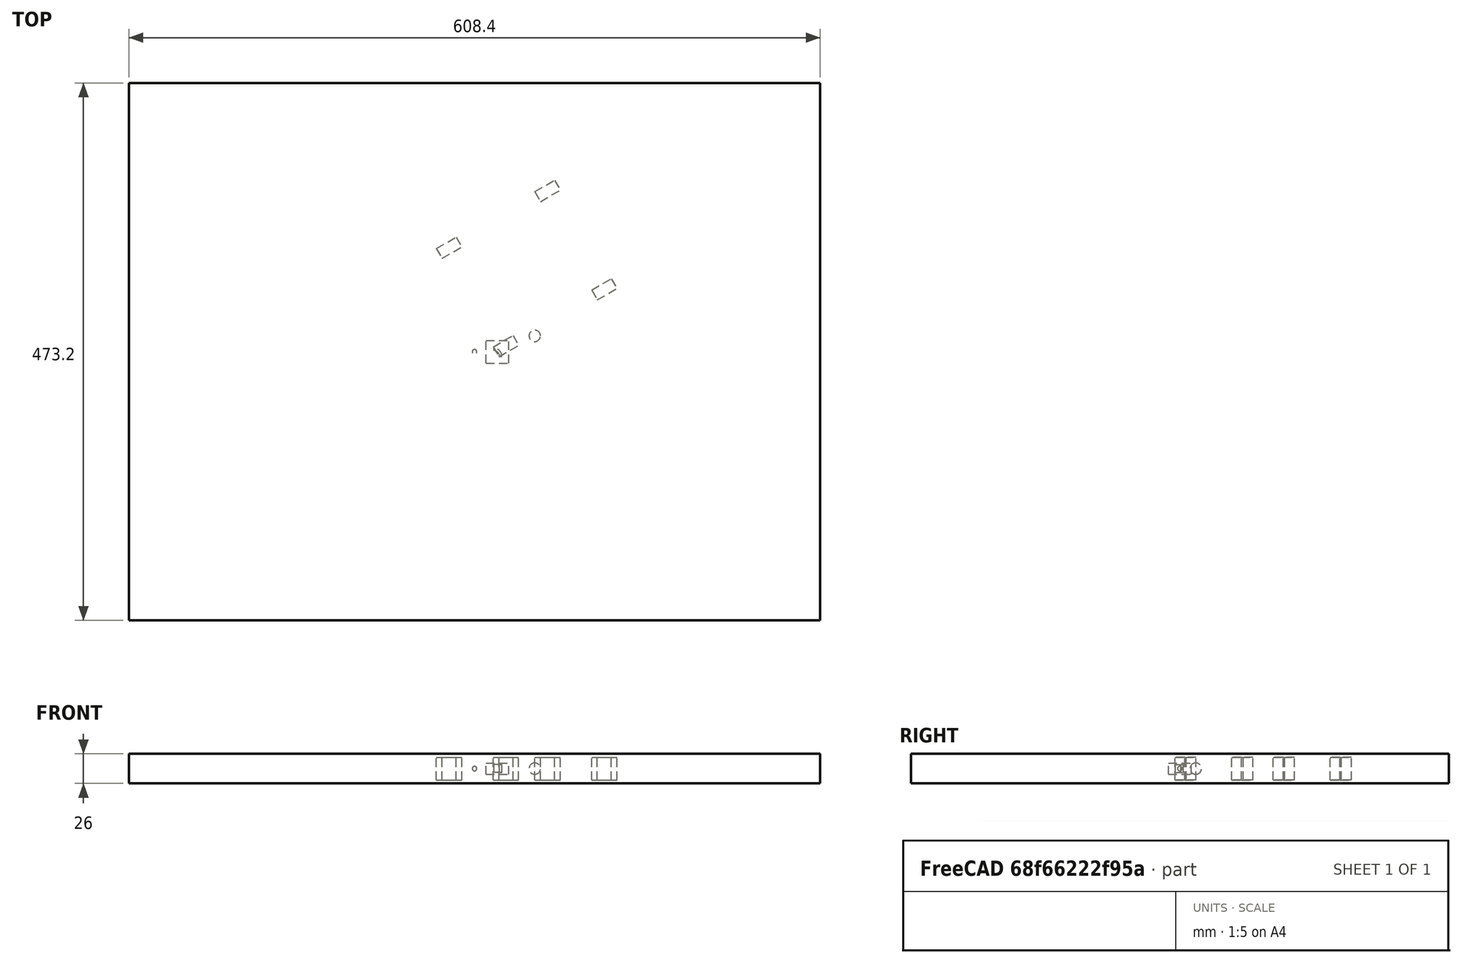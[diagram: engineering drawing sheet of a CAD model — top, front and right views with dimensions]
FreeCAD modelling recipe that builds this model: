
FCSTD DOCUMENT  (FreeCAD 1.0R39109 (Git))
Label: orthoArray-of-Container
License: All rights reserved
LicenseURL: http://en.wikipedia.org/wiki/All_rights_reserved
objects: App::DocumentObjectGroupPython×1251, App::Part×6, Part::FeaturePython×5, Part::Sphere×1
note: 6 computed .brp shape members not serialized (recipe doc carries the construction recipe); baked Part::Feature solids carry a one-line shape summary decoded from their .brp

FEATURE [App::DocumentObjectGroupPython] HALFPI  # scripted group (container) (typed FeaturePython)
  name = HALFPI
  value = pi/2.
FEATURE [App::DocumentObjectGroupPython] PI  # scripted group (container) (typed FeaturePython)
  name = PI
  value = 1.*pi
FEATURE [App::DocumentObjectGroupPython] TWOPI  # scripted group (container) (typed FeaturePython)
  name = TWOPI
  value = 2.*pi
FEATURE [App::DocumentObjectGroupPython] Constants  # scripted group (container) (typed FeaturePython)
  Group = -> [HALFPI,PI,TWOPI]
FEATURE [App::DocumentObjectGroupPython] Variables  # scripted group (container) (typed FeaturePython)
FEATURE [App::DocumentObjectGroupPython] Quantities  # scripted group (container) (typed FeaturePython)
FEATURE [App::DocumentObjectGroupPython] Isotopes  # scripted group (container) (typed FeaturePython)
FEATURE [App::DocumentObjectGroupPython] Elements  # scripted group (container) (typed FeaturePython)
FEATURE [App::DocumentObjectGroupPython] Matrix  # scripted group (container) (typed FeaturePython)
FEATURE [App::DocumentObjectGroupPython] Surfaces  # scripted group (container) (typed FeaturePython)
FEATURE [App::DocumentObjectGroupPython] Opticals  # scripted group (container) (typed FeaturePython)
  Group = -> [Matrix,Surfaces]
FEATURE [App::DocumentObjectGroupPython] G4Isotopes  # scripted group (container) (typed FeaturePython)
FEATURE [App::DocumentObjectGroupPython] H_element  # scripted group (container) (typed FeaturePython)
  Z = 1
  atom_value = 1.008
  formula = H
  name = H_element
FEATURE [App::DocumentObjectGroupPython] He_element  # scripted group (container) (typed FeaturePython)
  Z = 2
  atom_value = 4.0026
  formula = He
  name = He_element
FEATURE [App::DocumentObjectGroupPython] Li_element  # scripted group (container) (typed FeaturePython)
  Z = 3
  atom_value = 6.94
  formula = Li
  name = Li_element
FEATURE [App::DocumentObjectGroupPython] Be_element  # scripted group (container) (typed FeaturePython)
  Z = 4
  atom_value = 9.01218
  formula = Be
  name = Be_element
FEATURE [App::DocumentObjectGroupPython] B_element  # scripted group (container) (typed FeaturePython)
  Z = 5
  atom_value = 10.81
  formula = B
  name = B_element
FEATURE [App::DocumentObjectGroupPython] C_element  # scripted group (container) (typed FeaturePython)
  Z = 6
  atom_value = 12.011
  formula = C
  name = C_element
FEATURE [App::DocumentObjectGroupPython] N_element  # scripted group (container) (typed FeaturePython)
  Z = 7
  atom_value = 14.007
  formula = N
  name = N_element
FEATURE [App::DocumentObjectGroupPython] O_element  # scripted group (container) (typed FeaturePython)
  Z = 8
  atom_value = 15.999
  formula = O
  name = O_element
FEATURE [App::DocumentObjectGroupPython] F_element  # scripted group (container) (typed FeaturePython)
  Z = 9
  atom_value = 18.9984
  formula = F
  name = F_element
FEATURE [App::DocumentObjectGroupPython] Ne_element  # scripted group (container) (typed FeaturePython)
  Z = 10
  atom_value = 20.1797
  formula = Ne
  name = Ne_element
FEATURE [App::DocumentObjectGroupPython] Na_element  # scripted group (container) (typed FeaturePython)
  Z = 11
  atom_value = 22.9898
  formula = Na
  name = Na_element
FEATURE [App::DocumentObjectGroupPython] Mg_element  # scripted group (container) (typed FeaturePython)
  Z = 12
  atom_value = 24.305
  formula = Mg
  name = Mg_element
FEATURE [App::DocumentObjectGroupPython] Al_element  # scripted group (container) (typed FeaturePython)
  Z = 13
  atom_value = 26.9815
  formula = Al
  name = Al_element
FEATURE [App::DocumentObjectGroupPython] Si_element  # scripted group (container) (typed FeaturePython)
  Z = 14
  atom_value = 28.085
  formula = Si
  name = Si_element
FEATURE [App::DocumentObjectGroupPython] P_element  # scripted group (container) (typed FeaturePython)
  Z = 15
  atom_value = 30.9738
  formula = P
  name = P_element
FEATURE [App::DocumentObjectGroupPython] S_element  # scripted group (container) (typed FeaturePython)
  Z = 16
  atom_value = 32.06
  formula = S
  name = S_element
FEATURE [App::DocumentObjectGroupPython] Cl_element  # scripted group (container) (typed FeaturePython)
  Z = 17
  atom_value = 35.45
  formula = Cl
  name = Cl_element
FEATURE [App::DocumentObjectGroupPython] Ar_element  # scripted group (container) (typed FeaturePython)
  Z = 18
  atom_value = 39.95
  formula = Ar
  name = Ar_element
FEATURE [App::DocumentObjectGroupPython] K_element  # scripted group (container) (typed FeaturePython)
  Z = 19
  atom_value = 39.0983
  formula = K
  name = K_element
FEATURE [App::DocumentObjectGroupPython] Ca_element  # scripted group (container) (typed FeaturePython)
  Z = 20
  atom_value = 40.078
  formula = Ca
  name = Ca_element
FEATURE [App::DocumentObjectGroupPython] Sc_element  # scripted group (container) (typed FeaturePython)
  Z = 21
  atom_value = 44.9559
  formula = Sc
  name = Sc_element
FEATURE [App::DocumentObjectGroupPython] Ti_element  # scripted group (container) (typed FeaturePython)
  Z = 22
  atom_value = 47.867
  formula = Ti
  name = Ti_element
FEATURE [App::DocumentObjectGroupPython] V_element  # scripted group (container) (typed FeaturePython)
  Z = 23
  atom_value = 50.9415
  formula = V
  name = V_element
FEATURE [App::DocumentObjectGroupPython] Cr_element  # scripted group (container) (typed FeaturePython)
  Z = 24
  atom_value = 51.9961
  formula = Cr
  name = Cr_element
FEATURE [App::DocumentObjectGroupPython] Mn_element  # scripted group (container) (typed FeaturePython)
  Z = 25
  atom_value = 54.938
  formula = Mn
  name = Mn_element
FEATURE [App::DocumentObjectGroupPython] Fe_element  # scripted group (container) (typed FeaturePython)
  Z = 26
  atom_value = 55.845
  formula = Fe
  name = Fe_element
FEATURE [App::DocumentObjectGroupPython] Co_element  # scripted group (container) (typed FeaturePython)
  Z = 27
  atom_value = 58.9332
  formula = Co
  name = Co_element
FEATURE [App::DocumentObjectGroupPython] Ni_element  # scripted group (container) (typed FeaturePython)
  Z = 28
  atom_value = 58.6934
  formula = Ni
  name = Ni_element
FEATURE [App::DocumentObjectGroupPython] Cu_element  # scripted group (container) (typed FeaturePython)
  Z = 29
  atom_value = 63.546
  formula = Cu
  name = Cu_element
FEATURE [App::DocumentObjectGroupPython] Zn_element  # scripted group (container) (typed FeaturePython)
  Z = 30
  atom_value = 65.38
  formula = Zn
  name = Zn_element
FEATURE [App::DocumentObjectGroupPython] Ga_element  # scripted group (container) (typed FeaturePython)
  Z = 31
  atom_value = 69.723
  formula = Ga
  name = Ga_element
FEATURE [App::DocumentObjectGroupPython] Ge_element  # scripted group (container) (typed FeaturePython)
  Z = 32
  atom_value = 72.63
  formula = Ge
  name = Ge_element
FEATURE [App::DocumentObjectGroupPython] As_element  # scripted group (container) (typed FeaturePython)
  Z = 33
  atom_value = 74.9216
  formula = As
  name = As_element
FEATURE [App::DocumentObjectGroupPython] Se_element  # scripted group (container) (typed FeaturePython)
  Z = 34
  atom_value = 78.971
  formula = Se
  name = Se_element
FEATURE [App::DocumentObjectGroupPython] Br_element  # scripted group (container) (typed FeaturePython)
  Z = 35
  atom_value = 79.904
  formula = Br
  name = Br_element
FEATURE [App::DocumentObjectGroupPython] Kr_element  # scripted group (container) (typed FeaturePython)
  Z = 36
  atom_value = 83.798
  formula = Kr
  name = Kr_element
FEATURE [App::DocumentObjectGroupPython] Rb_element  # scripted group (container) (typed FeaturePython)
  Z = 37
  atom_value = 85.4678
  formula = Rb
  name = Rb_element
FEATURE [App::DocumentObjectGroupPython] Sr_element  # scripted group (container) (typed FeaturePython)
  Z = 38
  atom_value = 87.62
  formula = Sr
  name = Sr_element
FEATURE [App::DocumentObjectGroupPython] Y_element  # scripted group (container) (typed FeaturePython)
  Z = 39
  atom_value = 88.9058
  formula = Y
  name = Y_element
FEATURE [App::DocumentObjectGroupPython] Zr_element  # scripted group (container) (typed FeaturePython)
  Z = 40
  atom_value = 91.224
  formula = Zr
  name = Zr_element
FEATURE [App::DocumentObjectGroupPython] Nb_element  # scripted group (container) (typed FeaturePython)
  Z = 41
  atom_value = 92.9064
  formula = Nb
  name = Nb_element
FEATURE [App::DocumentObjectGroupPython] Mo_element  # scripted group (container) (typed FeaturePython)
  Z = 42
  atom_value = 95.95
  formula = Mo
  name = Mo_element
FEATURE [App::DocumentObjectGroupPython] Tc_element  # scripted group (container) (typed FeaturePython)
  Z = 43
  atom_value = 97
  formula = Tc
  name = Tc_element
FEATURE [App::DocumentObjectGroupPython] Ru_element  # scripted group (container) (typed FeaturePython)
  Z = 44
  atom_value = 101.07
  formula = Ru
  name = Ru_element
FEATURE [App::DocumentObjectGroupPython] Rh_element  # scripted group (container) (typed FeaturePython)
  Z = 45
  atom_value = 102.905
  formula = Rh
  name = Rh_element
FEATURE [App::DocumentObjectGroupPython] Pd_element  # scripted group (container) (typed FeaturePython)
  Z = 46
  atom_value = 106.42
  formula = Pd
  name = Pd_element
FEATURE [App::DocumentObjectGroupPython] Ag_element  # scripted group (container) (typed FeaturePython)
  Z = 47
  atom_value = 107.868
  formula = Ag
  name = Ag_element
FEATURE [App::DocumentObjectGroupPython] Cd_element  # scripted group (container) (typed FeaturePython)
  Z = 48
  atom_value = 112.414
  formula = Cd
  name = Cd_element
FEATURE [App::DocumentObjectGroupPython] In_element  # scripted group (container) (typed FeaturePython)
  Z = 49
  atom_value = 114.818
  formula = In
  name = In_element
FEATURE [App::DocumentObjectGroupPython] Sn_element  # scripted group (container) (typed FeaturePython)
  Z = 50
  atom_value = 118.71
  formula = Sn
  name = Sn_element
FEATURE [App::DocumentObjectGroupPython] Sb_element  # scripted group (container) (typed FeaturePython)
  Z = 51
  atom_value = 121.76
  formula = Sb
  name = Sb_element
FEATURE [App::DocumentObjectGroupPython] Te_element  # scripted group (container) (typed FeaturePython)
  Z = 52
  atom_value = 127.6
  formula = Te
  name = Te_element
FEATURE [App::DocumentObjectGroupPython] I_element  # scripted group (container) (typed FeaturePython)
  Z = 53
  atom_value = 126.904
  formula = I
  name = I_element
FEATURE [App::DocumentObjectGroupPython] Xe_element  # scripted group (container) (typed FeaturePython)
  Z = 54
  atom_value = 131.293
  formula = Xe
  name = Xe_element
FEATURE [App::DocumentObjectGroupPython] Cs_element  # scripted group (container) (typed FeaturePython)
  Z = 55
  atom_value = 132.905
  formula = Cs
  name = Cs_element
FEATURE [App::DocumentObjectGroupPython] Ba_element  # scripted group (container) (typed FeaturePython)
  Z = 56
  atom_value = 137.327
  formula = Ba
  name = Ba_element
FEATURE [App::DocumentObjectGroupPython] La_element  # scripted group (container) (typed FeaturePython)
  Z = 57
  atom_value = 138.905
  formula = La
  name = La_element
FEATURE [App::DocumentObjectGroupPython] Ce_element  # scripted group (container) (typed FeaturePython)
  Z = 58
  atom_value = 140.116
  formula = Ce
  name = Ce_element
FEATURE [App::DocumentObjectGroupPython] Pr_element  # scripted group (container) (typed FeaturePython)
  Z = 59
  atom_value = 140.908
  formula = Pr
  name = Pr_element
FEATURE [App::DocumentObjectGroupPython] Nd_element  # scripted group (container) (typed FeaturePython)
  Z = 60
  atom_value = 144.242
  formula = Nd
  name = Nd_element
FEATURE [App::DocumentObjectGroupPython] Pm_element  # scripted group (container) (typed FeaturePython)
  Z = 61
  atom_value = 145
  formula = Pm
  name = Pm_element
FEATURE [App::DocumentObjectGroupPython] Sm_element  # scripted group (container) (typed FeaturePython)
  Z = 62
  atom_value = 150.36
  formula = Sm
  name = Sm_element
FEATURE [App::DocumentObjectGroupPython] Eu_element  # scripted group (container) (typed FeaturePython)
  Z = 63
  atom_value = 151.964
  formula = Eu
  name = Eu_element
FEATURE [App::DocumentObjectGroupPython] Gd_element  # scripted group (container) (typed FeaturePython)
  Z = 64
  atom_value = 157.25
  formula = Gd
  name = Gd_element
FEATURE [App::DocumentObjectGroupPython] Tb_element  # scripted group (container) (typed FeaturePython)
  Z = 65
  atom_value = 158.925
  formula = Tb
  name = Tb_element
FEATURE [App::DocumentObjectGroupPython] Dy_element  # scripted group (container) (typed FeaturePython)
  Z = 66
  atom_value = 162.5
  formula = Dy
  name = Dy_element
FEATURE [App::DocumentObjectGroupPython] Ho_element  # scripted group (container) (typed FeaturePython)
  Z = 67
  atom_value = 164.93
  formula = Ho
  name = Ho_element
FEATURE [App::DocumentObjectGroupPython] Er_element  # scripted group (container) (typed FeaturePython)
  Z = 68
  atom_value = 167.259
  formula = Er
  name = Er_element
FEATURE [App::DocumentObjectGroupPython] Tm_element  # scripted group (container) (typed FeaturePython)
  Z = 69
  atom_value = 168.934
  formula = Tm
  name = Tm_element
FEATURE [App::DocumentObjectGroupPython] Yb_element  # scripted group (container) (typed FeaturePython)
  Z = 70
  atom_value = 173.045
  formula = Yb
  name = Yb_element
FEATURE [App::DocumentObjectGroupPython] Lu_element  # scripted group (container) (typed FeaturePython)
  Z = 71
  atom_value = 174.967
  formula = Lu
  name = Lu_element
FEATURE [App::DocumentObjectGroupPython] Hf_element  # scripted group (container) (typed FeaturePython)
  Z = 72
  atom_value = 178.49
  formula = Hf
  name = Hf_element
FEATURE [App::DocumentObjectGroupPython] Ta_element  # scripted group (container) (typed FeaturePython)
  Z = 73
  atom_value = 180.948
  formula = Ta
  name = Ta_element
FEATURE [App::DocumentObjectGroupPython] W_element  # scripted group (container) (typed FeaturePython)
  Z = 74
  atom_value = 183.84
  formula = W
  name = W_element
FEATURE [App::DocumentObjectGroupPython] Re_element  # scripted group (container) (typed FeaturePython)
  Z = 75
  atom_value = 186.207
  formula = Re
  name = Re_element
FEATURE [App::DocumentObjectGroupPython] Os_element  # scripted group (container) (typed FeaturePython)
  Z = 76
  atom_value = 190.23
  formula = Os
  name = Os_element
FEATURE [App::DocumentObjectGroupPython] Ir_element  # scripted group (container) (typed FeaturePython)
  Z = 77
  atom_value = 192.217
  formula = Ir
  name = Ir_element
FEATURE [App::DocumentObjectGroupPython] Pt_element  # scripted group (container) (typed FeaturePython)
  Z = 78
  atom_value = 195.084
  formula = Pt
  name = Pt_element
FEATURE [App::DocumentObjectGroupPython] Au_element  # scripted group (container) (typed FeaturePython)
  Z = 79
  atom_value = 196.967
  formula = Au
  name = Au_element
FEATURE [App::DocumentObjectGroupPython] Hg_element  # scripted group (container) (typed FeaturePython)
  Z = 80
  atom_value = 200.592
  formula = Hg
  name = Hg_element
FEATURE [App::DocumentObjectGroupPython] Tl_element  # scripted group (container) (typed FeaturePython)
  Z = 81
  atom_value = 204.38
  formula = Tl
  name = Tl_element
FEATURE [App::DocumentObjectGroupPython] Pb_element  # scripted group (container) (typed FeaturePython)
  Z = 82
  atom_value = 207.2
  formula = Pb
  name = Pb_element
FEATURE [App::DocumentObjectGroupPython] Bi_element  # scripted group (container) (typed FeaturePython)
  Z = 83
  atom_value = 208.98
  formula = Bi
  name = Bi_element
FEATURE [App::DocumentObjectGroupPython] Po_element  # scripted group (container) (typed FeaturePython)
  Z = 84
  atom_value = 209
  formula = Po
  name = Po_element
FEATURE [App::DocumentObjectGroupPython] At_element  # scripted group (container) (typed FeaturePython)
  Z = 85
  atom_value = 210
  formula = At
  name = At_element
FEATURE [App::DocumentObjectGroupPython] Rn_element  # scripted group (container) (typed FeaturePython)
  Z = 86
  atom_value = 222
  formula = Rn
  name = Rn_element
FEATURE [App::DocumentObjectGroupPython] Fr_element  # scripted group (container) (typed FeaturePython)
  Z = 87
  atom_value = 223
  formula = Fr
  name = Fr_element
FEATURE [App::DocumentObjectGroupPython] Ra_element  # scripted group (container) (typed FeaturePython)
  Z = 88
  atom_value = 226
  formula = Ra
  name = Ra_element
FEATURE [App::DocumentObjectGroupPython] Ac_element  # scripted group (container) (typed FeaturePython)
  Z = 89
  atom_value = 227
  formula = Ac
  name = Ac_element
FEATURE [App::DocumentObjectGroupPython] Th_element  # scripted group (container) (typed FeaturePython)
  Z = 90
  atom_value = 232.038
  formula = Th
  name = Th_element
FEATURE [App::DocumentObjectGroupPython] Pa_element  # scripted group (container) (typed FeaturePython)
  Z = 91
  atom_value = 231.036
  formula = Pa
  name = Pa_element
FEATURE [App::DocumentObjectGroupPython] U_element  # scripted group (container) (typed FeaturePython)
  Z = 92
  atom_value = 238.029
  formula = U
  name = U_element
FEATURE [App::DocumentObjectGroupPython] Np_element  # scripted group (container) (typed FeaturePython)
  Z = 93
  atom_value = 237
  formula = Np
  name = Np_element
FEATURE [App::DocumentObjectGroupPython] Pu_element  # scripted group (container) (typed FeaturePython)
  Z = 94
  atom_value = 244
  formula = Pu
  name = Pu_element
FEATURE [App::DocumentObjectGroupPython] Am_element  # scripted group (container) (typed FeaturePython)
  Z = 95
  atom_value = 243
  formula = Am
  name = Am_element
FEATURE [App::DocumentObjectGroupPython] Cm_element  # scripted group (container) (typed FeaturePython)
  Z = 96
  atom_value = 247
  formula = Cm
  name = Cm_element
FEATURE [App::DocumentObjectGroupPython] Bk_element  # scripted group (container) (typed FeaturePython)
  Z = 97
  atom_value = 247
  formula = Bk
  name = Bk_element
FEATURE [App::DocumentObjectGroupPython] Cf_element  # scripted group (container) (typed FeaturePython)
  Z = 98
  atom_value = 251
  formula = Cf
  name = Cf_element
FEATURE [App::DocumentObjectGroupPython] G4Elements  # scripted group (container) (typed FeaturePython)
  Group = -> [H_element,He_element,Li_element,Be_element,B_element,C_element,N_element,O_element,F_element,Ne_element,Na_element,Mg_element,Al_element,Si_element,P_element,S_element,Cl_element,Ar_element,K_element,Ca_element,Sc_element,Ti_element,V_element,Cr_element,Mn_element,Fe_element,Co_element,Ni_element,Cu_element,Zn_element,Ga_element,Ge_element,As_element,Se_element,Br_element,Kr_element,Rb_element,+61 more]
FEATURE [App::DocumentObjectGroupPython] H_element001  label="H_element : 0.101"  # scripted group (container) (typed FeaturePython)
  n = 0.101327
FEATURE [App::DocumentObjectGroupPython] C_element001  label="C_element : 0.775"  # scripted group (container) (typed FeaturePython)
  n = 0.7755
FEATURE [App::DocumentObjectGroupPython] N_element001  label="N_element : 0.035"  # scripted group (container) (typed FeaturePython)
  n = 0.035057
FEATURE [App::DocumentObjectGroupPython] O_element001  label="O_element : 0.052"  # scripted group (container) (typed FeaturePython)
  n = 0.0523159
FEATURE [App::DocumentObjectGroupPython] F_element001  label="F_element : 0.017"  # scripted group (container) (typed FeaturePython)
  n = 0.017422
FEATURE [App::DocumentObjectGroupPython] Ca_element001  label="Ca_element : 0.018"  # scripted group (container) (typed FeaturePython)
  n = 0.018378
FEATURE [App::DocumentObjectGroupPython] G4_A_150_TISSUE  label="G4_A-150_TISSUE"  # scripted group (container) (typed FeaturePython)
  Dunit = g/cm3
  Dvalue = 1.127
  Group = -> [H_element001,C_element001,N_element001,O_element001,F_element001,Ca_element001]
  conduct = 2
  density = 1
  expand = 3
  formula = G4_A-150_TISSUE
  name = G4_A-150_TISSUE
  specific = 4
FEATURE [App::DocumentObjectGroupPython] C_element002  label="C_element : 3"  # scripted group (container) (typed FeaturePython)
  n = 3
  ref = C_element
FEATURE [App::DocumentObjectGroupPython] H_element002  label="H_element : 6"  # scripted group (container) (typed FeaturePython)
  n = 6
  ref = H_element
FEATURE [App::DocumentObjectGroupPython] O_element002  label="O_element : 1"  # scripted group (container) (typed FeaturePython)
  n = 1
  ref = O_element
FEATURE [App::DocumentObjectGroupPython] G4_ACETONE  # scripted group (container) (typed FeaturePython)
  Dunit = g/cm3
  Dvalue = 0.7899
  Group = -> [C_element002,H_element002,O_element002]
  conduct = 2
  density = 1
  expand = 3
  formula = G4_ACETONE
  name = G4_ACETONE
  specific = 4
FEATURE [App::DocumentObjectGroupPython] C_element003  label="C_element : 2"  # scripted group (container) (typed FeaturePython)
  n = 2
  ref = C_element
FEATURE [App::DocumentObjectGroupPython] H_element003  label="H_element : 2"  # scripted group (container) (typed FeaturePython)
  n = 2
  ref = H_element
FEATURE [App::DocumentObjectGroupPython] G4_ACETYLENE  # scripted group (container) (typed FeaturePython)
  Dunit = g/cm3
  Dvalue = 0.0010967
  Group = -> [C_element003,H_element003]
  conduct = 2
  density = 1
  expand = 3
  formula = G4_ACETYLENE
  name = G4_ACETYLENE
  specific = 4
FEATURE [App::DocumentObjectGroupPython] C_element004  label="C_element : 5"  # scripted group (container) (typed FeaturePython)
  n = 5
  ref = C_element
FEATURE [App::DocumentObjectGroupPython] H_element004  label="H_element : 5"  # scripted group (container) (typed FeaturePython)
  n = 5
  ref = H_element
FEATURE [App::DocumentObjectGroupPython] N_element002  label="N_element : 5"  # scripted group (container) (typed FeaturePython)
  n = 5
  ref = N_element
FEATURE [App::DocumentObjectGroupPython] G4_ADENINE  # scripted group (container) (typed FeaturePython)
  Dunit = g/cm3
  Dvalue = 1.6
  Group = -> [C_element004,H_element004,N_element002]
  conduct = 2
  density = 1
  expand = 3
  formula = G4_ADENINE
  name = G4_ADENINE
  specific = 4
FEATURE [App::DocumentObjectGroupPython] H_element005  label="H_element : 0.114"  # scripted group (container) (typed FeaturePython)
  n = 0.114
FEATURE [App::DocumentObjectGroupPython] C_element005  label="C_element : 0.598"  # scripted group (container) (typed FeaturePython)
  n = 0.598
FEATURE [App::DocumentObjectGroupPython] N_element003  label="N_element : 0.007"  # scripted group (container) (typed FeaturePython)
  n = 0.007
FEATURE [App::DocumentObjectGroupPython] O_element003  label="O_element : 0.278"  # scripted group (container) (typed FeaturePython)
  n = 0.278
FEATURE [App::DocumentObjectGroupPython] Na_element001  label="Na_element : 0.001"  # scripted group (container) (typed FeaturePython)
  n = 0.001
FEATURE [App::DocumentObjectGroupPython] S_element001  label="S_element : 0.001"  # scripted group (container) (typed FeaturePython)
  n = 0.001
FEATURE [App::DocumentObjectGroupPython] Cl_element001  label="Cl_element : 0.001"  # scripted group (container) (typed FeaturePython)
  n = 0.001
FEATURE [App::DocumentObjectGroupPython] G4_ADIPOSE_TISSUE_ICRP  # scripted group (container) (typed FeaturePython)
  Dunit = g/cm3
  Dvalue = 0.95
  Group = -> [H_element005,C_element005,N_element003,O_element003,Na_element001,S_element001,Cl_element001]
  conduct = 2
  density = 1
  expand = 3
  formula = G4_ADIPOSE_TISSUE_ICRP
  name = G4_ADIPOSE_TISSUE_ICRP
  specific = 4
FEATURE [App::DocumentObjectGroupPython] C_element006  label="C_element : 0.000"  # scripted group (container) (typed FeaturePython)
  n = 0.000124
FEATURE [App::DocumentObjectGroupPython] N_element004  label="N_element : 0.755"  # scripted group (container) (typed FeaturePython)
  n = 0.755268
FEATURE [App::DocumentObjectGroupPython] O_element004  label="O_element : 0.232"  # scripted group (container) (typed FeaturePython)
  n = 0.231781
FEATURE [App::DocumentObjectGroupPython] Ar_element001  label="Ar_element : 0.013"  # scripted group (container) (typed FeaturePython)
  n = 0.012827
FEATURE [App::DocumentObjectGroupPython] G4_AIR  # scripted group (container) (typed FeaturePython)
  Dunit = g/cm3
  Dvalue = 0.00120479
  Group = -> [C_element006,N_element004,O_element004,Ar_element001]
  conduct = 2
  density = 1
  expand = 3
  formula = G4_AIR
  name = G4_AIR
  specific = 4
FEATURE [App::DocumentObjectGroupPython] C_element007  label="C_element : 006"  # scripted group (container) (typed FeaturePython)
  n = 3
  ref = C_element
FEATURE [App::DocumentObjectGroupPython] H_element006  label="H_element : 7"  # scripted group (container) (typed FeaturePython)
  n = 7
  ref = H_element
FEATURE [App::DocumentObjectGroupPython] N_element005  label="N_element : 1"  # scripted group (container) (typed FeaturePython)
  n = 1
  ref = N_element
FEATURE [App::DocumentObjectGroupPython] O_element005  label="O_element : 2"  # scripted group (container) (typed FeaturePython)
  n = 2
  ref = O_element
FEATURE [App::DocumentObjectGroupPython] G4_ALANINE  # scripted group (container) (typed FeaturePython)
  Dunit = g/cm3
  Dvalue = 1.42
  Group = -> [C_element007,H_element006,N_element005,O_element005]
  conduct = 2
  density = 1
  expand = 3
  formula = G4_ALANINE
  name = G4_ALANINE
  specific = 4
FEATURE [App::DocumentObjectGroupPython] Al_element001  label="Al_element : 2"  # scripted group (container) (typed FeaturePython)
  n = 2
  ref = Al_element
FEATURE [App::DocumentObjectGroupPython] O_element006  label="O_element : 3"  # scripted group (container) (typed FeaturePython)
  n = 3
  ref = O_element
FEATURE [App::DocumentObjectGroupPython] G4_ALUMINUM_OXIDE  # scripted group (container) (typed FeaturePython)
  Dunit = g/cm3
  Dvalue = 3.97
  Group = -> [Al_element001,O_element006]
  conduct = 2
  density = 1
  expand = 3
  formula = G4_ALUMINUM_OXIDE
  name = G4_ALUMINUM_OXIDE
  specific = 4
FEATURE [App::DocumentObjectGroupPython] H_element007  label="H_element : 0.106"  # scripted group (container) (typed FeaturePython)
  n = 0.10593
FEATURE [App::DocumentObjectGroupPython] C_element008  label="C_element : 0.789"  # scripted group (container) (typed FeaturePython)
  n = 0.788974
FEATURE [App::DocumentObjectGroupPython] O_element007  label="O_element : 0.105"  # scripted group (container) (typed FeaturePython)
  n = 0.105096
FEATURE [App::DocumentObjectGroupPython] G4_AMBER  # scripted group (container) (typed FeaturePython)
  Dunit = g/cm3
  Dvalue = 1.1
  Group = -> [H_element007,C_element008,O_element007]
  conduct = 2
  density = 1
  expand = 3
  formula = G4_AMBER
  name = G4_AMBER
  specific = 4
FEATURE [App::DocumentObjectGroupPython] N_element006  label="N_element : 006"  # scripted group (container) (typed FeaturePython)
  n = 1
  ref = N_element
FEATURE [App::DocumentObjectGroupPython] H_element008  label="H_element : 3"  # scripted group (container) (typed FeaturePython)
  n = 3
  ref = H_element
FEATURE [App::DocumentObjectGroupPython] G4_AMMONIA  # scripted group (container) (typed FeaturePython)
  Dunit = g/cm3
  Dvalue = 0.000826019
  Group = -> [N_element006,H_element008]
  conduct = 2
  density = 1
  expand = 3
  formula = G4_AMMONIA
  name = G4_AMMONIA
  specific = 4
FEATURE [App::DocumentObjectGroupPython] C_element009  label="C_element : 6"  # scripted group (container) (typed FeaturePython)
  n = 6
  ref = C_element
FEATURE [App::DocumentObjectGroupPython] H_element009  label="H_element : 008"  # scripted group (container) (typed FeaturePython)
  n = 7
  ref = H_element
FEATURE [App::DocumentObjectGroupPython] N_element007  label="N_element : 007"  # scripted group (container) (typed FeaturePython)
  n = 1
  ref = N_element
FEATURE [App::DocumentObjectGroupPython] G4_ANILINE  # scripted group (container) (typed FeaturePython)
  Dunit = g/cm3
  Dvalue = 1.0235
  Group = -> [C_element009,H_element009,N_element007]
  conduct = 2
  density = 1
  expand = 3
  formula = G4_ANILINE
  name = G4_ANILINE
  specific = 4
FEATURE [App::DocumentObjectGroupPython] C_element010  label="C_element : 14"  # scripted group (container) (typed FeaturePython)
  n = 14
  ref = C_element
FEATURE [App::DocumentObjectGroupPython] H_element010  label="H_element : 10"  # scripted group (container) (typed FeaturePython)
  n = 10
  ref = H_element
FEATURE [App::DocumentObjectGroupPython] G4_ANTHRACENE  # scripted group (container) (typed FeaturePython)
  Dunit = g/cm3
  Dvalue = 1.283
  Group = -> [C_element010,H_element010]
  conduct = 2
  density = 1
  expand = 3
  formula = G4_ANTHRACENE
  name = G4_ANTHRACENE
  specific = 4
FEATURE [App::DocumentObjectGroupPython] H_element011  label="H_element : 0.065"  # scripted group (container) (typed FeaturePython)
  n = 0.0654709
FEATURE [App::DocumentObjectGroupPython] C_element011  label="C_element : 0.537"  # scripted group (container) (typed FeaturePython)
  n = 0.536944
FEATURE [App::DocumentObjectGroupPython] N_element008  label="N_element : 0.021"  # scripted group (container) (typed FeaturePython)
  n = 0.0215
FEATURE [App::DocumentObjectGroupPython] O_element008  label="O_element : 0.032"  # scripted group (container) (typed FeaturePython)
  n = 0.032085
FEATURE [App::DocumentObjectGroupPython] F_element002  label="F_element : 0.167"  # scripted group (container) (typed FeaturePython)
  n = 0.167411
FEATURE [App::DocumentObjectGroupPython] Ca_element002  label="Ca_element : 0.177"  # scripted group (container) (typed FeaturePython)
  n = 0.176589
FEATURE [App::DocumentObjectGroupPython] G4_B_100_BONE  label="G4_B-100_BONE"  # scripted group (container) (typed FeaturePython)
  Dunit = g/cm3
  Dvalue = 1.45
  Group = -> [H_element011,C_element011,N_element008,O_element008,F_element002,Ca_element002]
  conduct = 2
  density = 1
  expand = 3
  formula = G4_B-100_BONE
  name = G4_B-100_BONE
  specific = 4
FEATURE [App::DocumentObjectGroupPython] H_element012  label="H_element : 0.057"  # scripted group (container) (typed FeaturePython)
  n = 0.057441
FEATURE [App::DocumentObjectGroupPython] C_element012  label="C_element : 0.790"  # scripted group (container) (typed FeaturePython)
  n = 0.774591
FEATURE [App::DocumentObjectGroupPython] O_element009  label="O_element : 0.168"  # scripted group (container) (typed FeaturePython)
  n = 0.167968
FEATURE [App::DocumentObjectGroupPython] G4_BAKELITE  # scripted group (container) (typed FeaturePython)
  Dunit = g/cm3
  Dvalue = 1.25
  Group = -> [H_element012,C_element012,O_element009]
  conduct = 2
  density = 1
  expand = 3
  formula = G4_BAKELITE
  name = G4_BAKELITE
  specific = 4
FEATURE [App::DocumentObjectGroupPython] Ba_element001  label="Ba_element : 1"  # scripted group (container) (typed FeaturePython)
  n = 1
  ref = Ba_element
FEATURE [App::DocumentObjectGroupPython] F_element003  label="F_element : 2"  # scripted group (container) (typed FeaturePython)
  n = 2
  ref = F_element
FEATURE [App::DocumentObjectGroupPython] G4_BARIUM_FLUORIDE  # scripted group (container) (typed FeaturePython)
  Dunit = g/cm3
  Dvalue = 4.89
  Group = -> [Ba_element001,F_element003]
  conduct = 2
  density = 1
  expand = 3
  formula = G4_BARIUM_FLUORIDE
  name = G4_BARIUM_FLUORIDE
  specific = 4
FEATURE [App::DocumentObjectGroupPython] Ba_element002  label="Ba_element : 002"  # scripted group (container) (typed FeaturePython)
  n = 1
  ref = Ba_element
FEATURE [App::DocumentObjectGroupPython] S_element002  label="S_element : 1"  # scripted group (container) (typed FeaturePython)
  n = 1
  ref = S_element
FEATURE [App::DocumentObjectGroupPython] O_element010  label="O_element : 4"  # scripted group (container) (typed FeaturePython)
  n = 4
  ref = O_element
FEATURE [App::DocumentObjectGroupPython] G4_BARIUM_SULFATE  # scripted group (container) (typed FeaturePython)
  Dunit = g/cm3
  Dvalue = 4.5
  Group = -> [Ba_element002,S_element002,O_element010]
  conduct = 2
  density = 1
  expand = 3
  formula = G4_BARIUM_SULFATE
  name = G4_BARIUM_SULFATE
  specific = 4
FEATURE [App::DocumentObjectGroupPython] C_element013  label="C_element : 007"  # scripted group (container) (typed FeaturePython)
  n = 6
  ref = C_element
FEATURE [App::DocumentObjectGroupPython] H_element013  label="H_element : 009"  # scripted group (container) (typed FeaturePython)
  n = 6
  ref = H_element
FEATURE [App::DocumentObjectGroupPython] G4_BENZENE  # scripted group (container) (typed FeaturePython)
  Dunit = g/cm3
  Dvalue = 0.87865
  Group = -> [C_element013,H_element013]
  conduct = 2
  density = 1
  expand = 3
  formula = G4_BENZENE
  name = G4_BENZENE
  specific = 4
FEATURE [App::DocumentObjectGroupPython] Be_element001  label="Be_element : 1"  # scripted group (container) (typed FeaturePython)
  n = 1
  ref = Be_element
FEATURE [App::DocumentObjectGroupPython] O_element011  label="O_element : 005"  # scripted group (container) (typed FeaturePython)
  n = 1
  ref = O_element
FEATURE [App::DocumentObjectGroupPython] G4_BERYLLIUM_OXIDE  # scripted group (container) (typed FeaturePython)
  Dunit = g/cm3
  Dvalue = 3.01
  Group = -> [Be_element001,O_element011]
  conduct = 2
  density = 1
  expand = 3
  formula = G4_BERYLLIUM_OXIDE
  name = G4_BERYLLIUM_OXIDE
  specific = 4
FEATURE [App::DocumentObjectGroupPython] Bi_element001  label="Bi_element : 4"  # scripted group (container) (typed FeaturePython)
  n = 4
  ref = Bi_element
FEATURE [App::DocumentObjectGroupPython] Ge_element001  label="Ge_element : 3"  # scripted group (container) (typed FeaturePython)
  n = 3
  ref = Ge_element
FEATURE [App::DocumentObjectGroupPython] O_element012  label="O_element : 12"  # scripted group (container) (typed FeaturePython)
  n = 12
  ref = O_element
FEATURE [App::DocumentObjectGroupPython] G4_BGO  # scripted group (container) (typed FeaturePython)
  Dunit = g/cm3
  Dvalue = 7.13
  Group = -> [Bi_element001,Ge_element001,O_element012]
  conduct = 2
  density = 1
  expand = 3
  formula = G4_BGO
  name = G4_BGO
  specific = 4
FEATURE [App::DocumentObjectGroupPython] H_element014  label="H_element : 0.102"  # scripted group (container) (typed FeaturePython)
  n = 0.102
FEATURE [App::DocumentObjectGroupPython] C_element014  label="C_element : 0.110"  # scripted group (container) (typed FeaturePython)
  n = 0.11
FEATURE [App::DocumentObjectGroupPython] N_element009  label="N_element : 0.033"  # scripted group (container) (typed FeaturePython)
  n = 0.033
FEATURE [App::DocumentObjectGroupPython] O_element013  label="O_element : 0.745"  # scripted group (container) (typed FeaturePython)
  n = 0.745
FEATURE [App::DocumentObjectGroupPython] Na_element002  label="Na_element : 0.002"  # scripted group (container) (typed FeaturePython)
  n = 0.001
FEATURE [App::DocumentObjectGroupPython] P_element001  label="P_element : 0.001"  # scripted group (container) (typed FeaturePython)
  n = 0.001
FEATURE [App::DocumentObjectGroupPython] S_element003  label="S_element : 0.002"  # scripted group (container) (typed FeaturePython)
  n = 0.002
FEATURE [App::DocumentObjectGroupPython] Cl_element002  label="Cl_element : 0.003"  # scripted group (container) (typed FeaturePython)
  n = 0.003
FEATURE [App::DocumentObjectGroupPython] K_element001  label="K_element : 0.002"  # scripted group (container) (typed FeaturePython)
  n = 0.002
FEATURE [App::DocumentObjectGroupPython] Fe_element001  label="Fe_element : 0.001"  # scripted group (container) (typed FeaturePython)
  n = 0.001
FEATURE [App::DocumentObjectGroupPython] G4_BLOOD_ICRP  # scripted group (container) (typed FeaturePython)
  Dunit = g/cm3
  Dvalue = 1.06
  Group = -> [H_element014,C_element014,N_element009,O_element013,Na_element002,P_element001,S_element003,Cl_element002,K_element001,Fe_element001]
  conduct = 2
  density = 1
  expand = 3
  formula = G4_BLOOD_ICRP
  name = G4_BLOOD_ICRP
  specific = 4
FEATURE [App::DocumentObjectGroupPython] H_element015  label="H_element : 0.064"  # scripted group (container) (typed FeaturePython)
  n = 0.064
FEATURE [App::DocumentObjectGroupPython] C_element015  label="C_element : 0.278"  # scripted group (container) (typed FeaturePython)
  n = 0.278
FEATURE [App::DocumentObjectGroupPython] N_element010  label="N_element : 0.027"  # scripted group (container) (typed FeaturePython)
  n = 0.027
FEATURE [App::DocumentObjectGroupPython] O_element014  label="O_element : 0.410"  # scripted group (container) (typed FeaturePython)
  n = 0.41
FEATURE [App::DocumentObjectGroupPython] Mg_element001  label="Mg_element : 0.002"  # scripted group (container) (typed FeaturePython)
  n = 0.002
FEATURE [App::DocumentObjectGroupPython] P_element002  label="P_element : 0.070"  # scripted group (container) (typed FeaturePython)
  n = 0.07
FEATURE [App::DocumentObjectGroupPython] S_element004  label="S_element : 0.003"  # scripted group (container) (typed FeaturePython)
  n = 0.002
FEATURE [App::DocumentObjectGroupPython] Ca_element003  label="Ca_element : 0.147"  # scripted group (container) (typed FeaturePython)
  n = 0.147
FEATURE [App::DocumentObjectGroupPython] G4_BONE_COMPACT_ICRU  # scripted group (container) (typed FeaturePython)
  Dunit = g/cm3
  Dvalue = 1.85
  Group = -> [H_element015,C_element015,N_element010,O_element014,Mg_element001,P_element002,S_element004,Ca_element003]
  conduct = 2
  density = 1
  expand = 3
  formula = G4_BONE_COMPACT_ICRU
  name = G4_BONE_COMPACT_ICRU
  specific = 4
FEATURE [App::DocumentObjectGroupPython] H_element016  label="H_element : 0.034"  # scripted group (container) (typed FeaturePython)
  n = 0.034
FEATURE [App::DocumentObjectGroupPython] C_element016  label="C_element : 0.155"  # scripted group (container) (typed FeaturePython)
  n = 0.155
FEATURE [App::DocumentObjectGroupPython] N_element011  label="N_element : 0.042"  # scripted group (container) (typed FeaturePython)
  n = 0.042
FEATURE [App::DocumentObjectGroupPython] O_element015  label="O_element : 0.435"  # scripted group (container) (typed FeaturePython)
  n = 0.435
FEATURE [App::DocumentObjectGroupPython] Na_element003  label="Na_element : 0.003"  # scripted group (container) (typed FeaturePython)
  n = 0.001
FEATURE [App::DocumentObjectGroupPython] Mg_element002  label="Mg_element : 0.003"  # scripted group (container) (typed FeaturePython)
  n = 0.002
FEATURE [App::DocumentObjectGroupPython] P_element003  label="P_element : 0.103"  # scripted group (container) (typed FeaturePython)
  n = 0.103
FEATURE [App::DocumentObjectGroupPython] S_element005  label="S_element : 0.004"  # scripted group (container) (typed FeaturePython)
  n = 0.003
FEATURE [App::DocumentObjectGroupPython] Ca_element004  label="Ca_element : 0.225"  # scripted group (container) (typed FeaturePython)
  n = 0.225
FEATURE [App::DocumentObjectGroupPython] G4_BONE_CORTICAL_ICRP  # scripted group (container) (typed FeaturePython)
  Dunit = g/cm3
  Dvalue = 1.92
  Group = -> [H_element016,C_element016,N_element011,O_element015,Na_element003,Mg_element002,P_element003,S_element005,Ca_element004]
  conduct = 2
  density = 1
  expand = 3
  formula = G4_BONE_CORTICAL_ICRP
  name = G4_BONE_CORTICAL_ICRP
  specific = 4
FEATURE [App::DocumentObjectGroupPython] B_element001  label="B_element : 4"  # scripted group (container) (typed FeaturePython)
  n = 4
  ref = B_element
FEATURE [App::DocumentObjectGroupPython] C_element017  label="C_element : 1"  # scripted group (container) (typed FeaturePython)
  n = 1
  ref = C_element
FEATURE [App::DocumentObjectGroupPython] G4_BORON_CARBIDE  # scripted group (container) (typed FeaturePython)
  Dunit = g/cm3
  Dvalue = 2.52
  Group = -> [B_element001,C_element017]
  conduct = 2
  density = 1
  expand = 3
  formula = G4_BORON_CARBIDE
  name = G4_BORON_CARBIDE
  specific = 4
FEATURE [App::DocumentObjectGroupPython] B_element002  label="B_element : 2"  # scripted group (container) (typed FeaturePython)
  n = 2
  ref = B_element
FEATURE [App::DocumentObjectGroupPython] O_element016  label="O_element : 006"  # scripted group (container) (typed FeaturePython)
  n = 3
  ref = O_element
FEATURE [App::DocumentObjectGroupPython] G4_BORON_OXIDE  # scripted group (container) (typed FeaturePython)
  Dunit = g/cm3
  Dvalue = 1.812
  Group = -> [B_element002,O_element016]
  conduct = 2
  density = 1
  expand = 3
  formula = G4_BORON_OXIDE
  name = G4_BORON_OXIDE
  specific = 4
FEATURE [App::DocumentObjectGroupPython] H_element017  label="H_element : 0.107"  # scripted group (container) (typed FeaturePython)
  n = 0.107
FEATURE [App::DocumentObjectGroupPython] C_element018  label="C_element : 0.145"  # scripted group (container) (typed FeaturePython)
  n = 0.145
FEATURE [App::DocumentObjectGroupPython] N_element012  label="N_element : 0.022"  # scripted group (container) (typed FeaturePython)
  n = 0.022
FEATURE [App::DocumentObjectGroupPython] O_element017  label="O_element : 0.712"  # scripted group (container) (typed FeaturePython)
  n = 0.712
FEATURE [App::DocumentObjectGroupPython] Na_element004  label="Na_element : 0.004"  # scripted group (container) (typed FeaturePython)
  n = 0.002
FEATURE [App::DocumentObjectGroupPython] P_element004  label="P_element : 0.004"  # scripted group (container) (typed FeaturePython)
  n = 0.004
FEATURE [App::DocumentObjectGroupPython] S_element006  label="S_element : 0.005"  # scripted group (container) (typed FeaturePython)
  n = 0.002
FEATURE [App::DocumentObjectGroupPython] Cl_element003  label="Cl_element : 0.004"  # scripted group (container) (typed FeaturePython)
  n = 0.003
FEATURE [App::DocumentObjectGroupPython] K_element002  label="K_element : 0.003"  # scripted group (container) (typed FeaturePython)
  n = 0.003
FEATURE [App::DocumentObjectGroupPython] G4_BRAIN_ICRP  # scripted group (container) (typed FeaturePython)
  Dunit = g/cm3
  Dvalue = 1.04
  Group = -> [H_element017,C_element018,N_element012,O_element017,Na_element004,P_element004,S_element006,Cl_element003,K_element002]
  conduct = 2
  density = 1
  expand = 3
  formula = G4_BRAIN_ICRP
  name = G4_BRAIN_ICRP
  specific = 4
FEATURE [App::DocumentObjectGroupPython] C_element019  label="C_element : 4"  # scripted group (container) (typed FeaturePython)
  n = 4
  ref = C_element
FEATURE [App::DocumentObjectGroupPython] H_element018  label="H_element : 010"  # scripted group (container) (typed FeaturePython)
  n = 10
  ref = H_element
FEATURE [App::DocumentObjectGroupPython] G4_BUTANE  # scripted group (container) (typed FeaturePython)
  Dunit = g/cm3
  Dvalue = 0.00249343
  Group = -> [C_element019,H_element018]
  conduct = 2
  density = 1
  expand = 3
  formula = G4_BUTANE
  name = G4_BUTANE
  specific = 4
FEATURE [App::DocumentObjectGroupPython] C_element020  label="C_element : 008"  # scripted group (container) (typed FeaturePython)
  n = 4
  ref = C_element
FEATURE [App::DocumentObjectGroupPython] H_element019  label="H_element : 011"  # scripted group (container) (typed FeaturePython)
  n = 10
  ref = H_element
FEATURE [App::DocumentObjectGroupPython] O_element018  label="O_element : 007"  # scripted group (container) (typed FeaturePython)
  n = 1
  ref = O_element
FEATURE [App::DocumentObjectGroupPython] G4_N_BUTYL_ALCOHOL  label="G4_N-BUTYL_ALCOHOL"  # scripted group (container) (typed FeaturePython)
  Dunit = g/cm3
  Dvalue = 0.8098
  Group = -> [C_element020,H_element019,O_element018]
  conduct = 2
  density = 1
  expand = 3
  formula = G4_N-BUTYL_ALCOHOL
  name = G4_N-BUTYL_ALCOHOL
  specific = 4
FEATURE [App::DocumentObjectGroupPython] H_element020  label="H_element : 0.025"  # scripted group (container) (typed FeaturePython)
  n = 0.02468
FEATURE [App::DocumentObjectGroupPython] C_element021  label="C_element : 0.502"  # scripted group (container) (typed FeaturePython)
  n = 0.501611
FEATURE [App::DocumentObjectGroupPython] O_element019  label="O_element : 0.005"  # scripted group (container) (typed FeaturePython)
  n = 0.004527
FEATURE [App::DocumentObjectGroupPython] F_element004  label="F_element : 0.465"  # scripted group (container) (typed FeaturePython)
  n = 0.465209
FEATURE [App::DocumentObjectGroupPython] Si_element001  label="Si_element : 0.004"  # scripted group (container) (typed FeaturePython)
  n = 0.003973
FEATURE [App::DocumentObjectGroupPython] G4_C_552  label="G4_C-552"  # scripted group (container) (typed FeaturePython)
  Dunit = g/cm3
  Dvalue = 1.76
  Group = -> [H_element020,C_element021,O_element019,F_element004,Si_element001]
  conduct = 2
  density = 1
  expand = 3
  formula = G4_C-552
  name = G4_C-552
  specific = 4
FEATURE [App::DocumentObjectGroupPython] Cd_element001  label="Cd_element : 1"  # scripted group (container) (typed FeaturePython)
  n = 1
  ref = Cd_element
FEATURE [App::DocumentObjectGroupPython] Te_element001  label="Te_element : 1"  # scripted group (container) (typed FeaturePython)
  n = 1
  ref = Te_element
FEATURE [App::DocumentObjectGroupPython] G4_CADMIUM_TELLURIDE  # scripted group (container) (typed FeaturePython)
  Dunit = g/cm3
  Dvalue = 6.2
  Group = -> [Cd_element001,Te_element001]
  conduct = 2
  density = 1
  expand = 3
  formula = G4_CADMIUM_TELLURIDE
  name = G4_CADMIUM_TELLURIDE
  specific = 4
FEATURE [App::DocumentObjectGroupPython] Cd_element002  label="Cd_element : 002"  # scripted group (container) (typed FeaturePython)
  n = 1
  ref = Cd_element
FEATURE [App::DocumentObjectGroupPython] W_element001  label="W_element : 1"  # scripted group (container) (typed FeaturePython)
  n = 1
  ref = W_element
FEATURE [App::DocumentObjectGroupPython] O_element020  label="O_element : 008"  # scripted group (container) (typed FeaturePython)
  n = 4
  ref = O_element
FEATURE [App::DocumentObjectGroupPython] G4_CADMIUM_TUNGSTATE  # scripted group (container) (typed FeaturePython)
  Dunit = g/cm3
  Dvalue = 7.9
  Group = -> [Cd_element002,W_element001,O_element020]
  conduct = 2
  density = 1
  expand = 3
  formula = G4_CADMIUM_TUNGSTATE
  name = G4_CADMIUM_TUNGSTATE
  specific = 4
FEATURE [App::DocumentObjectGroupPython] Ca_element005  label="Ca_element : 1"  # scripted group (container) (typed FeaturePython)
  n = 1
  ref = Ca_element
FEATURE [App::DocumentObjectGroupPython] C_element022  label="C_element : 009"  # scripted group (container) (typed FeaturePython)
  n = 1
  ref = C_element
FEATURE [App::DocumentObjectGroupPython] O_element021  label="O_element : 009"  # scripted group (container) (typed FeaturePython)
  n = 3
  ref = O_element
FEATURE [App::DocumentObjectGroupPython] G4_CALCIUM_CARBONATE  # scripted group (container) (typed FeaturePython)
  Dunit = g/cm3
  Dvalue = 2.8
  Group = -> [Ca_element005,C_element022,O_element021]
  conduct = 2
  density = 1
  expand = 3
  formula = G4_CALCIUM_CARBONATE
  name = G4_CALCIUM_CARBONATE
  specific = 4
FEATURE [App::DocumentObjectGroupPython] Ca_element006  label="Ca_element : 002"  # scripted group (container) (typed FeaturePython)
  n = 1
  ref = Ca_element
FEATURE [App::DocumentObjectGroupPython] F_element005  label="F_element : 003"  # scripted group (container) (typed FeaturePython)
  n = 2
  ref = F_element
FEATURE [App::DocumentObjectGroupPython] G4_CALCIUM_FLUORIDE  # scripted group (container) (typed FeaturePython)
  Dunit = g/cm3
  Dvalue = 3.18
  Group = -> [Ca_element006,F_element005]
  conduct = 2
  density = 1
  expand = 3
  formula = G4_CALCIUM_FLUORIDE
  name = G4_CALCIUM_FLUORIDE
  specific = 4
FEATURE [App::DocumentObjectGroupPython] Ca_element007  label="Ca_element : 003"  # scripted group (container) (typed FeaturePython)
  n = 1
  ref = Ca_element
FEATURE [App::DocumentObjectGroupPython] O_element022  label="O_element : 010"  # scripted group (container) (typed FeaturePython)
  n = 1
  ref = O_element
FEATURE [App::DocumentObjectGroupPython] G4_CALCIUM_OXIDE  # scripted group (container) (typed FeaturePython)
  Dunit = g/cm3
  Dvalue = 3.3
  Group = -> [Ca_element007,O_element022]
  conduct = 2
  density = 1
  expand = 3
  formula = G4_CALCIUM_OXIDE
  name = G4_CALCIUM_OXIDE
  specific = 4
FEATURE [App::DocumentObjectGroupPython] Ca_element008  label="Ca_element : 004"  # scripted group (container) (typed FeaturePython)
  n = 1
  ref = Ca_element
FEATURE [App::DocumentObjectGroupPython] S_element007  label="S_element : 002"  # scripted group (container) (typed FeaturePython)
  n = 1
  ref = S_element
FEATURE [App::DocumentObjectGroupPython] O_element023  label="O_element : 011"  # scripted group (container) (typed FeaturePython)
  n = 4
  ref = O_element
FEATURE [App::DocumentObjectGroupPython] G4_CALCIUM_SULFATE  # scripted group (container) (typed FeaturePython)
  Dunit = g/cm3
  Dvalue = 2.96
  Group = -> [Ca_element008,S_element007,O_element023]
  conduct = 2
  density = 1
  expand = 3
  formula = G4_CALCIUM_SULFATE
  name = G4_CALCIUM_SULFATE
  specific = 4
FEATURE [App::DocumentObjectGroupPython] Ca_element009  label="Ca_element : 005"  # scripted group (container) (typed FeaturePython)
  n = 1
  ref = Ca_element
FEATURE [App::DocumentObjectGroupPython] W_element002  label="W_element : 002"  # scripted group (container) (typed FeaturePython)
  n = 1
  ref = W_element
FEATURE [App::DocumentObjectGroupPython] O_element024  label="O_element : 012"  # scripted group (container) (typed FeaturePython)
  n = 4
  ref = O_element
FEATURE [App::DocumentObjectGroupPython] G4_CALCIUM_TUNGSTATE  # scripted group (container) (typed FeaturePython)
  Dunit = g/cm3
  Dvalue = 6.062
  Group = -> [Ca_element009,W_element002,O_element024]
  conduct = 2
  density = 1
  expand = 3
  formula = G4_CALCIUM_TUNGSTATE
  name = G4_CALCIUM_TUNGSTATE
  specific = 4
FEATURE [App::DocumentObjectGroupPython] C_element023  label="C_element : 010"  # scripted group (container) (typed FeaturePython)
  n = 1
  ref = C_element
FEATURE [App::DocumentObjectGroupPython] O_element025  label="O_element : 013"  # scripted group (container) (typed FeaturePython)
  n = 2
  ref = O_element
FEATURE [App::DocumentObjectGroupPython] G4_CARBON_DIOXIDE  # scripted group (container) (typed FeaturePython)
  Dunit = g/cm3
  Dvalue = 0.00184212
  Group = -> [C_element023,O_element025]
  conduct = 2
  density = 1
  expand = 3
  formula = G4_CARBON_DIOXIDE
  name = G4_CARBON_DIOXIDE
  specific = 4
FEATURE [App::DocumentObjectGroupPython] C_element024  label="C_element : 011"  # scripted group (container) (typed FeaturePython)
  n = 1
  ref = C_element
FEATURE [App::DocumentObjectGroupPython] Cl_element004  label="Cl_element : 4"  # scripted group (container) (typed FeaturePython)
  n = 4
  ref = Cl_element
FEATURE [App::DocumentObjectGroupPython] G4_CARBON_TETRACHLORIDE  # scripted group (container) (typed FeaturePython)
  Dunit = g/cm3
  Dvalue = 1.594
  Group = -> [C_element024,Cl_element004]
  conduct = 2
  density = 1
  expand = 3
  formula = G4_CARBON_TETRACHLORIDE
  name = G4_CARBON_TETRACHLORIDE
  specific = 4
FEATURE [App::DocumentObjectGroupPython] C_element025  label="C_element : 012"  # scripted group (container) (typed FeaturePython)
  n = 6
  ref = C_element
FEATURE [App::DocumentObjectGroupPython] H_element021  label="H_element : 012"  # scripted group (container) (typed FeaturePython)
  n = 10
  ref = H_element
FEATURE [App::DocumentObjectGroupPython] O_element026  label="O_element : 5"  # scripted group (container) (typed FeaturePython)
  n = 5
  ref = O_element
FEATURE [App::DocumentObjectGroupPython] G4_CELLULOSE_CELLOPHANE  # scripted group (container) (typed FeaturePython)
  Dunit = g/cm3
  Dvalue = 1.42
  Group = -> [C_element025,H_element021,O_element026]
  conduct = 2
  density = 1
  expand = 3
  formula = G4_CELLULOSE_CELLOPHANE
  name = G4_CELLULOSE_CELLOPHANE
  specific = 4
FEATURE [App::DocumentObjectGroupPython] H_element022  label="H_element : 0.067"  # scripted group (container) (typed FeaturePython)
  n = 0.067125
FEATURE [App::DocumentObjectGroupPython] C_element026  label="C_element : 0.545"  # scripted group (container) (typed FeaturePython)
  n = 0.545403
FEATURE [App::DocumentObjectGroupPython] O_element027  label="O_element : 0.387"  # scripted group (container) (typed FeaturePython)
  n = 0.387472
FEATURE [App::DocumentObjectGroupPython] G4_CELLULOSE_BUTYRATE  # scripted group (container) (typed FeaturePython)
  Dunit = g/cm3
  Dvalue = 1.2
  Group = -> [H_element022,C_element026,O_element027]
  conduct = 2
  density = 1
  expand = 3
  formula = G4_CELLULOSE_BUTYRATE
  name = G4_CELLULOSE_BUTYRATE
  specific = 4
FEATURE [App::DocumentObjectGroupPython] H_element023  label="H_element : 0.029"  # scripted group (container) (typed FeaturePython)
  n = 0.029216
FEATURE [App::DocumentObjectGroupPython] C_element027  label="C_element : 0.271"  # scripted group (container) (typed FeaturePython)
  n = 0.271296
FEATURE [App::DocumentObjectGroupPython] N_element013  label="N_element : 0.121"  # scripted group (container) (typed FeaturePython)
  n = 0.121276
FEATURE [App::DocumentObjectGroupPython] O_element028  label="O_element : 0.578"  # scripted group (container) (typed FeaturePython)
  n = 0.578212
FEATURE [App::DocumentObjectGroupPython] G4_CELLULOSE_NITRATE  # scripted group (container) (typed FeaturePython)
  Dunit = g/cm3
  Dvalue = 1.49
  Group = -> [H_element023,C_element027,N_element013,O_element028]
  conduct = 2
  density = 1
  expand = 3
  formula = G4_CELLULOSE_NITRATE
  name = G4_CELLULOSE_NITRATE
  specific = 4
FEATURE [App::DocumentObjectGroupPython] H_element024  label="H_element : 0.108"  # scripted group (container) (typed FeaturePython)
  n = 0.107596
FEATURE [App::DocumentObjectGroupPython] N_element014  label="N_element : 0.001"  # scripted group (container) (typed FeaturePython)
  n = 0.0008
FEATURE [App::DocumentObjectGroupPython] O_element029  label="O_element : 0.875"  # scripted group (container) (typed FeaturePython)
  n = 0.874976
FEATURE [App::DocumentObjectGroupPython] S_element008  label="S_element : 0.015"  # scripted group (container) (typed FeaturePython)
  n = 0.014627
FEATURE [App::DocumentObjectGroupPython] Ce_element001  label="Ce_element : 0.002"  # scripted group (container) (typed FeaturePython)
  n = 0.002001
FEATURE [App::DocumentObjectGroupPython] G4_CERIC_SULFATE  # scripted group (container) (typed FeaturePython)
  Dunit = g/cm3
  Dvalue = 1.03
  Group = -> [H_element024,N_element014,O_element029,S_element008,Ce_element001]
  conduct = 2
  density = 1
  expand = 3
  formula = G4_CERIC_SULFATE
  name = G4_CERIC_SULFATE
  specific = 4
FEATURE [App::DocumentObjectGroupPython] Cs_element001  label="Cs_element : 1"  # scripted group (container) (typed FeaturePython)
  n = 1
  ref = Cs_element
FEATURE [App::DocumentObjectGroupPython] F_element006  label="F_element : 1"  # scripted group (container) (typed FeaturePython)
  n = 1
  ref = F_element
FEATURE [App::DocumentObjectGroupPython] G4_CESIUM_FLUORIDE  # scripted group (container) (typed FeaturePython)
  Dunit = g/cm3
  Dvalue = 4.115
  Group = -> [Cs_element001,F_element006]
  conduct = 2
  density = 1
  expand = 3
  formula = G4_CESIUM_FLUORIDE
  name = G4_CESIUM_FLUORIDE
  specific = 4
FEATURE [App::DocumentObjectGroupPython] Cs_element002  label="Cs_element : 002"  # scripted group (container) (typed FeaturePython)
  n = 1
  ref = Cs_element
FEATURE [App::DocumentObjectGroupPython] I_element001  label="I_element : 1"  # scripted group (container) (typed FeaturePython)
  n = 1
  ref = I_element
FEATURE [App::DocumentObjectGroupPython] G4_CESIUM_IODIDE  # scripted group (container) (typed FeaturePython)
  Dunit = g/cm3
  Dvalue = 4.51
  Group = -> [Cs_element002,I_element001]
  conduct = 2
  density = 1
  expand = 3
  formula = G4_CESIUM_IODIDE
  name = G4_CESIUM_IODIDE
  specific = 4
FEATURE [App::DocumentObjectGroupPython] C_element028  label="C_element : 013"  # scripted group (container) (typed FeaturePython)
  n = 6
  ref = C_element
FEATURE [App::DocumentObjectGroupPython] H_element025  label="H_element : 013"  # scripted group (container) (typed FeaturePython)
  n = 5
  ref = H_element
FEATURE [App::DocumentObjectGroupPython] Cl_element005  label="Cl_element : 1"  # scripted group (container) (typed FeaturePython)
  n = 1
  ref = Cl_element
FEATURE [App::DocumentObjectGroupPython] G4_CHLOROBENZENE  # scripted group (container) (typed FeaturePython)
  Dunit = g/cm3
  Dvalue = 1.1058
  Group = -> [C_element028,H_element025,Cl_element005]
  conduct = 2
  density = 1
  expand = 3
  formula = G4_CHLOROBENZENE
  name = G4_CHLOROBENZENE
  specific = 4
FEATURE [App::DocumentObjectGroupPython] C_element029  label="C_element : 014"  # scripted group (container) (typed FeaturePython)
  n = 1
  ref = C_element
FEATURE [App::DocumentObjectGroupPython] H_element026  label="H_element : 1"  # scripted group (container) (typed FeaturePython)
  n = 1
  ref = H_element
FEATURE [App::DocumentObjectGroupPython] Cl_element006  label="Cl_element : 3"  # scripted group (container) (typed FeaturePython)
  n = 3
  ref = Cl_element
FEATURE [App::DocumentObjectGroupPython] G4_CHLOROFORM  # scripted group (container) (typed FeaturePython)
  Dunit = g/cm3
  Dvalue = 1.4832
  Group = -> [C_element029,H_element026,Cl_element006]
  conduct = 2
  density = 1
  expand = 3
  formula = G4_CHLOROFORM
  name = G4_CHLOROFORM
  specific = 4
FEATURE [App::DocumentObjectGroupPython] H_element027  label="H_element : 0.010"  # scripted group (container) (typed FeaturePython)
  n = 0.01
FEATURE [App::DocumentObjectGroupPython] C_element030  label="C_element : 0.001"  # scripted group (container) (typed FeaturePython)
  n = 0.001
FEATURE [App::DocumentObjectGroupPython] O_element030  label="O_element : 0.529"  # scripted group (container) (typed FeaturePython)
  n = 0.529107
FEATURE [App::DocumentObjectGroupPython] Na_element005  label="Na_element : 0.016"  # scripted group (container) (typed FeaturePython)
  n = 0.016
FEATURE [App::DocumentObjectGroupPython] Mg_element003  label="Mg_element : 0.004"  # scripted group (container) (typed FeaturePython)
  n = 0.002
FEATURE [App::DocumentObjectGroupPython] Al_element002  label="Al_element : 0.034"  # scripted group (container) (typed FeaturePython)
  n = 0.033872
FEATURE [App::DocumentObjectGroupPython] Si_element002  label="Si_element : 0.337"  # scripted group (container) (typed FeaturePython)
  n = 0.337021
FEATURE [App::DocumentObjectGroupPython] K_element003  label="K_element : 0.013"  # scripted group (container) (typed FeaturePython)
  n = 0.013
FEATURE [App::DocumentObjectGroupPython] Ca_element010  label="Ca_element : 0.044"  # scripted group (container) (typed FeaturePython)
  n = 0.044
FEATURE [App::DocumentObjectGroupPython] Fe_element002  label="Fe_element : 0.014"  # scripted group (container) (typed FeaturePython)
  n = 0.014
FEATURE [App::DocumentObjectGroupPython] G4_CONCRETE  # scripted group (container) (typed FeaturePython)
  Dunit = g/cm3
  Dvalue = 2.3
  Group = -> [H_element027,C_element030,O_element030,Na_element005,Mg_element003,Al_element002,Si_element002,K_element003,Ca_element010,Fe_element002]
  conduct = 2
  density = 1
  expand = 3
  formula = G4_CONCRETE
  name = G4_CONCRETE
  specific = 4
FEATURE [App::DocumentObjectGroupPython] C_element031  label="C_element : 015"  # scripted group (container) (typed FeaturePython)
  n = 6
  ref = C_element
FEATURE [App::DocumentObjectGroupPython] H_element028  label="H_element : 12"  # scripted group (container) (typed FeaturePython)
  n = 12
  ref = H_element
FEATURE [App::DocumentObjectGroupPython] G4_CYCLOHEXANE  # scripted group (container) (typed FeaturePython)
  Dunit = g/cm3
  Dvalue = 0.779
  Group = -> [C_element031,H_element028]
  conduct = 2
  density = 1
  expand = 3
  formula = G4_CYCLOHEXANE
  name = G4_CYCLOHEXANE
  specific = 4
FEATURE [App::DocumentObjectGroupPython] C_element032  label="C_element : 016"  # scripted group (container) (typed FeaturePython)
  n = 6
  ref = C_element
FEATURE [App::DocumentObjectGroupPython] H_element029  label="H_element : 4"  # scripted group (container) (typed FeaturePython)
  n = 4
  ref = H_element
FEATURE [App::DocumentObjectGroupPython] Cl_element007  label="Cl_element : 2"  # scripted group (container) (typed FeaturePython)
  n = 2
  ref = Cl_element
FEATURE [App::DocumentObjectGroupPython] G4_1_2_DICHLOROBENZENE  label="G4_1.2-DICHLOROBENZENE"  # scripted group (container) (typed FeaturePython)
  Dunit = g/cm3
  Dvalue = 1.3048
  Group = -> [C_element032,H_element029,Cl_element007]
  conduct = 2
  density = 1
  expand = 3
  formula = G4_1.2-DICHLOROBENZENE
  name = G4_1.2-DICHLOROBENZENE
  specific = 4
FEATURE [App::DocumentObjectGroupPython] C_element033  label="C_element : 017"  # scripted group (container) (typed FeaturePython)
  n = 4
  ref = C_element
FEATURE [App::DocumentObjectGroupPython] H_element030  label="H_element : 8"  # scripted group (container) (typed FeaturePython)
  n = 8
  ref = H_element
FEATURE [App::DocumentObjectGroupPython] O_element031  label="O_element : 014"  # scripted group (container) (typed FeaturePython)
  n = 1
  ref = O_element
FEATURE [App::DocumentObjectGroupPython] Cl_element008  label="Cl_element : 005"  # scripted group (container) (typed FeaturePython)
  n = 2
  ref = Cl_element
FEATURE [App::DocumentObjectGroupPython] G4_DICHLORODIETHYL_ETHER  # scripted group (container) (typed FeaturePython)
  Dunit = g/cm3
  Dvalue = 1.2199
  Group = -> [C_element033,H_element030,O_element031,Cl_element008]
  conduct = 2
  density = 1
  expand = 3
  formula = G4_DICHLORODIETHYL_ETHER
  name = G4_DICHLORODIETHYL_ETHER
  specific = 4
FEATURE [App::DocumentObjectGroupPython] C_element034  label="C_element : 018"  # scripted group (container) (typed FeaturePython)
  n = 2
  ref = C_element
FEATURE [App::DocumentObjectGroupPython] H_element031  label="H_element : 014"  # scripted group (container) (typed FeaturePython)
  n = 4
  ref = H_element
FEATURE [App::DocumentObjectGroupPython] Cl_element009  label="Cl_element : 006"  # scripted group (container) (typed FeaturePython)
  n = 2
  ref = Cl_element
FEATURE [App::DocumentObjectGroupPython] G4_1_2_DICHLOROETHANE  label="G4_1.2-DICHLOROETHANE"  # scripted group (container) (typed FeaturePython)
  Dunit = g/cm3
  Dvalue = 1.2351
  Group = -> [C_element034,H_element031,Cl_element009]
  conduct = 2
  density = 1
  expand = 3
  formula = G4_1.2-DICHLOROETHANE
  name = G4_1.2-DICHLOROETHANE
  specific = 4
FEATURE [App::DocumentObjectGroupPython] C_element035  label="C_element : 019"  # scripted group (container) (typed FeaturePython)
  n = 4
  ref = C_element
FEATURE [App::DocumentObjectGroupPython] H_element032  label="H_element : 015"  # scripted group (container) (typed FeaturePython)
  n = 10
  ref = H_element
FEATURE [App::DocumentObjectGroupPython] O_element032  label="O_element : 015"  # scripted group (container) (typed FeaturePython)
  n = 1
  ref = O_element
FEATURE [App::DocumentObjectGroupPython] G4_DIETHYL_ETHER  # scripted group (container) (typed FeaturePython)
  Dunit = g/cm3
  Dvalue = 0.71378
  Group = -> [C_element035,H_element032,O_element032]
  conduct = 2
  density = 1
  expand = 3
  formula = G4_DIETHYL_ETHER
  name = G4_DIETHYL_ETHER
  specific = 4
FEATURE [App::DocumentObjectGroupPython] C_element036  label="C_element : 020"  # scripted group (container) (typed FeaturePython)
  n = 3
  ref = C_element
FEATURE [App::DocumentObjectGroupPython] H_element033  label="H_element : 016"  # scripted group (container) (typed FeaturePython)
  n = 7
  ref = H_element
FEATURE [App::DocumentObjectGroupPython] N_element015  label="N_element : 008"  # scripted group (container) (typed FeaturePython)
  n = 1
  ref = N_element
FEATURE [App::DocumentObjectGroupPython] O_element033  label="O_element : 016"  # scripted group (container) (typed FeaturePython)
  n = 1
  ref = O_element
FEATURE [App::DocumentObjectGroupPython] G4_N_N_DIMETHYL_FORMAMIDE  label="G4_N.N-DIMETHYL_FORMAMIDE"  # scripted group (container) (typed FeaturePython)
  Dunit = g/cm3
  Dvalue = 0.9487
  Group = -> [C_element036,H_element033,N_element015,O_element033]
  conduct = 2
  density = 1
  expand = 3
  formula = G4_N.N-DIMETHYL_FORMAMIDE
  name = G4_N.N-DIMETHYL_FORMAMIDE
  specific = 4
FEATURE [App::DocumentObjectGroupPython] C_element037  label="C_element : 021"  # scripted group (container) (typed FeaturePython)
  n = 2
  ref = C_element
FEATURE [App::DocumentObjectGroupPython] H_element034  label="H_element : 017"  # scripted group (container) (typed FeaturePython)
  n = 6
  ref = H_element
FEATURE [App::DocumentObjectGroupPython] O_element034  label="O_element : 017"  # scripted group (container) (typed FeaturePython)
  n = 1
  ref = O_element
FEATURE [App::DocumentObjectGroupPython] S_element009  label="S_element : 003"  # scripted group (container) (typed FeaturePython)
  n = 1
  ref = S_element
FEATURE [App::DocumentObjectGroupPython] G4_DIMETHYL_SULFOXIDE  # scripted group (container) (typed FeaturePython)
  Dunit = g/cm3
  Dvalue = 1.1014
  Group = -> [C_element037,H_element034,O_element034,S_element009]
  conduct = 2
  density = 1
  expand = 3
  formula = G4_DIMETHYL_SULFOXIDE
  name = G4_DIMETHYL_SULFOXIDE
  specific = 4
FEATURE [App::DocumentObjectGroupPython] C_element038  label="C_element : 022"  # scripted group (container) (typed FeaturePython)
  n = 2
  ref = C_element
FEATURE [App::DocumentObjectGroupPython] H_element035  label="H_element : 018"  # scripted group (container) (typed FeaturePython)
  n = 6
  ref = H_element
FEATURE [App::DocumentObjectGroupPython] G4_ETHANE  # scripted group (container) (typed FeaturePython)
  Dunit = g/cm3
  Dvalue = 0.00125324
  Group = -> [C_element038,H_element035]
  conduct = 2
  density = 1
  expand = 3
  formula = G4_ETHANE
  name = G4_ETHANE
  specific = 4
FEATURE [App::DocumentObjectGroupPython] C_element039  label="C_element : 023"  # scripted group (container) (typed FeaturePython)
  n = 2
  ref = C_element
FEATURE [App::DocumentObjectGroupPython] H_element036  label="H_element : 019"  # scripted group (container) (typed FeaturePython)
  n = 6
  ref = H_element
FEATURE [App::DocumentObjectGroupPython] O_element035  label="O_element : 018"  # scripted group (container) (typed FeaturePython)
  n = 1
  ref = O_element
FEATURE [App::DocumentObjectGroupPython] G4_ETHYL_ALCOHOL  # scripted group (container) (typed FeaturePython)
  Dunit = g/cm3
  Dvalue = 0.7893
  Group = -> [C_element039,H_element036,O_element035]
  conduct = 2
  density = 1
  expand = 3
  formula = G4_ETHYL_ALCOHOL
  name = G4_ETHYL_ALCOHOL
  specific = 4
FEATURE [App::DocumentObjectGroupPython] H_element037  label="H_element : 0.090"  # scripted group (container) (typed FeaturePython)
  n = 0.090027
FEATURE [App::DocumentObjectGroupPython] C_element040  label="C_element : 0.585"  # scripted group (container) (typed FeaturePython)
  n = 0.585182
FEATURE [App::DocumentObjectGroupPython] O_element036  label="O_element : 0.325"  # scripted group (container) (typed FeaturePython)
  n = 0.324791
FEATURE [App::DocumentObjectGroupPython] G4_ETHYL_CELLULOSE  # scripted group (container) (typed FeaturePython)
  Dunit = g/cm3
  Dvalue = 1.13
  Group = -> [H_element037,C_element040,O_element036]
  conduct = 2
  density = 1
  expand = 3
  formula = G4_ETHYL_CELLULOSE
  name = G4_ETHYL_CELLULOSE
  specific = 4
FEATURE [App::DocumentObjectGroupPython] C_element041  label="C_element : 024"  # scripted group (container) (typed FeaturePython)
  n = 2
  ref = C_element
FEATURE [App::DocumentObjectGroupPython] H_element038  label="H_element : 020"  # scripted group (container) (typed FeaturePython)
  n = 4
  ref = H_element
FEATURE [App::DocumentObjectGroupPython] G4_ETHYLENE  # scripted group (container) (typed FeaturePython)
  Dunit = g/cm3
  Dvalue = 0.00117497
  Group = -> [C_element041,H_element038]
  conduct = 2
  density = 1
  expand = 3
  formula = G4_ETHYLENE
  name = G4_ETHYLENE
  specific = 4
FEATURE [App::DocumentObjectGroupPython] H_element039  label="H_element : 0.096"  # scripted group (container) (typed FeaturePython)
  n = 0.096
FEATURE [App::DocumentObjectGroupPython] C_element042  label="C_element : 0.195"  # scripted group (container) (typed FeaturePython)
  n = 0.195
FEATURE [App::DocumentObjectGroupPython] N_element016  label="N_element : 0.057"  # scripted group (container) (typed FeaturePython)
  n = 0.057
FEATURE [App::DocumentObjectGroupPython] O_element037  label="O_element : 0.646"  # scripted group (container) (typed FeaturePython)
  n = 0.646
FEATURE [App::DocumentObjectGroupPython] Na_element006  label="Na_element : 0.017"  # scripted group (container) (typed FeaturePython)
  n = 0.001
FEATURE [App::DocumentObjectGroupPython] P_element005  label="P_element : 0.104"  # scripted group (container) (typed FeaturePython)
  n = 0.001
FEATURE [App::DocumentObjectGroupPython] S_element010  label="S_element : 0.016"  # scripted group (container) (typed FeaturePython)
  n = 0.003
FEATURE [App::DocumentObjectGroupPython] Cl_element010  label="Cl_element : 0.005"  # scripted group (container) (typed FeaturePython)
  n = 0.001
FEATURE [App::DocumentObjectGroupPython] G4_EYE_LENS_ICRP  # scripted group (container) (typed FeaturePython)
  Dunit = g/cm3
  Dvalue = 1.07
  Group = -> [H_element039,C_element042,N_element016,O_element037,Na_element006,P_element005,S_element010,Cl_element010]
  conduct = 2
  density = 1
  expand = 3
  formula = G4_EYE_LENS_ICRP
  name = G4_EYE_LENS_ICRP
  specific = 4
FEATURE [App::DocumentObjectGroupPython] Fe_element003  label="Fe_element : 2"  # scripted group (container) (typed FeaturePython)
  n = 2
  ref = Fe_element
FEATURE [App::DocumentObjectGroupPython] O_element038  label="O_element : 019"  # scripted group (container) (typed FeaturePython)
  n = 3
  ref = O_element
FEATURE [App::DocumentObjectGroupPython] G4_FERRIC_OXIDE  # scripted group (container) (typed FeaturePython)
  Dunit = g/cm3
  Dvalue = 5.2
  Group = -> [Fe_element003,O_element038]
  conduct = 2
  density = 1
  expand = 3
  formula = G4_FERRIC_OXIDE
  name = G4_FERRIC_OXIDE
  specific = 4
FEATURE [App::DocumentObjectGroupPython] Fe_element004  label="Fe_element : 1"  # scripted group (container) (typed FeaturePython)
  n = 1
  ref = Fe_element
FEATURE [App::DocumentObjectGroupPython] B_element003  label="B_element : 1"  # scripted group (container) (typed FeaturePython)
  n = 1
  ref = B_element
FEATURE [App::DocumentObjectGroupPython] G4_FERROBORIDE  # scripted group (container) (typed FeaturePython)
  Dunit = g/cm3
  Dvalue = 7.15
  Group = -> [Fe_element004,B_element003]
  conduct = 2
  density = 1
  expand = 3
  formula = G4_FERROBORIDE
  name = G4_FERROBORIDE
  specific = 4
FEATURE [App::DocumentObjectGroupPython] Fe_element005  label="Fe_element : 003"  # scripted group (container) (typed FeaturePython)
  n = 1
  ref = Fe_element
FEATURE [App::DocumentObjectGroupPython] O_element039  label="O_element : 020"  # scripted group (container) (typed FeaturePython)
  n = 1
  ref = O_element
FEATURE [App::DocumentObjectGroupPython] G4_FERROUS_OXIDE  # scripted group (container) (typed FeaturePython)
  Dunit = g/cm3
  Dvalue = 5.7
  Group = -> [Fe_element005,O_element039]
  conduct = 2
  density = 1
  expand = 3
  formula = G4_FERROUS_OXIDE
  name = G4_FERROUS_OXIDE
  specific = 4
FEATURE [App::DocumentObjectGroupPython] H_element040  label="H_element : 0.115"  # scripted group (container) (typed FeaturePython)
  n = 0.108259
FEATURE [App::DocumentObjectGroupPython] N_element017  label="N_element : 0.000"  # scripted group (container) (typed FeaturePython)
  n = 2.7e-05
FEATURE [App::DocumentObjectGroupPython] O_element040  label="O_element : 0.879"  # scripted group (container) (typed FeaturePython)
  n = 0.878636
FEATURE [App::DocumentObjectGroupPython] Na_element007  label="Na_element : 0.000"  # scripted group (container) (typed FeaturePython)
  n = 2.2e-05
FEATURE [App::DocumentObjectGroupPython] S_element011  label="S_element : 0.013"  # scripted group (container) (typed FeaturePython)
  n = 0.012968
FEATURE [App::DocumentObjectGroupPython] Cl_element011  label="Cl_element : 0.000"  # scripted group (container) (typed FeaturePython)
  n = 3.4e-05
FEATURE [App::DocumentObjectGroupPython] Fe_element006  label="Fe_element : 0.000"  # scripted group (container) (typed FeaturePython)
  n = 5.4e-05
FEATURE [App::DocumentObjectGroupPython] G4_FERROUS_SULFATE  # scripted group (container) (typed FeaturePython)
  Dunit = g/cm3
  Dvalue = 1.024
  Group = -> [H_element040,N_element017,O_element040,Na_element007,S_element011,Cl_element011,Fe_element006]
  conduct = 2
  density = 1
  expand = 3
  formula = G4_FERROUS_SULFATE
  name = G4_FERROUS_SULFATE
  specific = 4
FEATURE [App::DocumentObjectGroupPython] C_element043  label="C_element : 0.099"  # scripted group (container) (typed FeaturePython)
  n = 0.099335
FEATURE [App::DocumentObjectGroupPython] F_element007  label="F_element : 0.314"  # scripted group (container) (typed FeaturePython)
  n = 0.314247
FEATURE [App::DocumentObjectGroupPython] Cl_element012  label="Cl_element : 0.586"  # scripted group (container) (typed FeaturePython)
  n = 0.586418
FEATURE [App::DocumentObjectGroupPython] G4_FREON_12  label="G4_FREON-12"  # scripted group (container) (typed FeaturePython)
  Dunit = g/cm3
  Dvalue = 1.12
  Group = -> [C_element043,F_element007,Cl_element012]
  conduct = 2
  density = 1
  expand = 3
  formula = G4_FREON-12
  name = G4_FREON-12
  specific = 4
FEATURE [App::DocumentObjectGroupPython] C_element044  label="C_element : 0.057"  # scripted group (container) (typed FeaturePython)
  n = 0.057245
FEATURE [App::DocumentObjectGroupPython] F_element008  label="F_element : 0.181"  # scripted group (container) (typed FeaturePython)
  n = 0.181096
FEATURE [App::DocumentObjectGroupPython] Br_element001  label="Br_element : 0.762"  # scripted group (container) (typed FeaturePython)
  n = 0.761659
FEATURE [App::DocumentObjectGroupPython] G4_FREON_12B2  label="G4_FREON-12B2"  # scripted group (container) (typed FeaturePython)
  Dunit = g/cm3
  Dvalue = 1.8
  Group = -> [C_element044,F_element008,Br_element001]
  conduct = 2
  density = 1
  expand = 3
  formula = G4_FREON-12B2
  name = G4_FREON-12B2
  specific = 4
FEATURE [App::DocumentObjectGroupPython] C_element045  label="C_element : 0.115"  # scripted group (container) (typed FeaturePython)
  n = 0.114983
FEATURE [App::DocumentObjectGroupPython] F_element009  label="F_element : 0.546"  # scripted group (container) (typed FeaturePython)
  n = 0.545621
FEATURE [App::DocumentObjectGroupPython] Cl_element013  label="Cl_element : 0.339"  # scripted group (container) (typed FeaturePython)
  n = 0.339396
FEATURE [App::DocumentObjectGroupPython] G4_FREON_13  label="G4_FREON-13"  # scripted group (container) (typed FeaturePython)
  Dunit = g/cm3
  Dvalue = 0.95
  Group = -> [C_element045,F_element009,Cl_element013]
  conduct = 2
  density = 1
  expand = 3
  formula = G4_FREON-13
  name = G4_FREON-13
  specific = 4
FEATURE [App::DocumentObjectGroupPython] C_element046  label="C_element : 025"  # scripted group (container) (typed FeaturePython)
  n = 1
  ref = C_element
FEATURE [App::DocumentObjectGroupPython] F_element010  label="F_element : 3"  # scripted group (container) (typed FeaturePython)
  n = 3
  ref = F_element
FEATURE [App::DocumentObjectGroupPython] Br_element002  label="Br_element : 1"  # scripted group (container) (typed FeaturePython)
  n = 1
  ref = Br_element
FEATURE [App::DocumentObjectGroupPython] G4_FREON_13B1  label="G4_FREON-13B1"  # scripted group (container) (typed FeaturePython)
  Dunit = g/cm3
  Dvalue = 1.5
  Group = -> [C_element046,F_element010,Br_element002]
  conduct = 2
  density = 1
  expand = 3
  formula = G4_FREON-13B1
  name = G4_FREON-13B1
  specific = 4
FEATURE [App::DocumentObjectGroupPython] C_element047  label="C_element : 0.061"  # scripted group (container) (typed FeaturePython)
  n = 0.061309
FEATURE [App::DocumentObjectGroupPython] F_element011  label="F_element : 0.291"  # scripted group (container) (typed FeaturePython)
  n = 0.290924
FEATURE [App::DocumentObjectGroupPython] I_element002  label="I_element : 0.648"  # scripted group (container) (typed FeaturePython)
  n = 0.647767
FEATURE [App::DocumentObjectGroupPython] G4_FREON_13I1  label="G4_FREON-13I1"  # scripted group (container) (typed FeaturePython)
  Dunit = g/cm3
  Dvalue = 1.8
  Group = -> [C_element047,F_element011,I_element002]
  conduct = 2
  density = 1
  expand = 3
  formula = G4_FREON-13I1
  name = G4_FREON-13I1
  specific = 4
FEATURE [App::DocumentObjectGroupPython] Gd_element001  label="Gd_element : 2"  # scripted group (container) (typed FeaturePython)
  n = 2
  ref = Gd_element
FEATURE [App::DocumentObjectGroupPython] O_element041  label="O_element : 021"  # scripted group (container) (typed FeaturePython)
  n = 2
  ref = O_element
FEATURE [App::DocumentObjectGroupPython] S_element012  label="S_element : 004"  # scripted group (container) (typed FeaturePython)
  n = 1
  ref = S_element
FEATURE [App::DocumentObjectGroupPython] G4_GADOLINIUM_OXYSULFIDE  # scripted group (container) (typed FeaturePython)
  Dunit = g/cm3
  Dvalue = 7.44
  Group = -> [Gd_element001,O_element041,S_element012]
  conduct = 2
  density = 1
  expand = 3
  formula = G4_GADOLINIUM_OXYSULFIDE
  name = G4_GADOLINIUM_OXYSULFIDE
  specific = 4
FEATURE [App::DocumentObjectGroupPython] Ga_element001  label="Ga_element : 1"  # scripted group (container) (typed FeaturePython)
  n = 1
  ref = Ga_element
FEATURE [App::DocumentObjectGroupPython] As_element001  label="As_element : 1"  # scripted group (container) (typed FeaturePython)
  n = 1
  ref = As_element
FEATURE [App::DocumentObjectGroupPython] G4_GALLIUM_ARSENIDE  # scripted group (container) (typed FeaturePython)
  Dunit = g/cm3
  Dvalue = 5.31
  Group = -> [Ga_element001,As_element001]
  conduct = 2
  density = 1
  expand = 3
  formula = G4_GALLIUM_ARSENIDE
  name = G4_GALLIUM_ARSENIDE
  specific = 4
FEATURE [App::DocumentObjectGroupPython] H_element041  label="H_element : 0.081"  # scripted group (container) (typed FeaturePython)
  n = 0.08118
FEATURE [App::DocumentObjectGroupPython] C_element048  label="C_element : 0.416"  # scripted group (container) (typed FeaturePython)
  n = 0.41606
FEATURE [App::DocumentObjectGroupPython] N_element018  label="N_element : 0.111"  # scripted group (container) (typed FeaturePython)
  n = 0.11124
FEATURE [App::DocumentObjectGroupPython] O_element042  label="O_element : 0.381"  # scripted group (container) (typed FeaturePython)
  n = 0.38064
FEATURE [App::DocumentObjectGroupPython] S_element013  label="S_element : 0.011"  # scripted group (container) (typed FeaturePython)
  n = 0.01088
FEATURE [App::DocumentObjectGroupPython] G4_GEL_PHOTO_EMULSION  # scripted group (container) (typed FeaturePython)
  Dunit = g/cm3
  Dvalue = 1.2914
  Group = -> [H_element041,C_element048,N_element018,O_element042,S_element013]
  conduct = 2
  density = 1
  expand = 3
  formula = G4_GEL_PHOTO_EMULSION
  name = G4_GEL_PHOTO_EMULSION
  specific = 4
FEATURE [App::DocumentObjectGroupPython] B_element004  label="B_element : 0.040"  # scripted group (container) (typed FeaturePython)
  n = 0.0400639
FEATURE [App::DocumentObjectGroupPython] O_element043  label="O_element : 0.540"  # scripted group (container) (typed FeaturePython)
  n = 0.539561
FEATURE [App::DocumentObjectGroupPython] Na_element008  label="Na_element : 0.028"  # scripted group (container) (typed FeaturePython)
  n = 0.0281909
FEATURE [App::DocumentObjectGroupPython] Al_element003  label="Al_element : 0.012"  # scripted group (container) (typed FeaturePython)
  n = 0.011644
FEATURE [App::DocumentObjectGroupPython] Si_element003  label="Si_element : 0.377"  # scripted group (container) (typed FeaturePython)
  n = 0.377219
FEATURE [App::DocumentObjectGroupPython] K_element004  label="K_element : 0.014"  # scripted group (container) (typed FeaturePython)
  n = 0.00332099
FEATURE [App::DocumentObjectGroupPython] G4_Pyrex_Glass  # scripted group (container) (typed FeaturePython)
  Dunit = g/cm3
  Dvalue = 2.23
  Group = -> [B_element004,O_element043,Na_element008,Al_element003,Si_element003,K_element004]
  conduct = 2
  density = 1
  expand = 3
  formula = G4_Pyrex_Glass
  name = G4_Pyrex_Glass
  specific = 4
FEATURE [App::DocumentObjectGroupPython] O_element044  label="O_element : 0.156"  # scripted group (container) (typed FeaturePython)
  n = 0.156453
FEATURE [App::DocumentObjectGroupPython] Si_element004  label="Si_element : 0.081"  # scripted group (container) (typed FeaturePython)
  n = 0.080866
FEATURE [App::DocumentObjectGroupPython] Ti_element001  label="Ti_element : 0.008"  # scripted group (container) (typed FeaturePython)
  n = 0.008092
FEATURE [App::DocumentObjectGroupPython] As_element002  label="As_element : 0.003"  # scripted group (container) (typed FeaturePython)
  n = 0.002651
FEATURE [App::DocumentObjectGroupPython] Pb_element001  label="Pb_element : 0.752"  # scripted group (container) (typed FeaturePython)
  n = 0.751938
FEATURE [App::DocumentObjectGroupPython] G4_GLASS_LEAD  # scripted group (container) (typed FeaturePython)
  Dunit = g/cm3
  Dvalue = 6.22
  Group = -> [O_element044,Si_element004,Ti_element001,As_element002,Pb_element001]
  conduct = 2
  density = 1
  expand = 3
  formula = G4_GLASS_LEAD
  name = G4_GLASS_LEAD
  specific = 4
FEATURE [App::DocumentObjectGroupPython] O_element045  label="O_element : 0.460"  # scripted group (container) (typed FeaturePython)
  n = 0.4598
FEATURE [App::DocumentObjectGroupPython] Na_element009  label="Na_element : 0.096"  # scripted group (container) (typed FeaturePython)
  n = 0.0964411
FEATURE [App::DocumentObjectGroupPython] Si_element005  label="Si_element : 0.378"  # scripted group (container) (typed FeaturePython)
  n = 0.336553
FEATURE [App::DocumentObjectGroupPython] Ca_element011  label="Ca_element : 0.107"  # scripted group (container) (typed FeaturePython)
  n = 0.107205
FEATURE [App::DocumentObjectGroupPython] G4_GLASS_PLATE  # scripted group (container) (typed FeaturePython)
  Dunit = g/cm3
  Dvalue = 2.4
  Group = -> [O_element045,Na_element009,Si_element005,Ca_element011]
  conduct = 2
  density = 1
  expand = 3
  formula = G4_GLASS_PLATE
  name = G4_GLASS_PLATE
  specific = 4
FEATURE [App::DocumentObjectGroupPython] C_element049  label="C_element : 026"  # scripted group (container) (typed FeaturePython)
  n = 5
  ref = C_element
FEATURE [App::DocumentObjectGroupPython] H_element042  label="H_element : 021"  # scripted group (container) (typed FeaturePython)
  n = 10
  ref = H_element
FEATURE [App::DocumentObjectGroupPython] N_element019  label="N_element : 2"  # scripted group (container) (typed FeaturePython)
  n = 2
  ref = N_element
FEATURE [App::DocumentObjectGroupPython] O_element046  label="O_element : 022"  # scripted group (container) (typed FeaturePython)
  n = 3
  ref = O_element
FEATURE [App::DocumentObjectGroupPython] G4_GLUTAMINE  # scripted group (container) (typed FeaturePython)
  Dunit = g/cm3
  Dvalue = 1.46
  Group = -> [C_element049,H_element042,N_element019,O_element046]
  conduct = 2
  density = 1
  expand = 3
  formula = G4_GLUTAMINE
  name = G4_GLUTAMINE
  specific = 4
FEATURE [App::DocumentObjectGroupPython] C_element050  label="C_element : 027"  # scripted group (container) (typed FeaturePython)
  n = 3
  ref = C_element
FEATURE [App::DocumentObjectGroupPython] H_element043  label="H_element : 022"  # scripted group (container) (typed FeaturePython)
  n = 8
  ref = H_element
FEATURE [App::DocumentObjectGroupPython] O_element047  label="O_element : 023"  # scripted group (container) (typed FeaturePython)
  n = 3
  ref = O_element
FEATURE [App::DocumentObjectGroupPython] G4_GLYCEROL  # scripted group (container) (typed FeaturePython)
  Dunit = g/cm3
  Dvalue = 1.2613
  Group = -> [C_element050,H_element043,O_element047]
  conduct = 2
  density = 1
  expand = 3
  formula = G4_GLYCEROL
  name = G4_GLYCEROL
  specific = 4
FEATURE [App::DocumentObjectGroupPython] C_element051  label="C_element : 028"  # scripted group (container) (typed FeaturePython)
  n = 5
  ref = C_element
FEATURE [App::DocumentObjectGroupPython] H_element044  label="H_element : 023"  # scripted group (container) (typed FeaturePython)
  n = 5
  ref = H_element
FEATURE [App::DocumentObjectGroupPython] N_element020  label="N_element : 009"  # scripted group (container) (typed FeaturePython)
  n = 5
  ref = N_element
FEATURE [App::DocumentObjectGroupPython] O_element048  label="O_element : 024"  # scripted group (container) (typed FeaturePython)
  n = 1
  ref = O_element
FEATURE [App::DocumentObjectGroupPython] G4_GUANINE  # scripted group (container) (typed FeaturePython)
  Dunit = g/cm3
  Dvalue = 2.2
  Group = -> [C_element051,H_element044,N_element020,O_element048]
  conduct = 2
  density = 1
  expand = 3
  formula = G4_GUANINE
  name = G4_GUANINE
  specific = 4
FEATURE [App::DocumentObjectGroupPython] Ca_element012  label="Ca_element : 006"  # scripted group (container) (typed FeaturePython)
  n = 1
  ref = Ca_element
FEATURE [App::DocumentObjectGroupPython] S_element014  label="S_element : 005"  # scripted group (container) (typed FeaturePython)
  n = 1
  ref = S_element
FEATURE [App::DocumentObjectGroupPython] O_element049  label="O_element : 6"  # scripted group (container) (typed FeaturePython)
  n = 6
  ref = O_element
FEATURE [App::DocumentObjectGroupPython] H_element045  label="H_element : 024"  # scripted group (container) (typed FeaturePython)
  n = 4
  ref = H_element
FEATURE [App::DocumentObjectGroupPython] G4_GYPSUM  # scripted group (container) (typed FeaturePython)
  Dunit = g/cm3
  Dvalue = 2.32
  Group = -> [Ca_element012,S_element014,O_element049,H_element045]
  conduct = 2
  density = 1
  expand = 3
  formula = G4_GYPSUM
  name = G4_GYPSUM
  specific = 4
FEATURE [App::DocumentObjectGroupPython] C_element052  label="C_element : 7"  # scripted group (container) (typed FeaturePython)
  n = 7
  ref = C_element
FEATURE [App::DocumentObjectGroupPython] H_element046  label="H_element : 16"  # scripted group (container) (typed FeaturePython)
  n = 16
  ref = H_element
FEATURE [App::DocumentObjectGroupPython] G4_N_HEPTANE  label="G4_N-HEPTANE"  # scripted group (container) (typed FeaturePython)
  Dunit = g/cm3
  Dvalue = 0.68376
  Group = -> [C_element052,H_element046]
  conduct = 2
  density = 1
  expand = 3
  formula = G4_N-HEPTANE
  name = G4_N-HEPTANE
  specific = 4
FEATURE [App::DocumentObjectGroupPython] C_element053  label="C_element : 029"  # scripted group (container) (typed FeaturePython)
  n = 6
  ref = C_element
FEATURE [App::DocumentObjectGroupPython] H_element047  label="H_element : 14"  # scripted group (container) (typed FeaturePython)
  n = 14
  ref = H_element
FEATURE [App::DocumentObjectGroupPython] G4_N_HEXANE  label="G4_N-HEXANE"  # scripted group (container) (typed FeaturePython)
  Dunit = g/cm3
  Dvalue = 0.6603
  Group = -> [C_element053,H_element047]
  conduct = 2
  density = 1
  expand = 3
  formula = G4_N-HEXANE
  name = G4_N-HEXANE
  specific = 4
FEATURE [App::DocumentObjectGroupPython] C_element054  label="C_element : 22"  # scripted group (container) (typed FeaturePython)
  n = 22
  ref = C_element
FEATURE [App::DocumentObjectGroupPython] H_element048  label="H_element : 025"  # scripted group (container) (typed FeaturePython)
  n = 10
  ref = H_element
FEATURE [App::DocumentObjectGroupPython] N_element021  label="N_element : 010"  # scripted group (container) (typed FeaturePython)
  n = 2
  ref = N_element
FEATURE [App::DocumentObjectGroupPython] O_element050  label="O_element : 025"  # scripted group (container) (typed FeaturePython)
  n = 5
  ref = O_element
FEATURE [App::DocumentObjectGroupPython] G4_KAPTON  # scripted group (container) (typed FeaturePython)
  Dunit = g/cm3
  Dvalue = 1.42
  Group = -> [C_element054,H_element048,N_element021,O_element050]
  conduct = 2
  density = 1
  expand = 3
  formula = G4_KAPTON
  name = G4_KAPTON
  specific = 4
FEATURE [App::DocumentObjectGroupPython] La_element001  label="La_element : 1"  # scripted group (container) (typed FeaturePython)
  n = 1
  ref = La_element
FEATURE [App::DocumentObjectGroupPython] Br_element003  label="Br_element : 002"  # scripted group (container) (typed FeaturePython)
  n = 1
  ref = Br_element
FEATURE [App::DocumentObjectGroupPython] O_element051  label="O_element : 026"  # scripted group (container) (typed FeaturePython)
  n = 1
  ref = O_element
FEATURE [App::DocumentObjectGroupPython] G4_LANTHANUM_OXYBROMIDE  # scripted group (container) (typed FeaturePython)
  Dunit = g/cm3
  Dvalue = 6.28
  Group = -> [La_element001,Br_element003,O_element051]
  conduct = 2
  density = 1
  expand = 3
  formula = G4_LANTHANUM_OXYBROMIDE
  name = G4_LANTHANUM_OXYBROMIDE
  specific = 4
FEATURE [App::DocumentObjectGroupPython] La_element002  label="La_element : 2"  # scripted group (container) (typed FeaturePython)
  n = 2
  ref = La_element
FEATURE [App::DocumentObjectGroupPython] O_element052  label="O_element : 027"  # scripted group (container) (typed FeaturePython)
  n = 2
  ref = O_element
FEATURE [App::DocumentObjectGroupPython] S_element015  label="S_element : 006"  # scripted group (container) (typed FeaturePython)
  n = 1
  ref = S_element
FEATURE [App::DocumentObjectGroupPython] G4_LANTHANUM_OXYSULFIDE  # scripted group (container) (typed FeaturePython)
  Dunit = g/cm3
  Dvalue = 5.86
  Group = -> [La_element002,O_element052,S_element015]
  conduct = 2
  density = 1
  expand = 3
  formula = G4_LANTHANUM_OXYSULFIDE
  name = G4_LANTHANUM_OXYSULFIDE
  specific = 4
FEATURE [App::DocumentObjectGroupPython] O_element053  label="O_element : 0.072"  # scripted group (container) (typed FeaturePython)
  n = 0.071682
FEATURE [App::DocumentObjectGroupPython] Pb_element002  label="Pb_element : 0.928"  # scripted group (container) (typed FeaturePython)
  n = 0.928318
FEATURE [App::DocumentObjectGroupPython] G4_LEAD_OXIDE  # scripted group (container) (typed FeaturePython)
  Dunit = g/cm3
  Dvalue = 9.53
  Group = -> [O_element053,Pb_element002]
  conduct = 2
  density = 1
  expand = 3
  formula = G4_LEAD_OXIDE
  name = G4_LEAD_OXIDE
  specific = 4
FEATURE [App::DocumentObjectGroupPython] Li_element001  label="Li_element : 1"  # scripted group (container) (typed FeaturePython)
  n = 1
  ref = Li_element
FEATURE [App::DocumentObjectGroupPython] N_element022  label="N_element : 011"  # scripted group (container) (typed FeaturePython)
  n = 1
  ref = N_element
FEATURE [App::DocumentObjectGroupPython] H_element049  label="H_element : 026"  # scripted group (container) (typed FeaturePython)
  n = 2
  ref = H_element
FEATURE [App::DocumentObjectGroupPython] G4_LITHIUM_AMIDE  # scripted group (container) (typed FeaturePython)
  Dunit = g/cm3
  Dvalue = 1.178
  Group = -> [Li_element001,N_element022,H_element049]
  conduct = 2
  density = 1
  expand = 3
  formula = G4_LITHIUM_AMIDE
  name = G4_LITHIUM_AMIDE
  specific = 4
FEATURE [App::DocumentObjectGroupPython] Li_element002  label="Li_element : 2"  # scripted group (container) (typed FeaturePython)
  n = 2
  ref = Li_element
FEATURE [App::DocumentObjectGroupPython] C_element055  label="C_element : 030"  # scripted group (container) (typed FeaturePython)
  n = 1
  ref = C_element
FEATURE [App::DocumentObjectGroupPython] O_element054  label="O_element : 028"  # scripted group (container) (typed FeaturePython)
  n = 3
  ref = O_element
FEATURE [App::DocumentObjectGroupPython] G4_LITHIUM_CARBONATE  # scripted group (container) (typed FeaturePython)
  Dunit = g/cm3
  Dvalue = 2.11
  Group = -> [Li_element002,C_element055,O_element054]
  conduct = 2
  density = 1
  expand = 3
  formula = G4_LITHIUM_CARBONATE
  name = G4_LITHIUM_CARBONATE
  specific = 4
FEATURE [App::DocumentObjectGroupPython] Li_element003  label="Li_element : 003"  # scripted group (container) (typed FeaturePython)
  n = 1
  ref = Li_element
FEATURE [App::DocumentObjectGroupPython] F_element012  label="F_element : 004"  # scripted group (container) (typed FeaturePython)
  n = 1
  ref = F_element
FEATURE [App::DocumentObjectGroupPython] G4_LITHIUM_FLUORIDE  # scripted group (container) (typed FeaturePython)
  Dunit = g/cm3
  Dvalue = 2.635
  Group = -> [Li_element003,F_element012]
  conduct = 2
  density = 1
  expand = 3
  formula = G4_LITHIUM_FLUORIDE
  name = G4_LITHIUM_FLUORIDE
  specific = 4
FEATURE [App::DocumentObjectGroupPython] Li_element004  label="Li_element : 004"  # scripted group (container) (typed FeaturePython)
  n = 1
  ref = Li_element
FEATURE [App::DocumentObjectGroupPython] H_element050  label="H_element : 027"  # scripted group (container) (typed FeaturePython)
  n = 1
  ref = H_element
FEATURE [App::DocumentObjectGroupPython] G4_LITHIUM_HYDRIDE  # scripted group (container) (typed FeaturePython)
  Dunit = g/cm3
  Dvalue = 0.82
  Group = -> [Li_element004,H_element050]
  conduct = 2
  density = 1
  expand = 3
  formula = G4_LITHIUM_HYDRIDE
  name = G4_LITHIUM_HYDRIDE
  specific = 4
FEATURE [App::DocumentObjectGroupPython] Li_element005  label="Li_element : 005"  # scripted group (container) (typed FeaturePython)
  n = 1
  ref = Li_element
FEATURE [App::DocumentObjectGroupPython] I_element003  label="I_element : 002"  # scripted group (container) (typed FeaturePython)
  n = 1
  ref = I_element
FEATURE [App::DocumentObjectGroupPython] G4_LITHIUM_IODIDE  # scripted group (container) (typed FeaturePython)
  Dunit = g/cm3
  Dvalue = 3.494
  Group = -> [Li_element005,I_element003]
  conduct = 2
  density = 1
  expand = 3
  formula = G4_LITHIUM_IODIDE
  name = G4_LITHIUM_IODIDE
  specific = 4
FEATURE [App::DocumentObjectGroupPython] Li_element006  label="Li_element : 006"  # scripted group (container) (typed FeaturePython)
  n = 2
  ref = Li_element
FEATURE [App::DocumentObjectGroupPython] O_element055  label="O_element : 029"  # scripted group (container) (typed FeaturePython)
  n = 1
  ref = O_element
FEATURE [App::DocumentObjectGroupPython] G4_LITHIUM_OXIDE  # scripted group (container) (typed FeaturePython)
  Dunit = g/cm3
  Dvalue = 2.013
  Group = -> [Li_element006,O_element055]
  conduct = 2
  density = 1
  expand = 3
  formula = G4_LITHIUM_OXIDE
  name = G4_LITHIUM_OXIDE
  specific = 4
FEATURE [App::DocumentObjectGroupPython] Li_element007  label="Li_element : 007"  # scripted group (container) (typed FeaturePython)
  n = 2
  ref = Li_element
FEATURE [App::DocumentObjectGroupPython] B_element005  label="B_element : 005"  # scripted group (container) (typed FeaturePython)
  n = 4
  ref = B_element
FEATURE [App::DocumentObjectGroupPython] O_element056  label="O_element : 7"  # scripted group (container) (typed FeaturePython)
  n = 7
  ref = O_element
FEATURE [App::DocumentObjectGroupPython] G4_LITHIUM_TETRABORATE  # scripted group (container) (typed FeaturePython)
  Dunit = g/cm3
  Dvalue = 2.44
  Group = -> [Li_element007,B_element005,O_element056]
  conduct = 2
  density = 1
  expand = 3
  formula = G4_LITHIUM_TETRABORATE
  name = G4_LITHIUM_TETRABORATE
  specific = 4
FEATURE [App::DocumentObjectGroupPython] H_element051  label="H_element : 0.105"  # scripted group (container) (typed FeaturePython)
  n = 0.105
FEATURE [App::DocumentObjectGroupPython] C_element056  label="C_element : 0.083"  # scripted group (container) (typed FeaturePython)
  n = 0.083
FEATURE [App::DocumentObjectGroupPython] N_element023  label="N_element : 0.023"  # scripted group (container) (typed FeaturePython)
  n = 0.023
FEATURE [App::DocumentObjectGroupPython] O_element057  label="O_element : 0.779"  # scripted group (container) (typed FeaturePython)
  n = 0.779
FEATURE [App::DocumentObjectGroupPython] Na_element010  label="Na_element : 0.097"  # scripted group (container) (typed FeaturePython)
  n = 0.002
FEATURE [App::DocumentObjectGroupPython] P_element006  label="P_element : 0.105"  # scripted group (container) (typed FeaturePython)
  n = 0.001
FEATURE [App::DocumentObjectGroupPython] S_element016  label="S_element : 0.017"  # scripted group (container) (typed FeaturePython)
  n = 0.002
FEATURE [App::DocumentObjectGroupPython] Cl_element014  label="Cl_element : 0.587"  # scripted group (container) (typed FeaturePython)
  n = 0.003
FEATURE [App::DocumentObjectGroupPython] K_element005  label="K_element : 0.015"  # scripted group (container) (typed FeaturePython)
  n = 0.002
FEATURE [App::DocumentObjectGroupPython] G4_LUNG_ICRP  # scripted group (container) (typed FeaturePython)
  Dunit = g/cm3
  Dvalue = 1.04
  Group = -> [H_element051,C_element056,N_element023,O_element057,Na_element010,P_element006,S_element016,Cl_element014,K_element005]
  conduct = 2
  density = 1
  expand = 3
  formula = G4_LUNG_ICRP
  name = G4_LUNG_ICRP
  specific = 4
FEATURE [App::DocumentObjectGroupPython] H_element052  label="H_element : 0.116"  # scripted group (container) (typed FeaturePython)
  n = 0.114318
FEATURE [App::DocumentObjectGroupPython] C_element057  label="C_element : 0.656"  # scripted group (container) (typed FeaturePython)
  n = 0.655824
FEATURE [App::DocumentObjectGroupPython] O_element058  label="O_element : 0.092"  # scripted group (container) (typed FeaturePython)
  n = 0.0921831
FEATURE [App::DocumentObjectGroupPython] Mg_element004  label="Mg_element : 0.135"  # scripted group (container) (typed FeaturePython)
  n = 0.134792
FEATURE [App::DocumentObjectGroupPython] Ca_element013  label="Ca_element : 0.003"  # scripted group (container) (typed FeaturePython)
  n = 0.002883
FEATURE [App::DocumentObjectGroupPython] G4_M3_WAX  # scripted group (container) (typed FeaturePython)
  Dunit = g/cm3
  Dvalue = 1.05
  Group = -> [H_element052,C_element057,O_element058,Mg_element004,Ca_element013]
  conduct = 2
  density = 1
  expand = 3
  formula = G4_M3_WAX
  name = G4_M3_WAX
  specific = 4
FEATURE [App::DocumentObjectGroupPython] Mg_element005  label="Mg_element : 1"  # scripted group (container) (typed FeaturePython)
  n = 1
  ref = Mg_element
FEATURE [App::DocumentObjectGroupPython] C_element058  label="C_element : 031"  # scripted group (container) (typed FeaturePython)
  n = 1
  ref = C_element
FEATURE [App::DocumentObjectGroupPython] O_element059  label="O_element : 030"  # scripted group (container) (typed FeaturePython)
  n = 3
  ref = O_element
FEATURE [App::DocumentObjectGroupPython] G4_MAGNESIUM_CARBONATE  # scripted group (container) (typed FeaturePython)
  Dunit = g/cm3
  Dvalue = 2.958
  Group = -> [Mg_element005,C_element058,O_element059]
  conduct = 2
  density = 1
  expand = 3
  formula = G4_MAGNESIUM_CARBONATE
  name = G4_MAGNESIUM_CARBONATE
  specific = 4
FEATURE [App::DocumentObjectGroupPython] Mg_element006  label="Mg_element : 002"  # scripted group (container) (typed FeaturePython)
  n = 1
  ref = Mg_element
FEATURE [App::DocumentObjectGroupPython] F_element013  label="F_element : 005"  # scripted group (container) (typed FeaturePython)
  n = 2
  ref = F_element
FEATURE [App::DocumentObjectGroupPython] G4_MAGNESIUM_FLUORIDE  # scripted group (container) (typed FeaturePython)
  Dunit = g/cm3
  Dvalue = 3
  Group = -> [Mg_element006,F_element013]
  conduct = 2
  density = 1
  expand = 3
  formula = G4_MAGNESIUM_FLUORIDE
  name = G4_MAGNESIUM_FLUORIDE
  specific = 4
FEATURE [App::DocumentObjectGroupPython] Mg_element007  label="Mg_element : 003"  # scripted group (container) (typed FeaturePython)
  n = 1
  ref = Mg_element
FEATURE [App::DocumentObjectGroupPython] O_element060  label="O_element : 031"  # scripted group (container) (typed FeaturePython)
  n = 1
  ref = O_element
FEATURE [App::DocumentObjectGroupPython] G4_MAGNESIUM_OXIDE  # scripted group (container) (typed FeaturePython)
  Dunit = g/cm3
  Dvalue = 3.58
  Group = -> [Mg_element007,O_element060]
  conduct = 2
  density = 1
  expand = 3
  formula = G4_MAGNESIUM_OXIDE
  name = G4_MAGNESIUM_OXIDE
  specific = 4
FEATURE [App::DocumentObjectGroupPython] Mg_element008  label="Mg_element : 004"  # scripted group (container) (typed FeaturePython)
  n = 1
  ref = Mg_element
FEATURE [App::DocumentObjectGroupPython] B_element006  label="B_element : 006"  # scripted group (container) (typed FeaturePython)
  n = 4
  ref = B_element
FEATURE [App::DocumentObjectGroupPython] O_element061  label="O_element : 032"  # scripted group (container) (typed FeaturePython)
  n = 7
  ref = O_element
FEATURE [App::DocumentObjectGroupPython] G4_MAGNESIUM_TETRABORATE  # scripted group (container) (typed FeaturePython)
  Dunit = g/cm3
  Dvalue = 2.53
  Group = -> [Mg_element008,B_element006,O_element061]
  conduct = 2
  density = 1
  expand = 3
  formula = G4_MAGNESIUM_TETRABORATE
  name = G4_MAGNESIUM_TETRABORATE
  specific = 4
FEATURE [App::DocumentObjectGroupPython] Hg_element001  label="Hg_element : 1"  # scripted group (container) (typed FeaturePython)
  n = 1
  ref = Hg_element
FEATURE [App::DocumentObjectGroupPython] I_element004  label="I_element : 2"  # scripted group (container) (typed FeaturePython)
  n = 2
  ref = I_element
FEATURE [App::DocumentObjectGroupPython] G4_MERCURIC_IODIDE  # scripted group (container) (typed FeaturePython)
  Dunit = g/cm3
  Dvalue = 6.36
  Group = -> [Hg_element001,I_element004]
  conduct = 2
  density = 1
  expand = 3
  formula = G4_MERCURIC_IODIDE
  name = G4_MERCURIC_IODIDE
  specific = 4
FEATURE [App::DocumentObjectGroupPython] C_element059  label="C_element : 032"  # scripted group (container) (typed FeaturePython)
  n = 1
  ref = C_element
FEATURE [App::DocumentObjectGroupPython] H_element053  label="H_element : 028"  # scripted group (container) (typed FeaturePython)
  n = 4
  ref = H_element
FEATURE [App::DocumentObjectGroupPython] G4_METHANE  # scripted group (container) (typed FeaturePython)
  Dunit = g/cm3
  Dvalue = 0.000667151
  Group = -> [C_element059,H_element053]
  conduct = 2
  density = 1
  expand = 3
  formula = G4_METHANE
  name = G4_METHANE
  specific = 4
FEATURE [App::DocumentObjectGroupPython] C_element060  label="C_element : 033"  # scripted group (container) (typed FeaturePython)
  n = 1
  ref = C_element
FEATURE [App::DocumentObjectGroupPython] H_element054  label="H_element : 029"  # scripted group (container) (typed FeaturePython)
  n = 4
  ref = H_element
FEATURE [App::DocumentObjectGroupPython] O_element062  label="O_element : 033"  # scripted group (container) (typed FeaturePython)
  n = 1
  ref = O_element
FEATURE [App::DocumentObjectGroupPython] G4_METHANOL  # scripted group (container) (typed FeaturePython)
  Dunit = g/cm3
  Dvalue = 0.7914
  Group = -> [C_element060,H_element054,O_element062]
  conduct = 2
  density = 1
  expand = 3
  formula = G4_METHANOL
  name = G4_METHANOL
  specific = 4
FEATURE [App::DocumentObjectGroupPython] H_element055  label="H_element : 0.134"  # scripted group (container) (typed FeaturePython)
  n = 0.13404
FEATURE [App::DocumentObjectGroupPython] C_element061  label="C_element : 0.778"  # scripted group (container) (typed FeaturePython)
  n = 0.77796
FEATURE [App::DocumentObjectGroupPython] O_element063  label="O_element : 0.035"  # scripted group (container) (typed FeaturePython)
  n = 0.03502
FEATURE [App::DocumentObjectGroupPython] Mg_element009  label="Mg_element : 0.039"  # scripted group (container) (typed FeaturePython)
  n = 0.038594
FEATURE [App::DocumentObjectGroupPython] Ti_element002  label="Ti_element : 0.014"  # scripted group (container) (typed FeaturePython)
  n = 0.014386
FEATURE [App::DocumentObjectGroupPython] G4_MIX_D_WAX  # scripted group (container) (typed FeaturePython)
  Dunit = g/cm3
  Dvalue = 0.99
  Group = -> [H_element055,C_element061,O_element063,Mg_element009,Ti_element002]
  conduct = 2
  density = 1
  expand = 3
  formula = G4_MIX_D_WAX
  name = G4_MIX_D_WAX
  specific = 4
FEATURE [App::DocumentObjectGroupPython] H_element056  label="H_element : 0.135"  # scripted group (container) (typed FeaturePython)
  n = 0.081192
FEATURE [App::DocumentObjectGroupPython] C_element062  label="C_element : 0.583"  # scripted group (container) (typed FeaturePython)
  n = 0.583442
FEATURE [App::DocumentObjectGroupPython] N_element024  label="N_element : 0.018"  # scripted group (container) (typed FeaturePython)
  n = 0.017798
FEATURE [App::DocumentObjectGroupPython] O_element064  label="O_element : 0.186"  # scripted group (container) (typed FeaturePython)
  n = 0.186381
FEATURE [App::DocumentObjectGroupPython] Mg_element010  label="Mg_element : 0.130"  # scripted group (container) (typed FeaturePython)
  n = 0.130287
FEATURE [App::DocumentObjectGroupPython] Cl_element015  label="Cl_element : 0.588"  # scripted group (container) (typed FeaturePython)
  n = 0.0009
FEATURE [App::DocumentObjectGroupPython] G4_MS20_TISSUE  # scripted group (container) (typed FeaturePython)
  Dunit = g/cm3
  Dvalue = 1
  Group = -> [H_element056,C_element062,N_element024,O_element064,Mg_element010,Cl_element015]
  conduct = 2
  density = 1
  expand = 3
  formula = G4_MS20_TISSUE
  name = G4_MS20_TISSUE
  specific = 4
FEATURE [App::DocumentObjectGroupPython] H_element057  label="H_element : 0.136"  # scripted group (container) (typed FeaturePython)
  n = 0.102
FEATURE [App::DocumentObjectGroupPython] C_element063  label="C_element : 0.143"  # scripted group (container) (typed FeaturePython)
  n = 0.143
FEATURE [App::DocumentObjectGroupPython] N_element025  label="N_element : 0.034"  # scripted group (container) (typed FeaturePython)
  n = 0.034
FEATURE [App::DocumentObjectGroupPython] O_element065  label="O_element : 0.710"  # scripted group (container) (typed FeaturePython)
  n = 0.71
FEATURE [App::DocumentObjectGroupPython] Na_element011  label="Na_element : 0.098"  # scripted group (container) (typed FeaturePython)
  n = 0.001
FEATURE [App::DocumentObjectGroupPython] P_element007  label="P_element : 0.002"  # scripted group (container) (typed FeaturePython)
  n = 0.002
FEATURE [App::DocumentObjectGroupPython] S_element017  label="S_element : 0.018"  # scripted group (container) (typed FeaturePython)
  n = 0.003
FEATURE [App::DocumentObjectGroupPython] Cl_element016  label="Cl_element : 0.589"  # scripted group (container) (typed FeaturePython)
  n = 0.001
FEATURE [App::DocumentObjectGroupPython] K_element006  label="K_element : 0.004"  # scripted group (container) (typed FeaturePython)
  n = 0.004
FEATURE [App::DocumentObjectGroupPython] G4_MUSCLE_SKELETAL_ICRP  # scripted group (container) (typed FeaturePython)
  Dunit = g/cm3
  Dvalue = 1.05
  Group = -> [H_element057,C_element063,N_element025,O_element065,Na_element011,P_element007,S_element017,Cl_element016,K_element006]
  conduct = 2
  density = 1
  expand = 3
  formula = G4_MUSCLE_SKELETAL_ICRP
  name = G4_MUSCLE_SKELETAL_ICRP
  specific = 4
FEATURE [App::DocumentObjectGroupPython] H_element058  label="H_element : 0.137"  # scripted group (container) (typed FeaturePython)
  n = 0.102102
FEATURE [App::DocumentObjectGroupPython] C_element064  label="C_element : 0.123"  # scripted group (container) (typed FeaturePython)
  n = 0.123123
FEATURE [App::DocumentObjectGroupPython] N_element026  label="N_element : 0.756"  # scripted group (container) (typed FeaturePython)
  n = 0.035035
FEATURE [App::DocumentObjectGroupPython] O_element066  label="O_element : 0.730"  # scripted group (container) (typed FeaturePython)
  n = 0.72973
FEATURE [App::DocumentObjectGroupPython] Na_element012  label="Na_element : 0.099"  # scripted group (container) (typed FeaturePython)
  n = 0.001001
FEATURE [App::DocumentObjectGroupPython] P_element008  label="P_element : 0.106"  # scripted group (container) (typed FeaturePython)
  n = 0.002002
FEATURE [App::DocumentObjectGroupPython] S_element018  label="S_element : 0.019"  # scripted group (container) (typed FeaturePython)
  n = 0.004004
FEATURE [App::DocumentObjectGroupPython] K_element007  label="K_element : 0.016"  # scripted group (container) (typed FeaturePython)
  n = 0.003003
FEATURE [App::DocumentObjectGroupPython] G4_MUSCLE_STRIATED_ICRU  # scripted group (container) (typed FeaturePython)
  Dunit = g/cm3
  Dvalue = 1.04
  Group = -> [H_element058,C_element064,N_element026,O_element066,Na_element012,P_element008,S_element018,K_element007]
  conduct = 2
  density = 1
  expand = 3
  formula = G4_MUSCLE_STRIATED_ICRU
  name = G4_MUSCLE_STRIATED_ICRU
  specific = 4
FEATURE [App::DocumentObjectGroupPython] H_element059  label="H_element : 0.098"  # scripted group (container) (typed FeaturePython)
  n = 0.0982341
FEATURE [App::DocumentObjectGroupPython] C_element065  label="C_element : 0.156"  # scripted group (container) (typed FeaturePython)
  n = 0.156214
FEATURE [App::DocumentObjectGroupPython] N_element027  label="N_element : 0.757"  # scripted group (container) (typed FeaturePython)
  n = 0.035451
FEATURE [App::DocumentObjectGroupPython] O_element067  label="O_element : 0.880"  # scripted group (container) (typed FeaturePython)
  n = 0.710101
FEATURE [App::DocumentObjectGroupPython] G4_MUSCLE_WITH_SUCROSE  # scripted group (container) (typed FeaturePython)
  Dunit = g/cm3
  Dvalue = 1.11
  Group = -> [H_element059,C_element065,N_element027,O_element067]
  conduct = 2
  density = 1
  expand = 3
  formula = G4_MUSCLE_WITH_SUCROSE
  name = G4_MUSCLE_WITH_SUCROSE
  specific = 4
FEATURE [App::DocumentObjectGroupPython] H_element060  label="H_element : 0.138"  # scripted group (container) (typed FeaturePython)
  n = 0.101969
FEATURE [App::DocumentObjectGroupPython] C_element066  label="C_element : 0.120"  # scripted group (container) (typed FeaturePython)
  n = 0.120058
FEATURE [App::DocumentObjectGroupPython] N_element028  label="N_element : 0.758"  # scripted group (container) (typed FeaturePython)
  n = 0.035451
FEATURE [App::DocumentObjectGroupPython] O_element068  label="O_element : 0.743"  # scripted group (container) (typed FeaturePython)
  n = 0.742522
FEATURE [App::DocumentObjectGroupPython] G4_MUSCLE_WITHOUT_SUCROSE  # scripted group (container) (typed FeaturePython)
  Dunit = g/cm3
  Dvalue = 1.07
  Group = -> [H_element060,C_element066,N_element028,O_element068]
  conduct = 2
  density = 1
  expand = 3
  formula = G4_MUSCLE_WITHOUT_SUCROSE
  name = G4_MUSCLE_WITHOUT_SUCROSE
  specific = 4
FEATURE [App::DocumentObjectGroupPython] C_element067  label="C_element : 10"  # scripted group (container) (typed FeaturePython)
  n = 10
  ref = C_element
FEATURE [App::DocumentObjectGroupPython] H_element061  label="H_element : 030"  # scripted group (container) (typed FeaturePython)
  n = 8
  ref = H_element
FEATURE [App::DocumentObjectGroupPython] G4_NAPHTHALENE  # scripted group (container) (typed FeaturePython)
  Dunit = g/cm3
  Dvalue = 1.145
  Group = -> [C_element067,H_element061]
  conduct = 2
  density = 1
  expand = 3
  formula = G4_NAPHTHALENE
  name = G4_NAPHTHALENE
  specific = 4
FEATURE [App::DocumentObjectGroupPython] C_element068  label="C_element : 034"  # scripted group (container) (typed FeaturePython)
  n = 6
  ref = C_element
FEATURE [App::DocumentObjectGroupPython] H_element062  label="H_element : 031"  # scripted group (container) (typed FeaturePython)
  n = 5
  ref = H_element
FEATURE [App::DocumentObjectGroupPython] N_element029  label="N_element : 012"  # scripted group (container) (typed FeaturePython)
  n = 1
  ref = N_element
FEATURE [App::DocumentObjectGroupPython] O_element069  label="O_element : 034"  # scripted group (container) (typed FeaturePython)
  n = 2
  ref = O_element
FEATURE [App::DocumentObjectGroupPython] G4_NITROBENZENE  # scripted group (container) (typed FeaturePython)
  Dunit = g/cm3
  Dvalue = 1.19867
  Group = -> [C_element068,H_element062,N_element029,O_element069]
  conduct = 2
  density = 1
  expand = 3
  formula = G4_NITROBENZENE
  name = G4_NITROBENZENE
  specific = 4
FEATURE [App::DocumentObjectGroupPython] N_element030  label="N_element : 013"  # scripted group (container) (typed FeaturePython)
  n = 2
  ref = N_element
FEATURE [App::DocumentObjectGroupPython] O_element070  label="O_element : 035"  # scripted group (container) (typed FeaturePython)
  n = 1
  ref = O_element
FEATURE [App::DocumentObjectGroupPython] G4_NITROUS_OXIDE  # scripted group (container) (typed FeaturePython)
  Dunit = g/cm3
  Dvalue = 0.00183094
  Group = -> [N_element030,O_element070]
  conduct = 2
  density = 1
  expand = 3
  formula = G4_NITROUS_OXIDE
  name = G4_NITROUS_OXIDE
  specific = 4
FEATURE [App::DocumentObjectGroupPython] H_element063  label="H_element : 0.104"  # scripted group (container) (typed FeaturePython)
  n = 0.103509
FEATURE [App::DocumentObjectGroupPython] C_element069  label="C_element : 0.648"  # scripted group (container) (typed FeaturePython)
  n = 0.648416
FEATURE [App::DocumentObjectGroupPython] N_element031  label="N_element : 0.100"  # scripted group (container) (typed FeaturePython)
  n = 0.0995361
FEATURE [App::DocumentObjectGroupPython] O_element071  label="O_element : 0.149"  # scripted group (container) (typed FeaturePython)
  n = 0.148539
FEATURE [App::DocumentObjectGroupPython] G4_NYLON_8062  label="G4_NYLON-8062"  # scripted group (container) (typed FeaturePython)
  Dunit = g/cm3
  Dvalue = 1.08
  Group = -> [H_element063,C_element069,N_element031,O_element071]
  conduct = 2
  density = 1
  expand = 3
  formula = G4_NYLON-8062
  name = G4_NYLON-8062
  specific = 4
FEATURE [App::DocumentObjectGroupPython] C_element070  label="C_element : 035"  # scripted group (container) (typed FeaturePython)
  n = 6
  ref = C_element
FEATURE [App::DocumentObjectGroupPython] H_element064  label="H_element : 11"  # scripted group (container) (typed FeaturePython)
  n = 11
  ref = H_element
FEATURE [App::DocumentObjectGroupPython] N_element032  label="N_element : 014"  # scripted group (container) (typed FeaturePython)
  n = 1
  ref = N_element
FEATURE [App::DocumentObjectGroupPython] O_element072  label="O_element : 036"  # scripted group (container) (typed FeaturePython)
  n = 1
  ref = O_element
FEATURE [App::DocumentObjectGroupPython] G4_NYLON_6_6  label="G4_NYLON-6-6"  # scripted group (container) (typed FeaturePython)
  Dunit = g/cm3
  Dvalue = 1.14
  Group = -> [C_element070,H_element064,N_element032,O_element072]
  conduct = 2
  density = 1
  expand = 3
  formula = G4_NYLON-6-6
  name = G4_NYLON-6-6
  specific = 4
FEATURE [App::DocumentObjectGroupPython] H_element065  label="H_element : 0.139"  # scripted group (container) (typed FeaturePython)
  n = 0.107062
FEATURE [App::DocumentObjectGroupPython] C_element071  label="C_element : 0.680"  # scripted group (container) (typed FeaturePython)
  n = 0.680449
FEATURE [App::DocumentObjectGroupPython] N_element033  label="N_element : 0.099"  # scripted group (container) (typed FeaturePython)
  n = 0.099189
FEATURE [App::DocumentObjectGroupPython] O_element073  label="O_element : 0.113"  # scripted group (container) (typed FeaturePython)
  n = 0.1133
FEATURE [App::DocumentObjectGroupPython] G4_NYLON_6_10  label="G4_NYLON-6-10"  # scripted group (container) (typed FeaturePython)
  Dunit = g/cm3
  Dvalue = 1.14
  Group = -> [H_element065,C_element071,N_element033,O_element073]
  conduct = 2
  density = 1
  expand = 3
  formula = G4_NYLON-6-10
  name = G4_NYLON-6-10
  specific = 4
FEATURE [App::DocumentObjectGroupPython] H_element066  label="H_element : 0.140"  # scripted group (container) (typed FeaturePython)
  n = 0.115476
FEATURE [App::DocumentObjectGroupPython] C_element072  label="C_element : 0.721"  # scripted group (container) (typed FeaturePython)
  n = 0.720818
FEATURE [App::DocumentObjectGroupPython] N_element034  label="N_element : 0.076"  # scripted group (container) (typed FeaturePython)
  n = 0.0764169
FEATURE [App::DocumentObjectGroupPython] O_element074  label="O_element : 0.087"  # scripted group (container) (typed FeaturePython)
  n = 0.0872889
FEATURE [App::DocumentObjectGroupPython] G4_NYLON_11_RILSAN  label="G4_NYLON-11_RILSAN"  # scripted group (container) (typed FeaturePython)
  Dunit = g/cm3
  Dvalue = 1.425
  Group = -> [H_element066,C_element072,N_element034,O_element074]
  conduct = 2
  density = 1
  expand = 3
  formula = G4_NYLON-11_RILSAN
  name = G4_NYLON-11_RILSAN
  specific = 4
FEATURE [App::DocumentObjectGroupPython] C_element073  label="C_element : 8"  # scripted group (container) (typed FeaturePython)
  n = 8
  ref = C_element
FEATURE [App::DocumentObjectGroupPython] H_element067  label="H_element : 18"  # scripted group (container) (typed FeaturePython)
  n = 18
  ref = H_element
FEATURE [App::DocumentObjectGroupPython] G4_OCTANE  # scripted group (container) (typed FeaturePython)
  Dunit = g/cm3
  Dvalue = 0.7026
  Group = -> [C_element073,H_element067]
  conduct = 2
  density = 1
  expand = 3
  formula = G4_OCTANE
  name = G4_OCTANE
  specific = 4
FEATURE [App::DocumentObjectGroupPython] C_element074  label="C_element : 25"  # scripted group (container) (typed FeaturePython)
  n = 25
  ref = C_element
FEATURE [App::DocumentObjectGroupPython] H_element068  label="H_element : 52"  # scripted group (container) (typed FeaturePython)
  n = 52
  ref = H_element
FEATURE [App::DocumentObjectGroupPython] G4_PARAFFIN  # scripted group (container) (typed FeaturePython)
  Dunit = g/cm3
  Dvalue = 0.93
  Group = -> [C_element074,H_element068]
  conduct = 2
  density = 1
  expand = 3
  formula = G4_PARAFFIN
  name = G4_PARAFFIN
  specific = 4
FEATURE [App::DocumentObjectGroupPython] C_element075  label="C_element : 036"  # scripted group (container) (typed FeaturePython)
  n = 5
  ref = C_element
FEATURE [App::DocumentObjectGroupPython] H_element069  label="H_element : 032"  # scripted group (container) (typed FeaturePython)
  n = 12
  ref = H_element
FEATURE [App::DocumentObjectGroupPython] G4_N_PENTANE  label="G4_N-PENTANE"  # scripted group (container) (typed FeaturePython)
  Dunit = g/cm3
  Dvalue = 0.6262
  Group = -> [C_element075,H_element069]
  conduct = 2
  density = 1
  expand = 3
  formula = G4_N-PENTANE
  name = G4_N-PENTANE
  specific = 4
FEATURE [App::DocumentObjectGroupPython] H_element070  label="H_element : 0.014"  # scripted group (container) (typed FeaturePython)
  n = 0.0141
FEATURE [App::DocumentObjectGroupPython] C_element076  label="C_element : 0.072"  # scripted group (container) (typed FeaturePython)
  n = 0.072261
FEATURE [App::DocumentObjectGroupPython] N_element035  label="N_element : 0.019"  # scripted group (container) (typed FeaturePython)
  n = 0.01932
FEATURE [App::DocumentObjectGroupPython] O_element075  label="O_element : 0.066"  # scripted group (container) (typed FeaturePython)
  n = 0.066101
FEATURE [App::DocumentObjectGroupPython] S_element019  label="S_element : 0.020"  # scripted group (container) (typed FeaturePython)
  n = 0.00189
FEATURE [App::DocumentObjectGroupPython] Br_element004  label="Br_element : 0.349"  # scripted group (container) (typed FeaturePython)
  n = 0.349103
FEATURE [App::DocumentObjectGroupPython] Ag_element001  label="Ag_element : 0.474"  # scripted group (container) (typed FeaturePython)
  n = 0.474105
FEATURE [App::DocumentObjectGroupPython] I_element005  label="I_element : 0.003"  # scripted group (container) (typed FeaturePython)
  n = 0.00312
FEATURE [App::DocumentObjectGroupPython] G4_PHOTO_EMULSION  # scripted group (container) (typed FeaturePython)
  Dunit = g/cm3
  Dvalue = 3.815
  Group = -> [H_element070,C_element076,N_element035,O_element075,S_element019,Br_element004,Ag_element001,I_element005]
  conduct = 2
  density = 1
  expand = 3
  formula = G4_PHOTO_EMULSION
  name = G4_PHOTO_EMULSION
  specific = 4
FEATURE [App::DocumentObjectGroupPython] C_element077  label="C_element : 9"  # scripted group (container) (typed FeaturePython)
  n = 9
  ref = C_element
FEATURE [App::DocumentObjectGroupPython] H_element071  label="H_element : 033"  # scripted group (container) (typed FeaturePython)
  n = 10
  ref = H_element
FEATURE [App::DocumentObjectGroupPython] G4_PLASTIC_SC_VINYLTOLUENE  # scripted group (container) (typed FeaturePython)
  Dunit = g/cm3
  Dvalue = 1.032
  Group = -> [C_element077,H_element071]
  conduct = 2
  density = 1
  expand = 3
  formula = G4_PLASTIC_SC_VINYLTOLUENE
  name = G4_PLASTIC_SC_VINYLTOLUENE
  specific = 4
FEATURE [App::DocumentObjectGroupPython] Pu_element001  label="Pu_element : 1"  # scripted group (container) (typed FeaturePython)
  n = 1
  ref = Pu_element
FEATURE [App::DocumentObjectGroupPython] O_element076  label="O_element : 037"  # scripted group (container) (typed FeaturePython)
  n = 2
  ref = O_element
FEATURE [App::DocumentObjectGroupPython] G4_PLUTONIUM_DIOXIDE  # scripted group (container) (typed FeaturePython)
  Dunit = g/cm3
  Dvalue = 11.46
  Group = -> [Pu_element001,O_element076]
  conduct = 2
  density = 1
  expand = 3
  formula = G4_PLUTONIUM_DIOXIDE
  name = G4_PLUTONIUM_DIOXIDE
  specific = 4
FEATURE [App::DocumentObjectGroupPython] C_element078  label="C_element : 037"  # scripted group (container) (typed FeaturePython)
  n = 3
  ref = C_element
FEATURE [App::DocumentObjectGroupPython] H_element072  label="H_element : 034"  # scripted group (container) (typed FeaturePython)
  n = 3
  ref = H_element
FEATURE [App::DocumentObjectGroupPython] N_element036  label="N_element : 015"  # scripted group (container) (typed FeaturePython)
  n = 1
  ref = N_element
FEATURE [App::DocumentObjectGroupPython] G4_POLYACRYLONITRILE  # scripted group (container) (typed FeaturePython)
  Dunit = g/cm3
  Dvalue = 1.17
  Group = -> [C_element078,H_element072,N_element036]
  conduct = 2
  density = 1
  expand = 3
  formula = G4_POLYACRYLONITRILE
  name = G4_POLYACRYLONITRILE
  specific = 4
FEATURE [App::DocumentObjectGroupPython] C_element079  label="C_element : 16"  # scripted group (container) (typed FeaturePython)
  n = 16
  ref = C_element
FEATURE [App::DocumentObjectGroupPython] H_element073  label="H_element : 035"  # scripted group (container) (typed FeaturePython)
  n = 14
  ref = H_element
FEATURE [App::DocumentObjectGroupPython] O_element077  label="O_element : 038"  # scripted group (container) (typed FeaturePython)
  n = 3
  ref = O_element
FEATURE [App::DocumentObjectGroupPython] G4_POLYCARBONATE  # scripted group (container) (typed FeaturePython)
  Dunit = g/cm3
  Dvalue = 1.2
  Group = -> [C_element079,H_element073,O_element077]
  conduct = 2
  density = 1
  expand = 3
  formula = G4_POLYCARBONATE
  name = G4_POLYCARBONATE
  specific = 4
FEATURE [App::DocumentObjectGroupPython] C_element080  label="C_element : 038"  # scripted group (container) (typed FeaturePython)
  n = 8
  ref = C_element
FEATURE [App::DocumentObjectGroupPython] H_element074  label="H_element : 036"  # scripted group (container) (typed FeaturePython)
  n = 7
  ref = H_element
FEATURE [App::DocumentObjectGroupPython] Cl_element017  label="Cl_element : 007"  # scripted group (container) (typed FeaturePython)
  n = 1
  ref = Cl_element
FEATURE [App::DocumentObjectGroupPython] G4_POLYCHLOROSTYRENE  # scripted group (container) (typed FeaturePython)
  Dunit = g/cm3
  Dvalue = 1.3
  Group = -> [C_element080,H_element074,Cl_element017]
  conduct = 2
  density = 1
  expand = 3
  formula = G4_POLYCHLOROSTYRENE
  name = G4_POLYCHLOROSTYRENE
  specific = 4
FEATURE [App::DocumentObjectGroupPython] C_element081  label="C_element : 039"  # scripted group (container) (typed FeaturePython)
  n = 1
  ref = C_element
FEATURE [App::DocumentObjectGroupPython] H_element075  label="H_element : 037"  # scripted group (container) (typed FeaturePython)
  n = 2
  ref = H_element
FEATURE [App::DocumentObjectGroupPython] G4_POLYETHYLENE  # scripted group (container) (typed FeaturePython)
  Dunit = g/cm3
  Dvalue = 0.94
  Group = -> [C_element081,H_element075]
  conduct = 2
  density = 1
  expand = 3
  formula = G4_POLYETHYLENE
  name = G4_POLYETHYLENE
  specific = 4
FEATURE [App::DocumentObjectGroupPython] C_element082  label="C_element : 040"  # scripted group (container) (typed FeaturePython)
  n = 10
  ref = C_element
FEATURE [App::DocumentObjectGroupPython] H_element076  label="H_element : 038"  # scripted group (container) (typed FeaturePython)
  n = 8
  ref = H_element
FEATURE [App::DocumentObjectGroupPython] O_element078  label="O_element : 039"  # scripted group (container) (typed FeaturePython)
  n = 4
  ref = O_element
FEATURE [App::DocumentObjectGroupPython] G4_MYLAR  # scripted group (container) (typed FeaturePython)
  Dunit = g/cm3
  Dvalue = 1.4
  Group = -> [C_element082,H_element076,O_element078]
  conduct = 2
  density = 1
  expand = 3
  formula = G4_MYLAR
  name = G4_MYLAR
  specific = 4
FEATURE [App::DocumentObjectGroupPython] C_element083  label="C_element : 041"  # scripted group (container) (typed FeaturePython)
  n = 5
  ref = C_element
FEATURE [App::DocumentObjectGroupPython] H_element077  label="H_element : 039"  # scripted group (container) (typed FeaturePython)
  n = 8
  ref = H_element
FEATURE [App::DocumentObjectGroupPython] O_element079  label="O_element : 040"  # scripted group (container) (typed FeaturePython)
  n = 2
  ref = O_element
FEATURE [App::DocumentObjectGroupPython] G4_PLEXIGLASS  # scripted group (container) (typed FeaturePython)
  Dunit = g/cm3
  Dvalue = 1.19
  Group = -> [C_element083,H_element077,O_element079]
  conduct = 2
  density = 1
  expand = 3
  formula = G4_PLEXIGLASS
  name = G4_PLEXIGLASS
  specific = 4
FEATURE [App::DocumentObjectGroupPython] C_element084  label="C_element : 042"  # scripted group (container) (typed FeaturePython)
  n = 1
  ref = C_element
FEATURE [App::DocumentObjectGroupPython] H_element078  label="H_element : 040"  # scripted group (container) (typed FeaturePython)
  n = 2
  ref = H_element
FEATURE [App::DocumentObjectGroupPython] O_element080  label="O_element : 041"  # scripted group (container) (typed FeaturePython)
  n = 1
  ref = O_element
FEATURE [App::DocumentObjectGroupPython] G4_POLYOXYMETHYLENE  # scripted group (container) (typed FeaturePython)
  Dunit = g/cm3
  Dvalue = 1.425
  Group = -> [C_element084,H_element078,O_element080]
  conduct = 2
  density = 1
  expand = 3
  formula = G4_POLYOXYMETHYLENE
  name = G4_POLYOXYMETHYLENE
  specific = 4
FEATURE [App::DocumentObjectGroupPython] C_element085  label="C_element : 043"  # scripted group (container) (typed FeaturePython)
  n = 2
  ref = C_element
FEATURE [App::DocumentObjectGroupPython] H_element079  label="H_element : 041"  # scripted group (container) (typed FeaturePython)
  n = 4
  ref = H_element
FEATURE [App::DocumentObjectGroupPython] G4_POLYPROPYLENE  # scripted group (container) (typed FeaturePython)
  Dunit = g/cm3
  Dvalue = 0.9
  Group = -> [C_element085,H_element079]
  conduct = 2
  density = 1
  expand = 3
  formula = G4_POLYPROPYLENE
  name = G4_POLYPROPYLENE
  specific = 4
FEATURE [App::DocumentObjectGroupPython] C_element086  label="C_element : 044"  # scripted group (container) (typed FeaturePython)
  n = 8
  ref = C_element
FEATURE [App::DocumentObjectGroupPython] H_element080  label="H_element : 042"  # scripted group (container) (typed FeaturePython)
  n = 8
  ref = H_element
FEATURE [App::DocumentObjectGroupPython] G4_POLYSTYRENE  # scripted group (container) (typed FeaturePython)
  Dunit = g/cm3
  Dvalue = 1.06
  Group = -> [C_element086,H_element080]
  conduct = 2
  density = 1
  expand = 3
  formula = G4_POLYSTYRENE
  name = G4_POLYSTYRENE
  specific = 4
FEATURE [App::DocumentObjectGroupPython] C_element087  label="C_element : 045"  # scripted group (container) (typed FeaturePython)
  n = 2
  ref = C_element
FEATURE [App::DocumentObjectGroupPython] F_element014  label="F_element : 4"  # scripted group (container) (typed FeaturePython)
  n = 4
  ref = F_element
FEATURE [App::DocumentObjectGroupPython] G4_TEFLON  # scripted group (container) (typed FeaturePython)
  Dunit = g/cm3
  Dvalue = 2.2
  Group = -> [C_element087,F_element014]
  conduct = 2
  density = 1
  expand = 3
  formula = G4_TEFLON
  name = G4_TEFLON
  specific = 4
FEATURE [App::DocumentObjectGroupPython] C_element088  label="C_element : 046"  # scripted group (container) (typed FeaturePython)
  n = 2
  ref = C_element
FEATURE [App::DocumentObjectGroupPython] F_element015  label="F_element : 006"  # scripted group (container) (typed FeaturePython)
  n = 3
  ref = F_element
FEATURE [App::DocumentObjectGroupPython] Cl_element018  label="Cl_element : 008"  # scripted group (container) (typed FeaturePython)
  n = 1
  ref = Cl_element
FEATURE [App::DocumentObjectGroupPython] G4_POLYTRIFLUOROCHLOROETHYLENE  # scripted group (container) (typed FeaturePython)
  Dunit = g/cm3
  Dvalue = 2.1
  Group = -> [C_element088,F_element015,Cl_element018]
  conduct = 2
  density = 1
  expand = 3
  formula = G4_POLYTRIFLUOROCHLOROETHYLENE
  name = G4_POLYTRIFLUOROCHLOROETHYLENE
  specific = 4
FEATURE [App::DocumentObjectGroupPython] C_element089  label="C_element : 047"  # scripted group (container) (typed FeaturePython)
  n = 4
  ref = C_element
FEATURE [App::DocumentObjectGroupPython] H_element081  label="H_element : 043"  # scripted group (container) (typed FeaturePython)
  n = 6
  ref = H_element
FEATURE [App::DocumentObjectGroupPython] O_element081  label="O_element : 042"  # scripted group (container) (typed FeaturePython)
  n = 2
  ref = O_element
FEATURE [App::DocumentObjectGroupPython] G4_POLYVINYL_ACETATE  # scripted group (container) (typed FeaturePython)
  Dunit = g/cm3
  Dvalue = 1.19
  Group = -> [C_element089,H_element081,O_element081]
  conduct = 2
  density = 1
  expand = 3
  formula = G4_POLYVINYL_ACETATE
  name = G4_POLYVINYL_ACETATE
  specific = 4
FEATURE [App::DocumentObjectGroupPython] C_element090  label="C_element : 048"  # scripted group (container) (typed FeaturePython)
  n = 2
  ref = C_element
FEATURE [App::DocumentObjectGroupPython] H_element082  label="H_element : 044"  # scripted group (container) (typed FeaturePython)
  n = 4
  ref = H_element
FEATURE [App::DocumentObjectGroupPython] O_element082  label="O_element : 043"  # scripted group (container) (typed FeaturePython)
  n = 1
  ref = O_element
FEATURE [App::DocumentObjectGroupPython] G4_POLYVINYL_ALCOHOL  # scripted group (container) (typed FeaturePython)
  Dunit = g/cm3
  Dvalue = 1.3
  Group = -> [C_element090,H_element082,O_element082]
  conduct = 2
  density = 1
  expand = 3
  formula = G4_POLYVINYL_ALCOHOL
  name = G4_POLYVINYL_ALCOHOL
  specific = 4
FEATURE [App::DocumentObjectGroupPython] C_element091  label="C_element : 049"  # scripted group (container) (typed FeaturePython)
  n = 8
  ref = C_element
FEATURE [App::DocumentObjectGroupPython] H_element083  label="H_element : 045"  # scripted group (container) (typed FeaturePython)
  n = 14
  ref = H_element
FEATURE [App::DocumentObjectGroupPython] O_element083  label="O_element : 044"  # scripted group (container) (typed FeaturePython)
  n = 2
  ref = O_element
FEATURE [App::DocumentObjectGroupPython] G4_POLYVINYL_BUTYRAL  # scripted group (container) (typed FeaturePython)
  Dunit = g/cm3
  Dvalue = 1.12
  Group = -> [C_element091,H_element083,O_element083]
  conduct = 2
  density = 1
  expand = 3
  formula = G4_POLYVINYL_BUTYRAL
  name = G4_POLYVINYL_BUTYRAL
  specific = 4
FEATURE [App::DocumentObjectGroupPython] C_element092  label="C_element : 050"  # scripted group (container) (typed FeaturePython)
  n = 2
  ref = C_element
FEATURE [App::DocumentObjectGroupPython] H_element084  label="H_element : 046"  # scripted group (container) (typed FeaturePython)
  n = 3
  ref = H_element
FEATURE [App::DocumentObjectGroupPython] Cl_element019  label="Cl_element : 009"  # scripted group (container) (typed FeaturePython)
  n = 1
  ref = Cl_element
FEATURE [App::DocumentObjectGroupPython] G4_POLYVINYL_CHLORIDE  # scripted group (container) (typed FeaturePython)
  Dunit = g/cm3
  Dvalue = 1.3
  Group = -> [C_element092,H_element084,Cl_element019]
  conduct = 2
  density = 1
  expand = 3
  formula = G4_POLYVINYL_CHLORIDE
  name = G4_POLYVINYL_CHLORIDE
  specific = 4
FEATURE [App::DocumentObjectGroupPython] C_element093  label="C_element : 051"  # scripted group (container) (typed FeaturePython)
  n = 2
  ref = C_element
FEATURE [App::DocumentObjectGroupPython] H_element085  label="H_element : 047"  # scripted group (container) (typed FeaturePython)
  n = 2
  ref = H_element
FEATURE [App::DocumentObjectGroupPython] Cl_element020  label="Cl_element : 010"  # scripted group (container) (typed FeaturePython)
  n = 2
  ref = Cl_element
FEATURE [App::DocumentObjectGroupPython] G4_POLYVINYLIDENE_CHLORIDE  # scripted group (container) (typed FeaturePython)
  Dunit = g/cm3
  Dvalue = 1.7
  Group = -> [C_element093,H_element085,Cl_element020]
  conduct = 2
  density = 1
  expand = 3
  formula = G4_POLYVINYLIDENE_CHLORIDE
  name = G4_POLYVINYLIDENE_CHLORIDE
  specific = 4
FEATURE [App::DocumentObjectGroupPython] C_element094  label="C_element : 052"  # scripted group (container) (typed FeaturePython)
  n = 2
  ref = C_element
FEATURE [App::DocumentObjectGroupPython] H_element086  label="H_element : 048"  # scripted group (container) (typed FeaturePython)
  n = 2
  ref = H_element
FEATURE [App::DocumentObjectGroupPython] F_element016  label="F_element : 007"  # scripted group (container) (typed FeaturePython)
  n = 2
  ref = F_element
FEATURE [App::DocumentObjectGroupPython] G4_POLYVINYLIDENE_FLUORIDE  # scripted group (container) (typed FeaturePython)
  Dunit = g/cm3
  Dvalue = 1.76
  Group = -> [C_element094,H_element086,F_element016]
  conduct = 2
  density = 1
  expand = 3
  formula = G4_POLYVINYLIDENE_FLUORIDE
  name = G4_POLYVINYLIDENE_FLUORIDE
  specific = 4
FEATURE [App::DocumentObjectGroupPython] C_element095  label="C_element : 053"  # scripted group (container) (typed FeaturePython)
  n = 6
  ref = C_element
FEATURE [App::DocumentObjectGroupPython] H_element087  label="H_element : 9"  # scripted group (container) (typed FeaturePython)
  n = 9
  ref = H_element
FEATURE [App::DocumentObjectGroupPython] N_element037  label="N_element : 016"  # scripted group (container) (typed FeaturePython)
  n = 1
  ref = N_element
FEATURE [App::DocumentObjectGroupPython] O_element084  label="O_element : 045"  # scripted group (container) (typed FeaturePython)
  n = 1
  ref = O_element
FEATURE [App::DocumentObjectGroupPython] G4_POLYVINYL_PYRROLIDONE  # scripted group (container) (typed FeaturePython)
  Dunit = g/cm3
  Dvalue = 1.25
  Group = -> [C_element095,H_element087,N_element037,O_element084]
  conduct = 2
  density = 1
  expand = 3
  formula = G4_POLYVINYL_PYRROLIDONE
  name = G4_POLYVINYL_PYRROLIDONE
  specific = 4
FEATURE [App::DocumentObjectGroupPython] K_element008  label="K_element : 1"  # scripted group (container) (typed FeaturePython)
  n = 1
  ref = K_element
FEATURE [App::DocumentObjectGroupPython] I_element006  label="I_element : 003"  # scripted group (container) (typed FeaturePython)
  n = 1
  ref = I_element
FEATURE [App::DocumentObjectGroupPython] G4_POTASSIUM_IODIDE  # scripted group (container) (typed FeaturePython)
  Dunit = g/cm3
  Dvalue = 3.13
  Group = -> [K_element008,I_element006]
  conduct = 2
  density = 1
  expand = 3
  formula = G4_POTASSIUM_IODIDE
  name = G4_POTASSIUM_IODIDE
  specific = 4
FEATURE [App::DocumentObjectGroupPython] K_element009  label="K_element : 2"  # scripted group (container) (typed FeaturePython)
  n = 2
  ref = K_element
FEATURE [App::DocumentObjectGroupPython] O_element085  label="O_element : 046"  # scripted group (container) (typed FeaturePython)
  n = 1
  ref = O_element
FEATURE [App::DocumentObjectGroupPython] G4_POTASSIUM_OXIDE  # scripted group (container) (typed FeaturePython)
  Dunit = g/cm3
  Dvalue = 2.32
  Group = -> [K_element009,O_element085]
  conduct = 2
  density = 1
  expand = 3
  formula = G4_POTASSIUM_OXIDE
  name = G4_POTASSIUM_OXIDE
  specific = 4
FEATURE [App::DocumentObjectGroupPython] C_element096  label="C_element : 054"  # scripted group (container) (typed FeaturePython)
  n = 3
  ref = C_element
FEATURE [App::DocumentObjectGroupPython] H_element088  label="H_element : 049"  # scripted group (container) (typed FeaturePython)
  n = 8
  ref = H_element
FEATURE [App::DocumentObjectGroupPython] G4_PROPANE  # scripted group (container) (typed FeaturePython)
  Dunit = g/cm3
  Dvalue = 0.00187939
  Group = -> [C_element096,H_element088]
  conduct = 2
  density = 1
  expand = 3
  formula = G4_PROPANE
  name = G4_PROPANE
  specific = 4
FEATURE [App::DocumentObjectGroupPython] C_element097  label="C_element : 055"  # scripted group (container) (typed FeaturePython)
  n = 3
  ref = C_element
FEATURE [App::DocumentObjectGroupPython] H_element089  label="H_element : 050"  # scripted group (container) (typed FeaturePython)
  n = 8
  ref = H_element
FEATURE [App::DocumentObjectGroupPython] G4_lPROPANE  # scripted group (container) (typed FeaturePython)
  Dunit = g/cm3
  Dvalue = 0.43
  Group = -> [C_element097,H_element089]
  conduct = 2
  density = 1
  expand = 3
  formula = G4_lPROPANE
  name = G4_lPROPANE
  specific = 4
FEATURE [App::DocumentObjectGroupPython] C_element098  label="C_element : 056"  # scripted group (container) (typed FeaturePython)
  n = 3
  ref = C_element
FEATURE [App::DocumentObjectGroupPython] H_element090  label="H_element : 051"  # scripted group (container) (typed FeaturePython)
  n = 8
  ref = H_element
FEATURE [App::DocumentObjectGroupPython] O_element086  label="O_element : 047"  # scripted group (container) (typed FeaturePython)
  n = 1
  ref = O_element
FEATURE [App::DocumentObjectGroupPython] G4_N_PROPYL_ALCOHOL  label="G4_N-PROPYL_ALCOHOL"  # scripted group (container) (typed FeaturePython)
  Dunit = g/cm3
  Dvalue = 0.8035
  Group = -> [C_element098,H_element090,O_element086]
  conduct = 2
  density = 1
  expand = 3
  formula = G4_N-PROPYL_ALCOHOL
  name = G4_N-PROPYL_ALCOHOL
  specific = 4
FEATURE [App::DocumentObjectGroupPython] C_element099  label="C_element : 057"  # scripted group (container) (typed FeaturePython)
  n = 5
  ref = C_element
FEATURE [App::DocumentObjectGroupPython] H_element091  label="H_element : 052"  # scripted group (container) (typed FeaturePython)
  n = 5
  ref = H_element
FEATURE [App::DocumentObjectGroupPython] N_element038  label="N_element : 017"  # scripted group (container) (typed FeaturePython)
  n = 1
  ref = N_element
FEATURE [App::DocumentObjectGroupPython] G4_PYRIDINE  # scripted group (container) (typed FeaturePython)
  Dunit = g/cm3
  Dvalue = 0.9819
  Group = -> [C_element099,H_element091,N_element038]
  conduct = 2
  density = 1
  expand = 3
  formula = G4_PYRIDINE
  name = G4_PYRIDINE
  specific = 4
FEATURE [App::DocumentObjectGroupPython] H_element092  label="H_element : 0.144"  # scripted group (container) (typed FeaturePython)
  n = 0.143711
FEATURE [App::DocumentObjectGroupPython] C_element100  label="C_element : 0.856"  # scripted group (container) (typed FeaturePython)
  n = 0.856289
FEATURE [App::DocumentObjectGroupPython] G4_RUBBER_BUTYL  # scripted group (container) (typed FeaturePython)
  Dunit = g/cm3
  Dvalue = 0.92
  Group = -> [H_element092,C_element100]
  conduct = 2
  density = 1
  expand = 3
  formula = G4_RUBBER_BUTYL
  name = G4_RUBBER_BUTYL
  specific = 4
FEATURE [App::DocumentObjectGroupPython] H_element093  label="H_element : 0.118"  # scripted group (container) (typed FeaturePython)
  n = 0.118371
FEATURE [App::DocumentObjectGroupPython] C_element101  label="C_element : 0.882"  # scripted group (container) (typed FeaturePython)
  n = 0.881629
FEATURE [App::DocumentObjectGroupPython] G4_RUBBER_NATURAL  # scripted group (container) (typed FeaturePython)
  Dunit = g/cm3
  Dvalue = 0.92
  Group = -> [H_element093,C_element101]
  conduct = 2
  density = 1
  expand = 3
  formula = G4_RUBBER_NATURAL
  name = G4_RUBBER_NATURAL
  specific = 4
FEATURE [App::DocumentObjectGroupPython] H_element094  label="H_element : 0.145"  # scripted group (container) (typed FeaturePython)
  n = 0.05692
FEATURE [App::DocumentObjectGroupPython] C_element102  label="C_element : 0.543"  # scripted group (container) (typed FeaturePython)
  n = 0.542646
FEATURE [App::DocumentObjectGroupPython] Cl_element021  label="Cl_element : 0.400"  # scripted group (container) (typed FeaturePython)
  n = 0.400434
FEATURE [App::DocumentObjectGroupPython] G4_RUBBER_NEOPRENE  # scripted group (container) (typed FeaturePython)
  Dunit = g/cm3
  Dvalue = 1.23
  Group = -> [H_element094,C_element102,Cl_element021]
  conduct = 2
  density = 1
  expand = 3
  formula = G4_RUBBER_NEOPRENE
  name = G4_RUBBER_NEOPRENE
  specific = 4
FEATURE [App::DocumentObjectGroupPython] Si_element006  label="Si_element : 1"  # scripted group (container) (typed FeaturePython)
  n = 1
  ref = Si_element
FEATURE [App::DocumentObjectGroupPython] O_element087  label="O_element : 048"  # scripted group (container) (typed FeaturePython)
  n = 2
  ref = O_element
FEATURE [App::DocumentObjectGroupPython] G4_SILICON_DIOXIDE  # scripted group (container) (typed FeaturePython)
  Dunit = g/cm3
  Dvalue = 2.32
  Group = -> [Si_element006,O_element087]
  conduct = 2
  density = 1
  expand = 3
  formula = G4_SILICON_DIOXIDE
  name = G4_SILICON_DIOXIDE
  specific = 4
FEATURE [App::DocumentObjectGroupPython] Ag_element002  label="Ag_element : 1"  # scripted group (container) (typed FeaturePython)
  n = 1
  ref = Ag_element
FEATURE [App::DocumentObjectGroupPython] Br_element005  label="Br_element : 003"  # scripted group (container) (typed FeaturePython)
  n = 1
  ref = Br_element
FEATURE [App::DocumentObjectGroupPython] G4_SILVER_BROMIDE  # scripted group (container) (typed FeaturePython)
  Dunit = g/cm3
  Dvalue = 6.473
  Group = -> [Ag_element002,Br_element005]
  conduct = 2
  density = 1
  expand = 3
  formula = G4_SILVER_BROMIDE
  name = G4_SILVER_BROMIDE
  specific = 4
FEATURE [App::DocumentObjectGroupPython] Ag_element003  label="Ag_element : 002"  # scripted group (container) (typed FeaturePython)
  n = 1
  ref = Ag_element
FEATURE [App::DocumentObjectGroupPython] Cl_element022  label="Cl_element : 011"  # scripted group (container) (typed FeaturePython)
  n = 1
  ref = Cl_element
FEATURE [App::DocumentObjectGroupPython] G4_SILVER_CHLORIDE  # scripted group (container) (typed FeaturePython)
  Dunit = g/cm3
  Dvalue = 5.56
  Group = -> [Ag_element003,Cl_element022]
  conduct = 2
  density = 1
  expand = 3
  formula = G4_SILVER_CHLORIDE
  name = G4_SILVER_CHLORIDE
  specific = 4
FEATURE [App::DocumentObjectGroupPython] Br_element006  label="Br_element : 0.423"  # scripted group (container) (typed FeaturePython)
  n = 0.422895
FEATURE [App::DocumentObjectGroupPython] Ag_element004  label="Ag_element : 0.574"  # scripted group (container) (typed FeaturePython)
  n = 0.573748
FEATURE [App::DocumentObjectGroupPython] I_element007  label="I_element : 0.649"  # scripted group (container) (typed FeaturePython)
  n = 0.003357
FEATURE [App::DocumentObjectGroupPython] G4_SILVER_HALIDES  # scripted group (container) (typed FeaturePython)
  Dunit = g/cm3
  Dvalue = 6.47
  Group = -> [Br_element006,Ag_element004,I_element007]
  conduct = 2
  density = 1
  expand = 3
  formula = G4_SILVER_HALIDES
  name = G4_SILVER_HALIDES
  specific = 4
FEATURE [App::DocumentObjectGroupPython] Ag_element005  label="Ag_element : 003"  # scripted group (container) (typed FeaturePython)
  n = 1
  ref = Ag_element
FEATURE [App::DocumentObjectGroupPython] I_element008  label="I_element : 004"  # scripted group (container) (typed FeaturePython)
  n = 1
  ref = I_element
FEATURE [App::DocumentObjectGroupPython] G4_SILVER_IODIDE  # scripted group (container) (typed FeaturePython)
  Dunit = g/cm3
  Dvalue = 6.01
  Group = -> [Ag_element005,I_element008]
  conduct = 2
  density = 1
  expand = 3
  formula = G4_SILVER_IODIDE
  name = G4_SILVER_IODIDE
  specific = 4
FEATURE [App::DocumentObjectGroupPython] H_element095  label="H_element : 0.100"  # scripted group (container) (typed FeaturePython)
  n = 0.1
FEATURE [App::DocumentObjectGroupPython] C_element103  label="C_element : 0.204"  # scripted group (container) (typed FeaturePython)
  n = 0.204
FEATURE [App::DocumentObjectGroupPython] N_element039  label="N_element : 0.759"  # scripted group (container) (typed FeaturePython)
  n = 0.042
FEATURE [App::DocumentObjectGroupPython] O_element088  label="O_element : 0.645"  # scripted group (container) (typed FeaturePython)
  n = 0.645
FEATURE [App::DocumentObjectGroupPython] Na_element013  label="Na_element : 0.100"  # scripted group (container) (typed FeaturePython)
  n = 0.002
FEATURE [App::DocumentObjectGroupPython] P_element009  label="P_element : 0.107"  # scripted group (container) (typed FeaturePython)
  n = 0.001
FEATURE [App::DocumentObjectGroupPython] S_element020  label="S_element : 0.021"  # scripted group (container) (typed FeaturePython)
  n = 0.002
FEATURE [App::DocumentObjectGroupPython] Cl_element023  label="Cl_element : 0.590"  # scripted group (container) (typed FeaturePython)
  n = 0.003
FEATURE [App::DocumentObjectGroupPython] K_element010  label="K_element : 0.001"  # scripted group (container) (typed FeaturePython)
  n = 0.001
FEATURE [App::DocumentObjectGroupPython] G4_SKIN_ICRP  # scripted group (container) (typed FeaturePython)
  Dunit = g/cm3
  Dvalue = 1.09
  Group = -> [H_element095,C_element103,N_element039,O_element088,Na_element013,P_element009,S_element020,Cl_element023,K_element010]
  conduct = 2
  density = 1
  expand = 3
  formula = G4_SKIN_ICRP
  name = G4_SKIN_ICRP
  specific = 4
FEATURE [App::DocumentObjectGroupPython] Na_element014  label="Na_element : 2"  # scripted group (container) (typed FeaturePython)
  n = 2
  ref = Na_element
FEATURE [App::DocumentObjectGroupPython] C_element104  label="C_element : 058"  # scripted group (container) (typed FeaturePython)
  n = 1
  ref = C_element
FEATURE [App::DocumentObjectGroupPython] O_element089  label="O_element : 049"  # scripted group (container) (typed FeaturePython)
  n = 3
  ref = O_element
FEATURE [App::DocumentObjectGroupPython] G4_SODIUM_CARBONATE  # scripted group (container) (typed FeaturePython)
  Dunit = g/cm3
  Dvalue = 2.532
  Group = -> [Na_element014,C_element104,O_element089]
  conduct = 2
  density = 1
  expand = 3
  formula = G4_SODIUM_CARBONATE
  name = G4_SODIUM_CARBONATE
  specific = 4
FEATURE [App::DocumentObjectGroupPython] Na_element015  label="Na_element : 1"  # scripted group (container) (typed FeaturePython)
  n = 1
  ref = Na_element
FEATURE [App::DocumentObjectGroupPython] I_element009  label="I_element : 005"  # scripted group (container) (typed FeaturePython)
  n = 1
  ref = I_element
FEATURE [App::DocumentObjectGroupPython] G4_SODIUM_IODIDE  # scripted group (container) (typed FeaturePython)
  Dunit = g/cm3
  Dvalue = 3.667
  Group = -> [Na_element015,I_element009]
  conduct = 2
  density = 1
  expand = 3
  formula = G4_SODIUM_IODIDE
  name = G4_SODIUM_IODIDE
  specific = 4
FEATURE [App::DocumentObjectGroupPython] Na_element016  label="Na_element : 003"  # scripted group (container) (typed FeaturePython)
  n = 2
  ref = Na_element
FEATURE [App::DocumentObjectGroupPython] O_element090  label="O_element : 050"  # scripted group (container) (typed FeaturePython)
  n = 1
  ref = O_element
FEATURE [App::DocumentObjectGroupPython] G4_SODIUM_MONOXIDE  # scripted group (container) (typed FeaturePython)
  Dunit = g/cm3
  Dvalue = 2.27
  Group = -> [Na_element016,O_element090]
  conduct = 2
  density = 1
  expand = 3
  formula = G4_SODIUM_MONOXIDE
  name = G4_SODIUM_MONOXIDE
  specific = 4
FEATURE [App::DocumentObjectGroupPython] Na_element017  label="Na_element : 004"  # scripted group (container) (typed FeaturePython)
  n = 1
  ref = Na_element
FEATURE [App::DocumentObjectGroupPython] N_element040  label="N_element : 018"  # scripted group (container) (typed FeaturePython)
  n = 1
  ref = N_element
FEATURE [App::DocumentObjectGroupPython] O_element091  label="O_element : 051"  # scripted group (container) (typed FeaturePython)
  n = 3
  ref = O_element
FEATURE [App::DocumentObjectGroupPython] G4_SODIUM_NITRATE  # scripted group (container) (typed FeaturePython)
  Dunit = g/cm3
  Dvalue = 2.261
  Group = -> [Na_element017,N_element040,O_element091]
  conduct = 2
  density = 1
  expand = 3
  formula = G4_SODIUM_NITRATE
  name = G4_SODIUM_NITRATE
  specific = 4
FEATURE [App::DocumentObjectGroupPython] C_element105  label="C_element : 059"  # scripted group (container) (typed FeaturePython)
  n = 14
  ref = C_element
FEATURE [App::DocumentObjectGroupPython] H_element096  label="H_element : 053"  # scripted group (container) (typed FeaturePython)
  n = 12
  ref = H_element
FEATURE [App::DocumentObjectGroupPython] G4_STILBENE  # scripted group (container) (typed FeaturePython)
  Dunit = g/cm3
  Dvalue = 0.9707
  Group = -> [C_element105,H_element096]
  conduct = 2
  density = 1
  expand = 3
  formula = G4_STILBENE
  name = G4_STILBENE
  specific = 4
FEATURE [App::DocumentObjectGroupPython] C_element106  label="C_element : 12"  # scripted group (container) (typed FeaturePython)
  n = 12
  ref = C_element
FEATURE [App::DocumentObjectGroupPython] H_element097  label="H_element : 22"  # scripted group (container) (typed FeaturePython)
  n = 22
  ref = H_element
FEATURE [App::DocumentObjectGroupPython] O_element092  label="O_element : 11"  # scripted group (container) (typed FeaturePython)
  n = 11
  ref = O_element
FEATURE [App::DocumentObjectGroupPython] G4_SUCROSE  # scripted group (container) (typed FeaturePython)
  Dunit = g/cm3
  Dvalue = 1.5805
  Group = -> [C_element106,H_element097,O_element092]
  conduct = 2
  density = 1
  expand = 3
  formula = G4_SUCROSE
  name = G4_SUCROSE
  specific = 4
FEATURE [App::DocumentObjectGroupPython] C_element107  label="C_element : 18"  # scripted group (container) (typed FeaturePython)
  n = 18
  ref = C_element
FEATURE [App::DocumentObjectGroupPython] H_element098  label="H_element : 054"  # scripted group (container) (typed FeaturePython)
  n = 14
  ref = H_element
FEATURE [App::DocumentObjectGroupPython] G4_TERPHENYL  # scripted group (container) (typed FeaturePython)
  Dunit = g/cm3
  Dvalue = 1.24
  Group = -> [C_element107,H_element098]
  conduct = 2
  density = 1
  expand = 3
  formula = G4_TERPHENYL
  name = G4_TERPHENYL
  specific = 4
FEATURE [App::DocumentObjectGroupPython] H_element099  label="H_element : 0.146"  # scripted group (container) (typed FeaturePython)
  n = 0.106
FEATURE [App::DocumentObjectGroupPython] C_element108  label="C_element : 0.883"  # scripted group (container) (typed FeaturePython)
  n = 0.099
FEATURE [App::DocumentObjectGroupPython] N_element041  label="N_element : 0.020"  # scripted group (container) (typed FeaturePython)
  n = 0.02
FEATURE [App::DocumentObjectGroupPython] O_element093  label="O_element : 0.766"  # scripted group (container) (typed FeaturePython)
  n = 0.766
FEATURE [App::DocumentObjectGroupPython] Na_element018  label="Na_element : 0.101"  # scripted group (container) (typed FeaturePython)
  n = 0.002
FEATURE [App::DocumentObjectGroupPython] P_element010  label="P_element : 0.108"  # scripted group (container) (typed FeaturePython)
  n = 0.001
FEATURE [App::DocumentObjectGroupPython] S_element021  label="S_element : 0.022"  # scripted group (container) (typed FeaturePython)
  n = 0.002
FEATURE [App::DocumentObjectGroupPython] Cl_element024  label="Cl_element : 0.002"  # scripted group (container) (typed FeaturePython)
  n = 0.002
FEATURE [App::DocumentObjectGroupPython] K_element011  label="K_element : 0.017"  # scripted group (container) (typed FeaturePython)
  n = 0.002
FEATURE [App::DocumentObjectGroupPython] G4_TESTIS_ICRP  # scripted group (container) (typed FeaturePython)
  Dunit = g/cm3
  Dvalue = 1.04
  Group = -> [H_element099,C_element108,N_element041,O_element093,Na_element018,P_element010,S_element021,Cl_element024,K_element011]
  conduct = 2
  density = 1
  expand = 3
  formula = G4_TESTIS_ICRP
  name = G4_TESTIS_ICRP
  specific = 4
FEATURE [App::DocumentObjectGroupPython] C_element109  label="C_element : 060"  # scripted group (container) (typed FeaturePython)
  n = 2
  ref = C_element
FEATURE [App::DocumentObjectGroupPython] Cl_element025  label="Cl_element : 012"  # scripted group (container) (typed FeaturePython)
  n = 4
  ref = Cl_element
FEATURE [App::DocumentObjectGroupPython] G4_TETRACHLOROETHYLENE  # scripted group (container) (typed FeaturePython)
  Dunit = g/cm3
  Dvalue = 1.625
  Group = -> [C_element109,Cl_element025]
  conduct = 2
  density = 1
  expand = 3
  formula = G4_TETRACHLOROETHYLENE
  name = G4_TETRACHLOROETHYLENE
  specific = 4
FEATURE [App::DocumentObjectGroupPython] Tl_element001  label="Tl_element : 1"  # scripted group (container) (typed FeaturePython)
  n = 1
  ref = Tl_element
FEATURE [App::DocumentObjectGroupPython] Cl_element026  label="Cl_element : 013"  # scripted group (container) (typed FeaturePython)
  n = 1
  ref = Cl_element
FEATURE [App::DocumentObjectGroupPython] G4_THALLIUM_CHLORIDE  # scripted group (container) (typed FeaturePython)
  Dunit = g/cm3
  Dvalue = 7.004
  Group = -> [Tl_element001,Cl_element026]
  conduct = 2
  density = 1
  expand = 3
  formula = G4_THALLIUM_CHLORIDE
  name = G4_THALLIUM_CHLORIDE
  specific = 4
FEATURE [App::DocumentObjectGroupPython] H_element100  label="H_element : 0.147"  # scripted group (container) (typed FeaturePython)
  n = 0.105
FEATURE [App::DocumentObjectGroupPython] C_element110  label="C_element : 0.256"  # scripted group (container) (typed FeaturePython)
  n = 0.256
FEATURE [App::DocumentObjectGroupPython] N_element042  label="N_element : 0.760"  # scripted group (container) (typed FeaturePython)
  n = 0.027
FEATURE [App::DocumentObjectGroupPython] O_element094  label="O_element : 0.602"  # scripted group (container) (typed FeaturePython)
  n = 0.602
FEATURE [App::DocumentObjectGroupPython] Na_element019  label="Na_element : 0.102"  # scripted group (container) (typed FeaturePython)
  n = 0.001
FEATURE [App::DocumentObjectGroupPython] P_element011  label="P_element : 0.109"  # scripted group (container) (typed FeaturePython)
  n = 0.002
FEATURE [App::DocumentObjectGroupPython] S_element022  label="S_element : 0.023"  # scripted group (container) (typed FeaturePython)
  n = 0.003
FEATURE [App::DocumentObjectGroupPython] Cl_element027  label="Cl_element : 0.591"  # scripted group (container) (typed FeaturePython)
  n = 0.002
FEATURE [App::DocumentObjectGroupPython] K_element012  label="K_element : 0.018"  # scripted group (container) (typed FeaturePython)
  n = 0.002
FEATURE [App::DocumentObjectGroupPython] G4_TISSUE_SOFT_ICRP  # scripted group (container) (typed FeaturePython)
  Dunit = g/cm3
  Dvalue = 1.03
  Group = -> [H_element100,C_element110,N_element042,O_element094,Na_element019,P_element011,S_element022,Cl_element027,K_element012]
  conduct = 2
  density = 1
  expand = 3
  formula = G4_TISSUE_SOFT_ICRP
  name = G4_TISSUE_SOFT_ICRP
  specific = 4
FEATURE [App::DocumentObjectGroupPython] H_element101  label="H_element : 0.148"  # scripted group (container) (typed FeaturePython)
  n = 0.101
FEATURE [App::DocumentObjectGroupPython] C_element111  label="C_element : 0.111"  # scripted group (container) (typed FeaturePython)
  n = 0.111
FEATURE [App::DocumentObjectGroupPython] N_element043  label="N_element : 0.026"  # scripted group (container) (typed FeaturePython)
  n = 0.026
FEATURE [App::DocumentObjectGroupPython] O_element095  label="O_element : 0.762"  # scripted group (container) (typed FeaturePython)
  n = 0.762
FEATURE [App::DocumentObjectGroupPython] G4_TISSUE_SOFT_ICRU_4  label="G4_TISSUE_SOFT_ICRU-4"  # scripted group (container) (typed FeaturePython)
  Dunit = g/cm3
  Dvalue = 1
  Group = -> [H_element101,C_element111,N_element043,O_element095]
  conduct = 2
  density = 1
  expand = 3
  formula = G4_TISSUE_SOFT_ICRU-4
  name = G4_TISSUE_SOFT_ICRU-4
  specific = 4
FEATURE [App::DocumentObjectGroupPython] H_element102  label="H_element : 0.149"  # scripted group (container) (typed FeaturePython)
  n = 0.101869
FEATURE [App::DocumentObjectGroupPython] C_element112  label="C_element : 0.456"  # scripted group (container) (typed FeaturePython)
  n = 0.456179
FEATURE [App::DocumentObjectGroupPython] N_element044  label="N_element : 0.761"  # scripted group (container) (typed FeaturePython)
  n = 0.035172
FEATURE [App::DocumentObjectGroupPython] O_element096  label="O_element : 0.407"  # scripted group (container) (typed FeaturePython)
  n = 0.40678
FEATURE [App::DocumentObjectGroupPython] G4_TISSUE_METHANE  label="G4_TISSUE-METHANE"  # scripted group (container) (typed FeaturePython)
  Dunit = g/cm3
  Dvalue = 0.00106409
  Group = -> [H_element102,C_element112,N_element044,O_element096]
  conduct = 2
  density = 1
  expand = 3
  formula = G4_TISSUE-METHANE
  name = G4_TISSUE-METHANE
  specific = 4
FEATURE [App::DocumentObjectGroupPython] H_element103  label="H_element : 0.103"  # scripted group (container) (typed FeaturePython)
  n = 0.102672
FEATURE [App::DocumentObjectGroupPython] C_element113  label="C_element : 0.569"  # scripted group (container) (typed FeaturePython)
  n = 0.56894
FEATURE [App::DocumentObjectGroupPython] N_element045  label="N_element : 0.762"  # scripted group (container) (typed FeaturePython)
  n = 0.035022
FEATURE [App::DocumentObjectGroupPython] O_element097  label="O_element : 0.293"  # scripted group (container) (typed FeaturePython)
  n = 0.293366
FEATURE [App::DocumentObjectGroupPython] G4_TISSUE_PROPANE  label="G4_TISSUE-PROPANE"  # scripted group (container) (typed FeaturePython)
  Dunit = g/cm3
  Dvalue = 0.00182628
  Group = -> [H_element103,C_element113,N_element045,O_element097]
  conduct = 2
  density = 1
  expand = 3
  formula = G4_TISSUE-PROPANE
  name = G4_TISSUE-PROPANE
  specific = 4
FEATURE [App::DocumentObjectGroupPython] Ti_element003  label="Ti_element : 1"  # scripted group (container) (typed FeaturePython)
  n = 1
  ref = Ti_element
FEATURE [App::DocumentObjectGroupPython] O_element098  label="O_element : 052"  # scripted group (container) (typed FeaturePython)
  n = 2
  ref = O_element
FEATURE [App::DocumentObjectGroupPython] G4_TITANIUM_DIOXIDE  # scripted group (container) (typed FeaturePython)
  Dunit = g/cm3
  Dvalue = 4.26
  Group = -> [Ti_element003,O_element098]
  conduct = 2
  density = 1
  expand = 3
  formula = G4_TITANIUM_DIOXIDE
  name = G4_TITANIUM_DIOXIDE
  specific = 4
FEATURE [App::DocumentObjectGroupPython] C_element114  label="C_element : 061"  # scripted group (container) (typed FeaturePython)
  n = 7
  ref = C_element
FEATURE [App::DocumentObjectGroupPython] H_element104  label="H_element : 055"  # scripted group (container) (typed FeaturePython)
  n = 8
  ref = H_element
FEATURE [App::DocumentObjectGroupPython] G4_TOLUENE  # scripted group (container) (typed FeaturePython)
  Dunit = g/cm3
  Dvalue = 0.8669
  Group = -> [C_element114,H_element104]
  conduct = 2
  density = 1
  expand = 3
  formula = G4_TOLUENE
  name = G4_TOLUENE
  specific = 4
FEATURE [App::DocumentObjectGroupPython] C_element115  label="C_element : 062"  # scripted group (container) (typed FeaturePython)
  n = 2
  ref = C_element
FEATURE [App::DocumentObjectGroupPython] H_element105  label="H_element : 056"  # scripted group (container) (typed FeaturePython)
  n = 1
  ref = H_element
FEATURE [App::DocumentObjectGroupPython] Cl_element028  label="Cl_element : 014"  # scripted group (container) (typed FeaturePython)
  n = 3
  ref = Cl_element
FEATURE [App::DocumentObjectGroupPython] G4_TRICHLOROETHYLENE  # scripted group (container) (typed FeaturePython)
  Dunit = g/cm3
  Dvalue = 1.46
  Group = -> [C_element115,H_element105,Cl_element028]
  conduct = 2
  density = 1
  expand = 3
  formula = G4_TRICHLOROETHYLENE
  name = G4_TRICHLOROETHYLENE
  specific = 4
FEATURE [App::DocumentObjectGroupPython] C_element116  label="C_element : 063"  # scripted group (container) (typed FeaturePython)
  n = 6
  ref = C_element
FEATURE [App::DocumentObjectGroupPython] H_element106  label="H_element : 15"  # scripted group (container) (typed FeaturePython)
  n = 15
  ref = H_element
FEATURE [App::DocumentObjectGroupPython] O_element099  label="O_element : 053"  # scripted group (container) (typed FeaturePython)
  n = 4
  ref = O_element
FEATURE [App::DocumentObjectGroupPython] P_element012  label="P_element : 1"  # scripted group (container) (typed FeaturePython)
  n = 1
  ref = P_element
FEATURE [App::DocumentObjectGroupPython] G4_TRIETHYL_PHOSPHATE  # scripted group (container) (typed FeaturePython)
  Dunit = g/cm3
  Dvalue = 1.07
  Group = -> [C_element116,H_element106,O_element099,P_element012]
  conduct = 2
  density = 1
  expand = 3
  formula = G4_TRIETHYL_PHOSPHATE
  name = G4_TRIETHYL_PHOSPHATE
  specific = 4
FEATURE [App::DocumentObjectGroupPython] W_element003  label="W_element : 003"  # scripted group (container) (typed FeaturePython)
  n = 1
  ref = W_element
FEATURE [App::DocumentObjectGroupPython] F_element017  label="F_element : 6"  # scripted group (container) (typed FeaturePython)
  n = 6
  ref = F_element
FEATURE [App::DocumentObjectGroupPython] G4_TUNGSTEN_HEXAFLUORIDE  # scripted group (container) (typed FeaturePython)
  Dunit = g/cm3
  Dvalue = 2.4
  Group = -> [W_element003,F_element017]
  conduct = 2
  density = 1
  expand = 3
  formula = G4_TUNGSTEN_HEXAFLUORIDE
  name = G4_TUNGSTEN_HEXAFLUORIDE
  specific = 4
FEATURE [App::DocumentObjectGroupPython] U_element001  label="U_element : 1"  # scripted group (container) (typed FeaturePython)
  n = 1
  ref = U_element
FEATURE [App::DocumentObjectGroupPython] C_element117  label="C_element : 064"  # scripted group (container) (typed FeaturePython)
  n = 2
  ref = C_element
FEATURE [App::DocumentObjectGroupPython] G4_URANIUM_DICARBIDE  # scripted group (container) (typed FeaturePython)
  Dunit = g/cm3
  Dvalue = 11.28
  Group = -> [U_element001,C_element117]
  conduct = 2
  density = 1
  expand = 3
  formula = G4_URANIUM_DICARBIDE
  name = G4_URANIUM_DICARBIDE
  specific = 4
FEATURE [App::DocumentObjectGroupPython] U_element002  label="U_element : 002"  # scripted group (container) (typed FeaturePython)
  n = 1
  ref = U_element
FEATURE [App::DocumentObjectGroupPython] C_element118  label="C_element : 065"  # scripted group (container) (typed FeaturePython)
  n = 1
  ref = C_element
FEATURE [App::DocumentObjectGroupPython] G4_URANIUM_MONOCARBIDE  # scripted group (container) (typed FeaturePython)
  Dunit = g/cm3
  Dvalue = 13.63
  Group = -> [U_element002,C_element118]
  conduct = 2
  density = 1
  expand = 3
  formula = G4_URANIUM_MONOCARBIDE
  name = G4_URANIUM_MONOCARBIDE
  specific = 4
FEATURE [App::DocumentObjectGroupPython] U_element003  label="U_element : 003"  # scripted group (container) (typed FeaturePython)
  n = 1
  ref = U_element
FEATURE [App::DocumentObjectGroupPython] O_element100  label="O_element : 054"  # scripted group (container) (typed FeaturePython)
  n = 2
  ref = O_element
FEATURE [App::DocumentObjectGroupPython] G4_URANIUM_OXIDE  # scripted group (container) (typed FeaturePython)
  Dunit = g/cm3
  Dvalue = 10.96
  Group = -> [U_element003,O_element100]
  conduct = 2
  density = 1
  expand = 3
  formula = G4_URANIUM_OXIDE
  name = G4_URANIUM_OXIDE
  specific = 4
FEATURE [App::DocumentObjectGroupPython] C_element119  label="C_element : 066"  # scripted group (container) (typed FeaturePython)
  n = 1
  ref = C_element
FEATURE [App::DocumentObjectGroupPython] H_element107  label="H_element : 057"  # scripted group (container) (typed FeaturePython)
  n = 4
  ref = H_element
FEATURE [App::DocumentObjectGroupPython] N_element046  label="N_element : 019"  # scripted group (container) (typed FeaturePython)
  n = 2
  ref = N_element
FEATURE [App::DocumentObjectGroupPython] O_element101  label="O_element : 055"  # scripted group (container) (typed FeaturePython)
  n = 1
  ref = O_element
FEATURE [App::DocumentObjectGroupPython] G4_UREA  # scripted group (container) (typed FeaturePython)
  Dunit = g/cm3
  Dvalue = 1.323
  Group = -> [C_element119,H_element107,N_element046,O_element101]
  conduct = 2
  density = 1
  expand = 3
  formula = G4_UREA
  name = G4_UREA
  specific = 4
FEATURE [App::DocumentObjectGroupPython] C_element120  label="C_element : 067"  # scripted group (container) (typed FeaturePython)
  n = 5
  ref = C_element
FEATURE [App::DocumentObjectGroupPython] H_element108  label="H_element : 058"  # scripted group (container) (typed FeaturePython)
  n = 11
  ref = H_element
FEATURE [App::DocumentObjectGroupPython] N_element047  label="N_element : 020"  # scripted group (container) (typed FeaturePython)
  n = 1
  ref = N_element
FEATURE [App::DocumentObjectGroupPython] O_element102  label="O_element : 056"  # scripted group (container) (typed FeaturePython)
  n = 2
  ref = O_element
FEATURE [App::DocumentObjectGroupPython] G4_VALINE  # scripted group (container) (typed FeaturePython)
  Dunit = g/cm3
  Dvalue = 1.23
  Group = -> [C_element120,H_element108,N_element047,O_element102]
  conduct = 2
  density = 1
  expand = 3
  formula = G4_VALINE
  name = G4_VALINE
  specific = 4
FEATURE [App::DocumentObjectGroupPython] H_element109  label="H_element : 0.009"  # scripted group (container) (typed FeaturePython)
  n = 0.009417
FEATURE [App::DocumentObjectGroupPython] C_element121  label="C_element : 0.281"  # scripted group (container) (typed FeaturePython)
  n = 0.280555
FEATURE [App::DocumentObjectGroupPython] F_element018  label="F_element : 0.710"  # scripted group (container) (typed FeaturePython)
  n = 0.710028
FEATURE [App::DocumentObjectGroupPython] G4_VITON  # scripted group (container) (typed FeaturePython)
  Dunit = g/cm3
  Dvalue = 1.8
  Group = -> [H_element109,C_element121,F_element018]
  conduct = 2
  density = 1
  expand = 3
  formula = G4_VITON
  name = G4_VITON
  specific = 4
FEATURE [App::DocumentObjectGroupPython] H_element110  label="H_element : 059"  # scripted group (container) (typed FeaturePython)
  n = 2
  ref = H_element
FEATURE [App::DocumentObjectGroupPython] O_element103  label="O_element : 057"  # scripted group (container) (typed FeaturePython)
  n = 1
  ref = O_element
FEATURE [App::DocumentObjectGroupPython] G4_WATER  # scripted group (container) (typed FeaturePython)
  Dunit = g/cm3
  Dvalue = 1
  Group = -> [H_element110,O_element103]
  conduct = 2
  density = 1
  expand = 3
  formula = G4_WATER
  name = G4_WATER
  specific = 4
FEATURE [App::DocumentObjectGroupPython] H_element111  label="H_element : 060"  # scripted group (container) (typed FeaturePython)
  n = 2
  ref = H_element
FEATURE [App::DocumentObjectGroupPython] O_element104  label="O_element : 058"  # scripted group (container) (typed FeaturePython)
  n = 1
  ref = O_element
FEATURE [App::DocumentObjectGroupPython] G4_WATER_VAPOR  # scripted group (container) (typed FeaturePython)
  Dunit = g/cm3
  Dvalue = 0.000756182
  Group = -> [H_element111,O_element104]
  conduct = 2
  density = 1
  expand = 3
  formula = G4_WATER_VAPOR
  name = G4_WATER_VAPOR
  specific = 4
FEATURE [App::DocumentObjectGroupPython] C_element122  label="C_element : 068"  # scripted group (container) (typed FeaturePython)
  n = 8
  ref = C_element
FEATURE [App::DocumentObjectGroupPython] H_element112  label="H_element : 061"  # scripted group (container) (typed FeaturePython)
  n = 10
  ref = H_element
FEATURE [App::DocumentObjectGroupPython] G4_XYLENE  # scripted group (container) (typed FeaturePython)
  Dunit = g/cm3
  Dvalue = 0.87
  Group = -> [C_element122,H_element112]
  conduct = 2
  density = 1
  expand = 3
  formula = G4_XYLENE
  name = G4_XYLENE
  specific = 4
FEATURE [App::DocumentObjectGroupPython] C_element123  label="C_element : 069"  # scripted group (container) (typed FeaturePython)
  n = 1
  ref = C_element
FEATURE [App::DocumentObjectGroupPython] G4_GRAPHITE  # scripted group (container) (typed FeaturePython)
  Dunit = g/cm3
  Dvalue = 2.21
  Group = -> [C_element123]
  conduct = 2
  density = 1
  expand = 3
  formula = G4_GRAPHITE
  name = G4_GRAPHITE
  specific = 4
FEATURE [App::DocumentObjectGroupPython] NIST  # scripted group (container) (typed FeaturePython)
  Group = -> [G4_A_150_TISSUE,G4_ACETONE,G4_ACETYLENE,G4_ADENINE,G4_ADIPOSE_TISSUE_ICRP,G4_AIR,G4_ALANINE,G4_ALUMINUM_OXIDE,G4_AMBER,G4_AMMONIA,G4_ANILINE,G4_ANTHRACENE,G4_B_100_BONE,G4_BAKELITE,G4_BARIUM_FLUORIDE,G4_BARIUM_SULFATE,G4_BENZENE,G4_BERYLLIUM_OXIDE,G4_BGO,G4_BLOOD_ICRP,G4_BONE_COMPACT_ICRU,G4_BONE_CORTICAL_ICRP,G4_BORON_CARBIDE,G4_BORON_OXIDE,G4_BRAIN_ICRP,G4_BUTANE,G4_N_BUTYL_ALCOHOL,G4_C_552,+152 more]
FEATURE [App::DocumentObjectGroupPython] H_element113  label="H_element : 062"  # scripted group (container) (typed FeaturePython)
  n = 1
  ref = H_element
FEATURE [App::DocumentObjectGroupPython] G4_H  # scripted group (container) (typed FeaturePython)
  Dunit = g/cm3
  Dvalue = 8.3748e-05
  Group = -> [H_element113]
  conduct = 2
  density = 1
  expand = 3
  formula = H
  name = G4_H
  specific = 4
FEATURE [App::DocumentObjectGroupPython] He_element001  label="He_element : 1"  # scripted group (container) (typed FeaturePython)
  n = 1
  ref = He_element
FEATURE [App::DocumentObjectGroupPython] G4_He  # scripted group (container) (typed FeaturePython)
  Dunit = g/cm3
  Dvalue = 0.000166322
  Group = -> [He_element001]
  conduct = 2
  density = 1
  expand = 3
  formula = He
  name = G4_He
  specific = 4
FEATURE [App::DocumentObjectGroupPython] Li_element008  label="Li_element : 008"  # scripted group (container) (typed FeaturePython)
  n = 1
  ref = Li_element
FEATURE [App::DocumentObjectGroupPython] G4_Li  # scripted group (container) (typed FeaturePython)
  Dunit = g/cm3
  Dvalue = 0.534
  Group = -> [Li_element008]
  conduct = 2
  density = 1
  expand = 3
  formula = Li
  name = G4_Li
  specific = 4
FEATURE [App::DocumentObjectGroupPython] Be_element002  label="Be_element : 002"  # scripted group (container) (typed FeaturePython)
  n = 1
  ref = Be_element
FEATURE [App::DocumentObjectGroupPython] G4_Be  # scripted group (container) (typed FeaturePython)
  Dunit = g/cm3
  Dvalue = 1.848
  Group = -> [Be_element002]
  conduct = 2
  density = 1
  expand = 3
  formula = Be
  name = G4_Be
  specific = 4
FEATURE [App::DocumentObjectGroupPython] B_element007  label="B_element : 007"  # scripted group (container) (typed FeaturePython)
  n = 1
  ref = B_element
FEATURE [App::DocumentObjectGroupPython] G4_B  # scripted group (container) (typed FeaturePython)
  Dunit = g/cm3
  Dvalue = 2.37
  Group = -> [B_element007]
  conduct = 2
  density = 1
  expand = 3
  formula = B
  name = G4_B
  specific = 4
FEATURE [App::DocumentObjectGroupPython] C_element124  label="C_element : 070"  # scripted group (container) (typed FeaturePython)
  n = 1
  ref = C_element
FEATURE [App::DocumentObjectGroupPython] G4_C  # scripted group (container) (typed FeaturePython)
  Dunit = g/cm3
  Dvalue = 2
  Group = -> [C_element124]
  conduct = 2
  density = 1
  expand = 3
  formula = C
  name = G4_C
  specific = 4
FEATURE [App::DocumentObjectGroupPython] N_element048  label="N_element : 021"  # scripted group (container) (typed FeaturePython)
  n = 1
  ref = N_element
FEATURE [App::DocumentObjectGroupPython] G4_N  # scripted group (container) (typed FeaturePython)
  Dunit = g/cm3
  Dvalue = 0.0011652
  Group = -> [N_element048]
  conduct = 2
  density = 1
  expand = 3
  formula = N
  name = G4_N
  specific = 4
FEATURE [App::DocumentObjectGroupPython] O_element105  label="O_element : 059"  # scripted group (container) (typed FeaturePython)
  n = 1
  ref = O_element
FEATURE [App::DocumentObjectGroupPython] G4_O  # scripted group (container) (typed FeaturePython)
  Dunit = g/cm3
  Dvalue = 0.00133151
  Group = -> [O_element105]
  conduct = 2
  density = 1
  expand = 3
  formula = O
  name = G4_O
  specific = 4
FEATURE [App::DocumentObjectGroupPython] F_element019  label="F_element : 008"  # scripted group (container) (typed FeaturePython)
  n = 1
  ref = F_element
FEATURE [App::DocumentObjectGroupPython] G4_F  # scripted group (container) (typed FeaturePython)
  Dunit = g/cm3
  Dvalue = 0.00158029
  Group = -> [F_element019]
  conduct = 2
  density = 1
  expand = 3
  formula = F
  name = G4_F
  specific = 4
FEATURE [App::DocumentObjectGroupPython] Ne_element001  label="Ne_element : 1"  # scripted group (container) (typed FeaturePython)
  n = 1
  ref = Ne_element
FEATURE [App::DocumentObjectGroupPython] G4_Ne  # scripted group (container) (typed FeaturePython)
  Dunit = g/cm3
  Dvalue = 0.000838505
  Group = -> [Ne_element001]
  conduct = 2
  density = 1
  expand = 3
  formula = Ne
  name = G4_Ne
  specific = 4
FEATURE [App::DocumentObjectGroupPython] Na_element020  label="Na_element : 005"  # scripted group (container) (typed FeaturePython)
  n = 1
  ref = Na_element
FEATURE [App::DocumentObjectGroupPython] G4_Na  # scripted group (container) (typed FeaturePython)
  Dunit = g/cm3
  Dvalue = 0.971
  Group = -> [Na_element020]
  conduct = 2
  density = 1
  expand = 3
  formula = Na
  name = G4_Na
  specific = 4
FEATURE [App::DocumentObjectGroupPython] Mg_element011  label="Mg_element : 005"  # scripted group (container) (typed FeaturePython)
  n = 1
  ref = Mg_element
FEATURE [App::DocumentObjectGroupPython] G4_Mg  # scripted group (container) (typed FeaturePython)
  Dunit = g/cm3
  Dvalue = 1.74
  Group = -> [Mg_element011]
  conduct = 2
  density = 1
  expand = 3
  formula = Mg
  name = G4_Mg
  specific = 4
FEATURE [App::DocumentObjectGroupPython] Al_element004  label="Al_element : 1"  # scripted group (container) (typed FeaturePython)
  n = 1
  ref = Al_element
FEATURE [App::DocumentObjectGroupPython] G4_Al  # scripted group (container) (typed FeaturePython)
  Dunit = g/cm3
  Dvalue = 2.699
  Group = -> [Al_element004]
  conduct = 2
  density = 1
  expand = 3
  formula = Al
  name = G4_Al
  specific = 4
FEATURE [App::DocumentObjectGroupPython] Si_element007  label="Si_element : 002"  # scripted group (container) (typed FeaturePython)
  n = 1
  ref = Si_element
FEATURE [App::DocumentObjectGroupPython] G4_Si  # scripted group (container) (typed FeaturePython)
  Dunit = g/cm3
  Dvalue = 2.33
  Group = -> [Si_element007]
  conduct = 2
  density = 1
  expand = 3
  formula = Si
  name = G4_Si
  specific = 4
FEATURE [App::DocumentObjectGroupPython] P_element013  label="P_element : 002"  # scripted group (container) (typed FeaturePython)
  n = 1
  ref = P_element
FEATURE [App::DocumentObjectGroupPython] G4_P  # scripted group (container) (typed FeaturePython)
  Dunit = g/cm3
  Dvalue = 2.2
  Group = -> [P_element013]
  conduct = 2
  density = 1
  expand = 3
  formula = P
  name = G4_P
  specific = 4
FEATURE [App::DocumentObjectGroupPython] S_element023  label="S_element : 007"  # scripted group (container) (typed FeaturePython)
  n = 1
  ref = S_element
FEATURE [App::DocumentObjectGroupPython] G4_S  # scripted group (container) (typed FeaturePython)
  Dunit = g/cm3
  Dvalue = 2
  Group = -> [S_element023]
  conduct = 2
  density = 1
  expand = 3
  formula = S
  name = G4_S
  specific = 4
FEATURE [App::DocumentObjectGroupPython] Cl_element029  label="Cl_element : 015"  # scripted group (container) (typed FeaturePython)
  n = 1
  ref = Cl_element
FEATURE [App::DocumentObjectGroupPython] G4_Cl  # scripted group (container) (typed FeaturePython)
  Dunit = g/cm3
  Dvalue = 0.00299473
  Group = -> [Cl_element029]
  conduct = 2
  density = 1
  expand = 3
  formula = Cl
  name = G4_Cl
  specific = 4
FEATURE [App::DocumentObjectGroupPython] Ar_element002  label="Ar_element : 1"  # scripted group (container) (typed FeaturePython)
  n = 1
  ref = Ar_element
FEATURE [App::DocumentObjectGroupPython] G4_Ar  # scripted group (container) (typed FeaturePython)
  Dunit = g/cm3
  Dvalue = 0.00166201
  Group = -> [Ar_element002]
  conduct = 2
  density = 1
  expand = 3
  formula = Ar
  name = G4_Ar
  specific = 4
FEATURE [App::DocumentObjectGroupPython] K_element013  label="K_element : 003"  # scripted group (container) (typed FeaturePython)
  n = 1
  ref = K_element
FEATURE [App::DocumentObjectGroupPython] G4_K  # scripted group (container) (typed FeaturePython)
  Dunit = g/cm3
  Dvalue = 0.862
  Group = -> [K_element013]
  conduct = 2
  density = 1
  expand = 3
  formula = K
  name = G4_K
  specific = 4
FEATURE [App::DocumentObjectGroupPython] Ca_element014  label="Ca_element : 007"  # scripted group (container) (typed FeaturePython)
  n = 1
  ref = Ca_element
FEATURE [App::DocumentObjectGroupPython] G4_Ca  # scripted group (container) (typed FeaturePython)
  Dunit = g/cm3
  Dvalue = 1.55
  Group = -> [Ca_element014]
  conduct = 2
  density = 1
  expand = 3
  formula = Ca
  name = G4_Ca
  specific = 4
FEATURE [App::DocumentObjectGroupPython] Sc_element001  label="Sc_element : 1"  # scripted group (container) (typed FeaturePython)
  n = 1
  ref = Sc_element
FEATURE [App::DocumentObjectGroupPython] G4_Sc  # scripted group (container) (typed FeaturePython)
  Dunit = g/cm3
  Dvalue = 2.989
  Group = -> [Sc_element001]
  conduct = 2
  density = 1
  expand = 3
  formula = Sc
  name = G4_Sc
  specific = 4
FEATURE [App::DocumentObjectGroupPython] Ti_element004  label="Ti_element : 002"  # scripted group (container) (typed FeaturePython)
  n = 1
  ref = Ti_element
FEATURE [App::DocumentObjectGroupPython] G4_Ti  # scripted group (container) (typed FeaturePython)
  Dunit = g/cm3
  Dvalue = 4.54
  Group = -> [Ti_element004]
  conduct = 2
  density = 1
  expand = 3
  formula = Ti
  name = G4_Ti
  specific = 4
FEATURE [App::DocumentObjectGroupPython] V_element001  label="V_element : 1"  # scripted group (container) (typed FeaturePython)
  n = 1
  ref = V_element
FEATURE [App::DocumentObjectGroupPython] G4_V  # scripted group (container) (typed FeaturePython)
  Dunit = g/cm3
  Dvalue = 6.11
  Group = -> [V_element001]
  conduct = 2
  density = 1
  expand = 3
  formula = V
  name = G4_V
  specific = 4
FEATURE [App::DocumentObjectGroupPython] Cr_element001  label="Cr_element : 1"  # scripted group (container) (typed FeaturePython)
  n = 1
  ref = Cr_element
FEATURE [App::DocumentObjectGroupPython] G4_Cr  # scripted group (container) (typed FeaturePython)
  Dunit = g/cm3
  Dvalue = 7.18
  Group = -> [Cr_element001]
  conduct = 2
  density = 1
  expand = 3
  formula = Cr
  name = G4_Cr
  specific = 4
FEATURE [App::DocumentObjectGroupPython] Mn_element001  label="Mn_element : 1"  # scripted group (container) (typed FeaturePython)
  n = 1
  ref = Mn_element
FEATURE [App::DocumentObjectGroupPython] G4_Mn  # scripted group (container) (typed FeaturePython)
  Dunit = g/cm3
  Dvalue = 7.44
  Group = -> [Mn_element001]
  conduct = 2
  density = 1
  expand = 3
  formula = Mn
  name = G4_Mn
  specific = 4
FEATURE [App::DocumentObjectGroupPython] Fe_element007  label="Fe_element : 004"  # scripted group (container) (typed FeaturePython)
  n = 1
  ref = Fe_element
FEATURE [App::DocumentObjectGroupPython] G4_Fe  # scripted group (container) (typed FeaturePython)
  Dunit = g/cm3
  Dvalue = 7.874
  Group = -> [Fe_element007]
  conduct = 2
  density = 1
  expand = 3
  formula = Fe
  name = G4_Fe
  specific = 4
FEATURE [App::DocumentObjectGroupPython] Co_element001  label="Co_element : 1"  # scripted group (container) (typed FeaturePython)
  n = 1
  ref = Co_element
FEATURE [App::DocumentObjectGroupPython] G4_Co  # scripted group (container) (typed FeaturePython)
  Dunit = g/cm3
  Dvalue = 8.9
  Group = -> [Co_element001]
  conduct = 2
  density = 1
  expand = 3
  formula = Co
  name = G4_Co
  specific = 4
FEATURE [App::DocumentObjectGroupPython] Ni_element001  label="Ni_element : 1"  # scripted group (container) (typed FeaturePython)
  n = 1
  ref = Ni_element
FEATURE [App::DocumentObjectGroupPython] G4_Ni  # scripted group (container) (typed FeaturePython)
  Dunit = g/cm3
  Dvalue = 8.902
  Group = -> [Ni_element001]
  conduct = 2
  density = 1
  expand = 3
  formula = Ni
  name = G4_Ni
  specific = 4
FEATURE [App::DocumentObjectGroupPython] Cu_element001  label="Cu_element : 1"  # scripted group (container) (typed FeaturePython)
  n = 1
  ref = Cu_element
FEATURE [App::DocumentObjectGroupPython] G4_Cu  # scripted group (container) (typed FeaturePython)
  Dunit = g/cm3
  Dvalue = 8.96
  Group = -> [Cu_element001]
  conduct = 2
  density = 1
  expand = 3
  formula = Cu
  name = G4_Cu
  specific = 4
FEATURE [App::DocumentObjectGroupPython] Zn_element001  label="Zn_element : 1"  # scripted group (container) (typed FeaturePython)
  n = 1
  ref = Zn_element
FEATURE [App::DocumentObjectGroupPython] G4_Zn  # scripted group (container) (typed FeaturePython)
  Dunit = g/cm3
  Dvalue = 7.133
  Group = -> [Zn_element001]
  conduct = 2
  density = 1
  expand = 3
  formula = Zn
  name = G4_Zn
  specific = 4
FEATURE [App::DocumentObjectGroupPython] Ga_element002  label="Ga_element : 002"  # scripted group (container) (typed FeaturePython)
  n = 1
  ref = Ga_element
FEATURE [App::DocumentObjectGroupPython] G4_Ga  # scripted group (container) (typed FeaturePython)
  Dunit = g/cm3
  Dvalue = 5.904
  Group = -> [Ga_element002]
  conduct = 2
  density = 1
  expand = 3
  formula = Ga
  name = G4_Ga
  specific = 4
FEATURE [App::DocumentObjectGroupPython] Ge_element002  label="Ge_element : 1"  # scripted group (container) (typed FeaturePython)
  n = 1
  ref = Ge_element
FEATURE [App::DocumentObjectGroupPython] G4_Ge  # scripted group (container) (typed FeaturePython)
  Dunit = g/cm3
  Dvalue = 5.323
  Group = -> [Ge_element002]
  conduct = 2
  density = 1
  expand = 3
  formula = Ge
  name = G4_Ge
  specific = 4
FEATURE [App::DocumentObjectGroupPython] As_element003  label="As_element : 002"  # scripted group (container) (typed FeaturePython)
  n = 1
  ref = As_element
FEATURE [App::DocumentObjectGroupPython] G4_As  # scripted group (container) (typed FeaturePython)
  Dunit = g/cm3
  Dvalue = 5.73
  Group = -> [As_element003]
  conduct = 2
  density = 1
  expand = 3
  formula = As
  name = G4_As
  specific = 4
FEATURE [App::DocumentObjectGroupPython] Se_element001  label="Se_element : 1"  # scripted group (container) (typed FeaturePython)
  n = 1
  ref = Se_element
FEATURE [App::DocumentObjectGroupPython] G4_Se  # scripted group (container) (typed FeaturePython)
  Dunit = g/cm3
  Dvalue = 4.5
  Group = -> [Se_element001]
  conduct = 2
  density = 1
  expand = 3
  formula = Se
  name = G4_Se
  specific = 4
FEATURE [App::DocumentObjectGroupPython] Br_element007  label="Br_element : 004"  # scripted group (container) (typed FeaturePython)
  n = 1
  ref = Br_element
FEATURE [App::DocumentObjectGroupPython] G4_Br  # scripted group (container) (typed FeaturePython)
  Dunit = g/cm3
  Dvalue = 0.0070721
  Group = -> [Br_element007]
  conduct = 2
  density = 1
  expand = 3
  formula = Br
  name = G4_Br
  specific = 4
FEATURE [App::DocumentObjectGroupPython] Kr_element001  label="Kr_element : 1"  # scripted group (container) (typed FeaturePython)
  n = 1
  ref = Kr_element
FEATURE [App::DocumentObjectGroupPython] G4_Kr  # scripted group (container) (typed FeaturePython)
  Dunit = g/cm3
  Dvalue = 0.00347832
  Group = -> [Kr_element001]
  conduct = 2
  density = 1
  expand = 3
  formula = Kr
  name = G4_Kr
  specific = 4
FEATURE [App::DocumentObjectGroupPython] Rb_element001  label="Rb_element : 1"  # scripted group (container) (typed FeaturePython)
  n = 1
  ref = Rb_element
FEATURE [App::DocumentObjectGroupPython] G4_Rb  # scripted group (container) (typed FeaturePython)
  Dunit = g/cm3
  Dvalue = 1.532
  Group = -> [Rb_element001]
  conduct = 2
  density = 1
  expand = 3
  formula = Rb
  name = G4_Rb
  specific = 4
FEATURE [App::DocumentObjectGroupPython] Sr_element001  label="Sr_element : 1"  # scripted group (container) (typed FeaturePython)
  n = 1
  ref = Sr_element
FEATURE [App::DocumentObjectGroupPython] G4_Sr  # scripted group (container) (typed FeaturePython)
  Dunit = g/cm3
  Dvalue = 2.54
  Group = -> [Sr_element001]
  conduct = 2
  density = 1
  expand = 3
  formula = Sr
  name = G4_Sr
  specific = 4
FEATURE [App::DocumentObjectGroupPython] Y_element001  label="Y_element : 1"  # scripted group (container) (typed FeaturePython)
  n = 1
  ref = Y_element
FEATURE [App::DocumentObjectGroupPython] G4_Y  # scripted group (container) (typed FeaturePython)
  Dunit = g/cm3
  Dvalue = 4.469
  Group = -> [Y_element001]
  conduct = 2
  density = 1
  expand = 3
  formula = Y
  name = G4_Y
  specific = 4
FEATURE [App::DocumentObjectGroupPython] Zr_element001  label="Zr_element : 1"  # scripted group (container) (typed FeaturePython)
  n = 1
  ref = Zr_element
FEATURE [App::DocumentObjectGroupPython] G4_Zr  # scripted group (container) (typed FeaturePython)
  Dunit = g/cm3
  Dvalue = 6.506
  Group = -> [Zr_element001]
  conduct = 2
  density = 1
  expand = 3
  formula = Zr
  name = G4_Zr
  specific = 4
FEATURE [App::DocumentObjectGroupPython] Nb_element001  label="Nb_element : 1"  # scripted group (container) (typed FeaturePython)
  n = 1
  ref = Nb_element
FEATURE [App::DocumentObjectGroupPython] G4_Nb  # scripted group (container) (typed FeaturePython)
  Dunit = g/cm3
  Dvalue = 8.57
  Group = -> [Nb_element001]
  conduct = 2
  density = 1
  expand = 3
  formula = Nb
  name = G4_Nb
  specific = 4
FEATURE [App::DocumentObjectGroupPython] Mo_element001  label="Mo_element : 1"  # scripted group (container) (typed FeaturePython)
  n = 1
  ref = Mo_element
FEATURE [App::DocumentObjectGroupPython] G4_Mo  # scripted group (container) (typed FeaturePython)
  Dunit = g/cm3
  Dvalue = 10.22
  Group = -> [Mo_element001]
  conduct = 2
  density = 1
  expand = 3
  formula = Mo
  name = G4_Mo
  specific = 4
FEATURE [App::DocumentObjectGroupPython] Tc_element001  label="Tc_element : 1"  # scripted group (container) (typed FeaturePython)
  n = 1
  ref = Tc_element
FEATURE [App::DocumentObjectGroupPython] G4_Tc  # scripted group (container) (typed FeaturePython)
  Dunit = g/cm3
  Dvalue = 11.5
  Group = -> [Tc_element001]
  conduct = 2
  density = 1
  expand = 3
  formula = Tc
  name = G4_Tc
  specific = 4
FEATURE [App::DocumentObjectGroupPython] Ru_element001  label="Ru_element : 1"  # scripted group (container) (typed FeaturePython)
  n = 1
  ref = Ru_element
FEATURE [App::DocumentObjectGroupPython] G4_Ru  # scripted group (container) (typed FeaturePython)
  Dunit = g/cm3
  Dvalue = 12.41
  Group = -> [Ru_element001]
  conduct = 2
  density = 1
  expand = 3
  formula = Ru
  name = G4_Ru
  specific = 4
FEATURE [App::DocumentObjectGroupPython] Rh_element001  label="Rh_element : 1"  # scripted group (container) (typed FeaturePython)
  n = 1
  ref = Rh_element
FEATURE [App::DocumentObjectGroupPython] G4_Rh  # scripted group (container) (typed FeaturePython)
  Dunit = g/cm3
  Dvalue = 12.41
  Group = -> [Rh_element001]
  conduct = 2
  density = 1
  expand = 3
  formula = Rh
  name = G4_Rh
  specific = 4
FEATURE [App::DocumentObjectGroupPython] Pd_element001  label="Pd_element : 1"  # scripted group (container) (typed FeaturePython)
  n = 1
  ref = Pd_element
FEATURE [App::DocumentObjectGroupPython] G4_Pd  # scripted group (container) (typed FeaturePython)
  Dunit = g/cm3
  Dvalue = 12.02
  Group = -> [Pd_element001]
  conduct = 2
  density = 1
  expand = 3
  formula = Pd
  name = G4_Pd
  specific = 4
FEATURE [App::DocumentObjectGroupPython] Ag_element006  label="Ag_element : 004"  # scripted group (container) (typed FeaturePython)
  n = 1
  ref = Ag_element
FEATURE [App::DocumentObjectGroupPython] G4_Ag  # scripted group (container) (typed FeaturePython)
  Dunit = g/cm3
  Dvalue = 10.5
  Group = -> [Ag_element006]
  conduct = 2
  density = 1
  expand = 3
  formula = Ag
  name = G4_Ag
  specific = 4
FEATURE [App::DocumentObjectGroupPython] Cd_element003  label="Cd_element : 003"  # scripted group (container) (typed FeaturePython)
  n = 1
  ref = Cd_element
FEATURE [App::DocumentObjectGroupPython] G4_Cd  # scripted group (container) (typed FeaturePython)
  Dunit = g/cm3
  Dvalue = 8.65
  Group = -> [Cd_element003]
  conduct = 2
  density = 1
  expand = 3
  formula = Cd
  name = G4_Cd
  specific = 4
FEATURE [App::DocumentObjectGroupPython] In_element001  label="In_element : 1"  # scripted group (container) (typed FeaturePython)
  n = 1
  ref = In_element
FEATURE [App::DocumentObjectGroupPython] G4_In  # scripted group (container) (typed FeaturePython)
  Dunit = g/cm3
  Dvalue = 7.31
  Group = -> [In_element001]
  conduct = 2
  density = 1
  expand = 3
  formula = In
  name = G4_In
  specific = 4
FEATURE [App::DocumentObjectGroupPython] Sn_element001  label="Sn_element : 1"  # scripted group (container) (typed FeaturePython)
  n = 1
  ref = Sn_element
FEATURE [App::DocumentObjectGroupPython] G4_Sn  # scripted group (container) (typed FeaturePython)
  Dunit = g/cm3
  Dvalue = 7.31
  Group = -> [Sn_element001]
  conduct = 2
  density = 1
  expand = 3
  formula = Sn
  name = G4_Sn
  specific = 4
FEATURE [App::DocumentObjectGroupPython] Sb_element001  label="Sb_element : 1"  # scripted group (container) (typed FeaturePython)
  n = 1
  ref = Sb_element
FEATURE [App::DocumentObjectGroupPython] G4_Sb  # scripted group (container) (typed FeaturePython)
  Dunit = g/cm3
  Dvalue = 6.691
  Group = -> [Sb_element001]
  conduct = 2
  density = 1
  expand = 3
  formula = Sb
  name = G4_Sb
  specific = 4
FEATURE [App::DocumentObjectGroupPython] Te_element002  label="Te_element : 002"  # scripted group (container) (typed FeaturePython)
  n = 1
  ref = Te_element
FEATURE [App::DocumentObjectGroupPython] G4_Te  # scripted group (container) (typed FeaturePython)
  Dunit = g/cm3
  Dvalue = 6.24
  Group = -> [Te_element002]
  conduct = 2
  density = 1
  expand = 3
  formula = Te
  name = G4_Te
  specific = 4
FEATURE [App::DocumentObjectGroupPython] I_element010  label="I_element : 006"  # scripted group (container) (typed FeaturePython)
  n = 1
  ref = I_element
FEATURE [App::DocumentObjectGroupPython] G4_I  # scripted group (container) (typed FeaturePython)
  Dunit = g/cm3
  Dvalue = 4.93
  Group = -> [I_element010]
  conduct = 2
  density = 1
  expand = 3
  formula = I
  name = G4_I
  specific = 4
FEATURE [App::DocumentObjectGroupPython] Xe_element001  label="Xe_element : 1"  # scripted group (container) (typed FeaturePython)
  n = 1
  ref = Xe_element
FEATURE [App::DocumentObjectGroupPython] G4_Xe  # scripted group (container) (typed FeaturePython)
  Dunit = g/cm3
  Dvalue = 0.00548536
  Group = -> [Xe_element001]
  conduct = 2
  density = 1
  expand = 3
  formula = Xe
  name = G4_Xe
  specific = 4
FEATURE [App::DocumentObjectGroupPython] Cs_element003  label="Cs_element : 003"  # scripted group (container) (typed FeaturePython)
  n = 1
  ref = Cs_element
FEATURE [App::DocumentObjectGroupPython] G4_Cs  # scripted group (container) (typed FeaturePython)
  Dunit = g/cm3
  Dvalue = 1.873
  Group = -> [Cs_element003]
  conduct = 2
  density = 1
  expand = 3
  formula = Cs
  name = G4_Cs
  specific = 4
FEATURE [App::DocumentObjectGroupPython] Ba_element003  label="Ba_element : 003"  # scripted group (container) (typed FeaturePython)
  n = 1
  ref = Ba_element
FEATURE [App::DocumentObjectGroupPython] G4_Ba  # scripted group (container) (typed FeaturePython)
  Dunit = g/cm3
  Dvalue = 3.5
  Group = -> [Ba_element003]
  conduct = 2
  density = 1
  expand = 3
  formula = Ba
  name = G4_Ba
  specific = 4
FEATURE [App::DocumentObjectGroupPython] La_element003  label="La_element : 003"  # scripted group (container) (typed FeaturePython)
  n = 1
  ref = La_element
FEATURE [App::DocumentObjectGroupPython] G4_La  # scripted group (container) (typed FeaturePython)
  Dunit = g/cm3
  Dvalue = 6.154
  Group = -> [La_element003]
  conduct = 2
  density = 1
  expand = 3
  formula = La
  name = G4_La
  specific = 4
FEATURE [App::DocumentObjectGroupPython] Ce_element002  label="Ce_element : 1"  # scripted group (container) (typed FeaturePython)
  n = 1
  ref = Ce_element
FEATURE [App::DocumentObjectGroupPython] G4_Ce  # scripted group (container) (typed FeaturePython)
  Dunit = g/cm3
  Dvalue = 6.657
  Group = -> [Ce_element002]
  conduct = 2
  density = 1
  expand = 3
  formula = Ce
  name = G4_Ce
  specific = 4
FEATURE [App::DocumentObjectGroupPython] Pr_element001  label="Pr_element : 1"  # scripted group (container) (typed FeaturePython)
  n = 1
  ref = Pr_element
FEATURE [App::DocumentObjectGroupPython] G4_Pr  # scripted group (container) (typed FeaturePython)
  Dunit = g/cm3
  Dvalue = 6.71
  Group = -> [Pr_element001]
  conduct = 2
  density = 1
  expand = 3
  formula = Pr
  name = G4_Pr
  specific = 4
FEATURE [App::DocumentObjectGroupPython] Nd_element001  label="Nd_element : 1"  # scripted group (container) (typed FeaturePython)
  n = 1
  ref = Nd_element
FEATURE [App::DocumentObjectGroupPython] G4_Nd  # scripted group (container) (typed FeaturePython)
  Dunit = g/cm3
  Dvalue = 6.9
  Group = -> [Nd_element001]
  conduct = 2
  density = 1
  expand = 3
  formula = Nd
  name = G4_Nd
  specific = 4
FEATURE [App::DocumentObjectGroupPython] Pm_element001  label="Pm_element : 1"  # scripted group (container) (typed FeaturePython)
  n = 1
  ref = Pm_element
FEATURE [App::DocumentObjectGroupPython] G4_Pm  # scripted group (container) (typed FeaturePython)
  Dunit = g/cm3
  Dvalue = 7.22
  Group = -> [Pm_element001]
  conduct = 2
  density = 1
  expand = 3
  formula = Pm
  name = G4_Pm
  specific = 4
FEATURE [App::DocumentObjectGroupPython] Sm_element001  label="Sm_element : 1"  # scripted group (container) (typed FeaturePython)
  n = 1
  ref = Sm_element
FEATURE [App::DocumentObjectGroupPython] G4_Sm  # scripted group (container) (typed FeaturePython)
  Dunit = g/cm3
  Dvalue = 7.46
  Group = -> [Sm_element001]
  conduct = 2
  density = 1
  expand = 3
  formula = Sm
  name = G4_Sm
  specific = 4
FEATURE [App::DocumentObjectGroupPython] Eu_element001  label="Eu_element : 1"  # scripted group (container) (typed FeaturePython)
  n = 1
  ref = Eu_element
FEATURE [App::DocumentObjectGroupPython] G4_Eu  # scripted group (container) (typed FeaturePython)
  Dunit = g/cm3
  Dvalue = 5.243
  Group = -> [Eu_element001]
  conduct = 2
  density = 1
  expand = 3
  formula = Eu
  name = G4_Eu
  specific = 4
FEATURE [App::DocumentObjectGroupPython] Gd_element002  label="Gd_element : 1"  # scripted group (container) (typed FeaturePython)
  n = 1
  ref = Gd_element
FEATURE [App::DocumentObjectGroupPython] G4_Gd  # scripted group (container) (typed FeaturePython)
  Dunit = g/cm3
  Dvalue = 7.9004
  Group = -> [Gd_element002]
  conduct = 2
  density = 1
  expand = 3
  formula = Gd
  name = G4_Gd
  specific = 4
FEATURE [App::DocumentObjectGroupPython] Tb_element001  label="Tb_element : 1"  # scripted group (container) (typed FeaturePython)
  n = 1
  ref = Tb_element
FEATURE [App::DocumentObjectGroupPython] G4_Tb  # scripted group (container) (typed FeaturePython)
  Dunit = g/cm3
  Dvalue = 8.229
  Group = -> [Tb_element001]
  conduct = 2
  density = 1
  expand = 3
  formula = Tb
  name = G4_Tb
  specific = 4
FEATURE [App::DocumentObjectGroupPython] Dy_element001  label="Dy_element : 1"  # scripted group (container) (typed FeaturePython)
  n = 1
  ref = Dy_element
FEATURE [App::DocumentObjectGroupPython] G4_Dy  # scripted group (container) (typed FeaturePython)
  Dunit = g/cm3
  Dvalue = 8.55
  Group = -> [Dy_element001]
  conduct = 2
  density = 1
  expand = 3
  formula = Dy
  name = G4_Dy
  specific = 4
FEATURE [App::DocumentObjectGroupPython] Ho_element001  label="Ho_element : 1"  # scripted group (container) (typed FeaturePython)
  n = 1
  ref = Ho_element
FEATURE [App::DocumentObjectGroupPython] G4_Ho  # scripted group (container) (typed FeaturePython)
  Dunit = g/cm3
  Dvalue = 8.795
  Group = -> [Ho_element001]
  conduct = 2
  density = 1
  expand = 3
  formula = Ho
  name = G4_Ho
  specific = 4
FEATURE [App::DocumentObjectGroupPython] Er_element001  label="Er_element : 1"  # scripted group (container) (typed FeaturePython)
  n = 1
  ref = Er_element
FEATURE [App::DocumentObjectGroupPython] G4_Er  # scripted group (container) (typed FeaturePython)
  Dunit = g/cm3
  Dvalue = 9.066
  Group = -> [Er_element001]
  conduct = 2
  density = 1
  expand = 3
  formula = Er
  name = G4_Er
  specific = 4
FEATURE [App::DocumentObjectGroupPython] Tm_element001  label="Tm_element : 1"  # scripted group (container) (typed FeaturePython)
  n = 1
  ref = Tm_element
FEATURE [App::DocumentObjectGroupPython] G4_Tm  # scripted group (container) (typed FeaturePython)
  Dunit = g/cm3
  Dvalue = 9.321
  Group = -> [Tm_element001]
  conduct = 2
  density = 1
  expand = 3
  formula = Tm
  name = G4_Tm
  specific = 4
FEATURE [App::DocumentObjectGroupPython] Yb_element001  label="Yb_element : 1"  # scripted group (container) (typed FeaturePython)
  n = 1
  ref = Yb_element
FEATURE [App::DocumentObjectGroupPython] G4_Yb  # scripted group (container) (typed FeaturePython)
  Dunit = g/cm3
  Dvalue = 6.73
  Group = -> [Yb_element001]
  conduct = 2
  density = 1
  expand = 3
  formula = Yb
  name = G4_Yb
  specific = 4
FEATURE [App::DocumentObjectGroupPython] Lu_element001  label="Lu_element : 1"  # scripted group (container) (typed FeaturePython)
  n = 1
  ref = Lu_element
FEATURE [App::DocumentObjectGroupPython] G4_Lu  # scripted group (container) (typed FeaturePython)
  Dunit = g/cm3
  Dvalue = 9.84
  Group = -> [Lu_element001]
  conduct = 2
  density = 1
  expand = 3
  formula = Lu
  name = G4_Lu
  specific = 4
FEATURE [App::DocumentObjectGroupPython] Hf_element001  label="Hf_element : 1"  # scripted group (container) (typed FeaturePython)
  n = 1
  ref = Hf_element
FEATURE [App::DocumentObjectGroupPython] G4_Hf  # scripted group (container) (typed FeaturePython)
  Dunit = g/cm3
  Dvalue = 13.31
  Group = -> [Hf_element001]
  conduct = 2
  density = 1
  expand = 3
  formula = Hf
  name = G4_Hf
  specific = 4
FEATURE [App::DocumentObjectGroupPython] Ta_element001  label="Ta_element : 1"  # scripted group (container) (typed FeaturePython)
  n = 1
  ref = Ta_element
FEATURE [App::DocumentObjectGroupPython] G4_Ta  # scripted group (container) (typed FeaturePython)
  Dunit = g/cm3
  Dvalue = 16.654
  Group = -> [Ta_element001]
  conduct = 2
  density = 1
  expand = 3
  formula = Ta
  name = G4_Ta
  specific = 4
FEATURE [App::DocumentObjectGroupPython] W_element004  label="W_element : 004"  # scripted group (container) (typed FeaturePython)
  n = 1
  ref = W_element
FEATURE [App::DocumentObjectGroupPython] G4_W  # scripted group (container) (typed FeaturePython)
  Dunit = g/cm3
  Dvalue = 19.3
  Group = -> [W_element004]
  conduct = 2
  density = 1
  expand = 3
  formula = W
  name = G4_W
  specific = 4
FEATURE [App::DocumentObjectGroupPython] Re_element001  label="Re_element : 1"  # scripted group (container) (typed FeaturePython)
  n = 1
  ref = Re_element
FEATURE [App::DocumentObjectGroupPython] G4_Re  # scripted group (container) (typed FeaturePython)
  Dunit = g/cm3
  Dvalue = 21.02
  Group = -> [Re_element001]
  conduct = 2
  density = 1
  expand = 3
  formula = Re
  name = G4_Re
  specific = 4
FEATURE [App::DocumentObjectGroupPython] Os_element001  label="Os_element : 1"  # scripted group (container) (typed FeaturePython)
  n = 1
  ref = Os_element
FEATURE [App::DocumentObjectGroupPython] G4_Os  # scripted group (container) (typed FeaturePython)
  Dunit = g/cm3
  Dvalue = 22.57
  Group = -> [Os_element001]
  conduct = 2
  density = 1
  expand = 3
  formula = Os
  name = G4_Os
  specific = 4
FEATURE [App::DocumentObjectGroupPython] Ir_element001  label="Ir_element : 1"  # scripted group (container) (typed FeaturePython)
  n = 1
  ref = Ir_element
FEATURE [App::DocumentObjectGroupPython] G4_Ir  # scripted group (container) (typed FeaturePython)
  Dunit = g/cm3
  Dvalue = 22.42
  Group = -> [Ir_element001]
  conduct = 2
  density = 1
  expand = 3
  formula = Ir
  name = G4_Ir
  specific = 4
FEATURE [App::DocumentObjectGroupPython] Pt_element001  label="Pt_element : 1"  # scripted group (container) (typed FeaturePython)
  n = 1
  ref = Pt_element
FEATURE [App::DocumentObjectGroupPython] G4_Pt  # scripted group (container) (typed FeaturePython)
  Dunit = g/cm3
  Dvalue = 21.45
  Group = -> [Pt_element001]
  conduct = 2
  density = 1
  expand = 3
  formula = Pt
  name = G4_Pt
  specific = 4
FEATURE [App::DocumentObjectGroupPython] Au_element001  label="Au_element : 1"  # scripted group (container) (typed FeaturePython)
  n = 1
  ref = Au_element
FEATURE [App::DocumentObjectGroupPython] G4_Au  # scripted group (container) (typed FeaturePython)
  Dunit = g/cm3
  Dvalue = 19.32
  Group = -> [Au_element001]
  conduct = 2
  density = 1
  expand = 3
  formula = Au
  name = G4_Au
  specific = 4
FEATURE [App::DocumentObjectGroupPython] Hg_element002  label="Hg_element : 002"  # scripted group (container) (typed FeaturePython)
  n = 1
  ref = Hg_element
FEATURE [App::DocumentObjectGroupPython] G4_Hg  # scripted group (container) (typed FeaturePython)
  Dunit = g/cm3
  Dvalue = 13.546
  Group = -> [Hg_element002]
  conduct = 2
  density = 1
  expand = 3
  formula = Hg
  name = G4_Hg
  specific = 4
FEATURE [App::DocumentObjectGroupPython] Tl_element002  label="Tl_element : 002"  # scripted group (container) (typed FeaturePython)
  n = 1
  ref = Tl_element
FEATURE [App::DocumentObjectGroupPython] G4_Tl  # scripted group (container) (typed FeaturePython)
  Dunit = g/cm3
  Dvalue = 11.72
  Group = -> [Tl_element002]
  conduct = 2
  density = 1
  expand = 3
  formula = Tl
  name = G4_Tl
  specific = 4
FEATURE [App::DocumentObjectGroupPython] Pb_element003  label="Pb_element : 1"  # scripted group (container) (typed FeaturePython)
  n = 1
  ref = Pb_element
FEATURE [App::DocumentObjectGroupPython] G4_Pb  # scripted group (container) (typed FeaturePython)
  Dunit = g/cm3
  Dvalue = 11.35
  Group = -> [Pb_element003]
  conduct = 2
  density = 1
  expand = 3
  formula = Pb
  name = G4_Pb
  specific = 4
FEATURE [App::DocumentObjectGroupPython] Bi_element002  label="Bi_element : 1"  # scripted group (container) (typed FeaturePython)
  n = 1
  ref = Bi_element
FEATURE [App::DocumentObjectGroupPython] G4_Bi  # scripted group (container) (typed FeaturePython)
  Dunit = g/cm3
  Dvalue = 9.747
  Group = -> [Bi_element002]
  conduct = 2
  density = 1
  expand = 3
  formula = Bi
  name = G4_Bi
  specific = 4
FEATURE [App::DocumentObjectGroupPython] Po_element001  label="Po_element : 1"  # scripted group (container) (typed FeaturePython)
  n = 1
  ref = Po_element
FEATURE [App::DocumentObjectGroupPython] G4_Po  # scripted group (container) (typed FeaturePython)
  Dunit = g/cm3
  Dvalue = 9.32
  Group = -> [Po_element001]
  conduct = 2
  density = 1
  expand = 3
  formula = Po
  name = G4_Po
  specific = 4
FEATURE [App::DocumentObjectGroupPython] At_element001  label="At_element : 1"  # scripted group (container) (typed FeaturePython)
  n = 1
  ref = At_element
FEATURE [App::DocumentObjectGroupPython] G4_At  # scripted group (container) (typed FeaturePython)
  Dunit = g/cm3
  Dvalue = 9.32
  Group = -> [At_element001]
  conduct = 2
  density = 1
  expand = 3
  formula = At
  name = G4_At
  specific = 4
FEATURE [App::DocumentObjectGroupPython] Rn_element001  label="Rn_element : 1"  # scripted group (container) (typed FeaturePython)
  n = 1
  ref = Rn_element
FEATURE [App::DocumentObjectGroupPython] G4_Rn  # scripted group (container) (typed FeaturePython)
  Dunit = g/cm3
  Dvalue = 0.00900662
  Group = -> [Rn_element001]
  conduct = 2
  density = 1
  expand = 3
  formula = Rn
  name = G4_Rn
  specific = 4
FEATURE [App::DocumentObjectGroupPython] Fr_element001  label="Fr_element : 1"  # scripted group (container) (typed FeaturePython)
  n = 1
  ref = Fr_element
FEATURE [App::DocumentObjectGroupPython] G4_Fr  # scripted group (container) (typed FeaturePython)
  Dunit = g/cm3
  Dvalue = 1
  Group = -> [Fr_element001]
  conduct = 2
  density = 1
  expand = 3
  formula = Fr
  name = G4_Fr
  specific = 4
FEATURE [App::DocumentObjectGroupPython] Ra_element001  label="Ra_element : 1"  # scripted group (container) (typed FeaturePython)
  n = 1
  ref = Ra_element
FEATURE [App::DocumentObjectGroupPython] G4_Ra  # scripted group (container) (typed FeaturePython)
  Dunit = g/cm3
  Dvalue = 5
  Group = -> [Ra_element001]
  conduct = 2
  density = 1
  expand = 3
  formula = Ra
  name = G4_Ra
  specific = 4
FEATURE [App::DocumentObjectGroupPython] Ac_element001  label="Ac_element : 1"  # scripted group (container) (typed FeaturePython)
  n = 1
  ref = Ac_element
FEATURE [App::DocumentObjectGroupPython] G4_Ac  # scripted group (container) (typed FeaturePython)
  Dunit = g/cm3
  Dvalue = 10.07
  Group = -> [Ac_element001]
  conduct = 2
  density = 1
  expand = 3
  formula = Ac
  name = G4_Ac
  specific = 4
FEATURE [App::DocumentObjectGroupPython] Th_element001  label="Th_element : 1"  # scripted group (container) (typed FeaturePython)
  n = 1
  ref = Th_element
FEATURE [App::DocumentObjectGroupPython] G4_Th  # scripted group (container) (typed FeaturePython)
  Dunit = g/cm3
  Dvalue = 11.72
  Group = -> [Th_element001]
  conduct = 2
  density = 1
  expand = 3
  formula = Th
  name = G4_Th
  specific = 4
FEATURE [App::DocumentObjectGroupPython] Pa_element001  label="Pa_element : 1"  # scripted group (container) (typed FeaturePython)
  n = 1
  ref = Pa_element
FEATURE [App::DocumentObjectGroupPython] G4_Pa  # scripted group (container) (typed FeaturePython)
  Dunit = g/cm3
  Dvalue = 15.37
  Group = -> [Pa_element001]
  conduct = 2
  density = 1
  expand = 3
  formula = Pa
  name = G4_Pa
  specific = 4
FEATURE [App::DocumentObjectGroupPython] U_element004  label="U_element : 004"  # scripted group (container) (typed FeaturePython)
  n = 1
  ref = U_element
FEATURE [App::DocumentObjectGroupPython] G4_U  # scripted group (container) (typed FeaturePython)
  Dunit = g/cm3
  Dvalue = 18.95
  Group = -> [U_element004]
  conduct = 2
  density = 1
  expand = 3
  formula = U
  name = G4_U
  specific = 4
FEATURE [App::DocumentObjectGroupPython] Np_element001  label="Np_element : 1"  # scripted group (container) (typed FeaturePython)
  n = 1
  ref = Np_element
FEATURE [App::DocumentObjectGroupPython] G4_Np  # scripted group (container) (typed FeaturePython)
  Dunit = g/cm3
  Dvalue = 20.25
  Group = -> [Np_element001]
  conduct = 2
  density = 1
  expand = 3
  formula = Np
  name = G4_Np
  specific = 4
FEATURE [App::DocumentObjectGroupPython] Pu_element002  label="Pu_element : 002"  # scripted group (container) (typed FeaturePython)
  n = 1
  ref = Pu_element
FEATURE [App::DocumentObjectGroupPython] G4_Pu  # scripted group (container) (typed FeaturePython)
  Dunit = g/cm3
  Dvalue = 19.84
  Group = -> [Pu_element002]
  conduct = 2
  density = 1
  expand = 3
  formula = Pu
  name = G4_Pu
  specific = 4
FEATURE [App::DocumentObjectGroupPython] Am_element001  label="Am_element : 1"  # scripted group (container) (typed FeaturePython)
  n = 1
  ref = Am_element
FEATURE [App::DocumentObjectGroupPython] G4_Am  # scripted group (container) (typed FeaturePython)
  Dunit = g/cm3
  Dvalue = 13.67
  Group = -> [Am_element001]
  conduct = 2
  density = 1
  expand = 3
  formula = Am
  name = G4_Am
  specific = 4
FEATURE [App::DocumentObjectGroupPython] Cm_element001  label="Cm_element : 1"  # scripted group (container) (typed FeaturePython)
  n = 1
  ref = Cm_element
FEATURE [App::DocumentObjectGroupPython] G4_Cm  # scripted group (container) (typed FeaturePython)
  Dunit = g/cm3
  Dvalue = 13.51
  Group = -> [Cm_element001]
  conduct = 2
  density = 1
  expand = 3
  formula = Cm
  name = G4_Cm
  specific = 4
FEATURE [App::DocumentObjectGroupPython] Bk_element001  label="Bk_element : 1"  # scripted group (container) (typed FeaturePython)
  n = 1
  ref = Bk_element
FEATURE [App::DocumentObjectGroupPython] G4_Bk  # scripted group (container) (typed FeaturePython)
  Dunit = g/cm3
  Dvalue = 14
  Group = -> [Bk_element001]
  conduct = 2
  density = 1
  expand = 3
  formula = Bk
  name = G4_Bk
  specific = 4
FEATURE [App::DocumentObjectGroupPython] Cf_element001  label="Cf_element : 1"  # scripted group (container) (typed FeaturePython)
  n = 1
  ref = Cf_element
FEATURE [App::DocumentObjectGroupPython] G4_Cf  # scripted group (container) (typed FeaturePython)
  Dunit = g/cm3
  Dvalue = 10
  Group = -> [Cf_element001]
  conduct = 2
  density = 1
  expand = 3
  formula = Cf
  name = G4_Cf
  specific = 4
FEATURE [App::DocumentObjectGroupPython] Element  # scripted group (container) (typed FeaturePython)
  Group = -> [G4_H,G4_He,G4_Li,G4_Be,G4_B,G4_C,G4_N,G4_O,G4_F,G4_Ne,G4_Na,G4_Mg,G4_Al,G4_Si,G4_P,G4_S,G4_Cl,G4_Ar,G4_K,G4_Ca,G4_Sc,G4_Ti,G4_V,G4_Cr,G4_Mn,G4_Fe,G4_Co,G4_Ni,G4_Cu,G4_Zn,G4_Ga,G4_Ge,G4_As,G4_Se,G4_Br,G4_Kr,G4_Rb,G4_Sr,G4_Y,G4_Zr,G4_Nb,G4_Mo,G4_Tc,G4_Ru,G4_Rh,G4_Pd,G4_Ag,G4_Cd,G4_In,G4_Sn,G4_Sb,G4_Te,G4_I,G4_Xe,G4_Cs,G4_Ba,G4_La,G4_Ce,G4_Pr,G4_Nd,G4_Pm,G4_Sm,G4_Eu,G4_Gd,G4_Tb,G4_Dy,G4_Ho,G4_Er,+30 more]
FEATURE [App::DocumentObjectGroupPython] H_element114  label="H_element : 063"  # scripted group (container) (typed FeaturePython)
  n = 2
  ref = H_element
FEATURE [App::DocumentObjectGroupPython] G4_lH2  # scripted group (container) (typed FeaturePython)
  Dunit = g/cm3
  Dvalue = 0.0708
  Group = -> [H_element114]
  conduct = 2
  density = 1
  expand = 3
  formula = G4_lH2
  name = G4_lH2
  specific = 4
FEATURE [App::DocumentObjectGroupPython] N_element049  label="N_element : 022"  # scripted group (container) (typed FeaturePython)
  n = 2
  ref = N_element
FEATURE [App::DocumentObjectGroupPython] G4_lN2  # scripted group (container) (typed FeaturePython)
  Dunit = g/cm3
  Dvalue = 0.807
  Group = -> [N_element049]
  conduct = 2
  density = 1
  expand = 3
  formula = G4_lN2
  name = G4_lN2
  specific = 4
FEATURE [App::DocumentObjectGroupPython] O_element106  label="O_element : 060"  # scripted group (container) (typed FeaturePython)
  n = 2
  ref = O_element
FEATURE [App::DocumentObjectGroupPython] G4_lO2  # scripted group (container) (typed FeaturePython)
  Dunit = g/cm3
  Dvalue = 1.141
  Group = -> [O_element106]
  conduct = 2
  density = 1
  expand = 3
  formula = G4_lO2
  name = G4_lO2
  specific = 4
FEATURE [App::DocumentObjectGroupPython] Ar  label="Ar : 1"  # scripted group (container) (typed FeaturePython)
  n = 1
  ref = Ar
FEATURE [App::DocumentObjectGroupPython] G4_lAr  # scripted group (container) (typed FeaturePython)
  Dunit = g/cm3
  Dvalue = 1.396
  Group = -> [Ar]
  conduct = 2
  density = 1
  expand = 3
  formula = G4_lAr
  name = G4_lAr
  specific = 4
FEATURE [App::DocumentObjectGroupPython] Br  label="Br : 1"  # scripted group (container) (typed FeaturePython)
  n = 1
  ref = Br
FEATURE [App::DocumentObjectGroupPython] G4_lBr  # scripted group (container) (typed FeaturePython)
  Dunit = g/cm3
  Dvalue = 3.1028
  Group = -> [Br]
  conduct = 2
  density = 1
  expand = 3
  formula = G4_lBr
  name = G4_lBr
  specific = 4
FEATURE [App::DocumentObjectGroupPython] Kr  label="Kr : 1"  # scripted group (container) (typed FeaturePython)
  n = 1
  ref = Kr
FEATURE [App::DocumentObjectGroupPython] G4_lKr  # scripted group (container) (typed FeaturePython)
  Dunit = g/cm3
  Dvalue = 2.418
  Group = -> [Kr]
  conduct = 2
  density = 1
  expand = 3
  formula = G4_lKr
  name = G4_lKr
  specific = 4
FEATURE [App::DocumentObjectGroupPython] Xe  label="Xe : 1"  # scripted group (container) (typed FeaturePython)
  n = 1
  ref = Xe
FEATURE [App::DocumentObjectGroupPython] G4_lXe  # scripted group (container) (typed FeaturePython)
  Dunit = g/cm3
  Dvalue = 2.953
  Group = -> [Xe]
  conduct = 2
  density = 1
  expand = 3
  formula = G4_lXe
  name = G4_lXe
  specific = 4
FEATURE [App::DocumentObjectGroupPython] O_element107  label="O_element : 061"  # scripted group (container) (typed FeaturePython)
  n = 4
  ref = O_element
FEATURE [App::DocumentObjectGroupPython] Pb_element004  label="Pb_element : 002"  # scripted group (container) (typed FeaturePython)
  n = 1
  ref = Pb_element
FEATURE [App::DocumentObjectGroupPython] W_element005  label="W_element : 005"  # scripted group (container) (typed FeaturePython)
  n = 1
  ref = W_element
FEATURE [App::DocumentObjectGroupPython] G4_PbWO4  # scripted group (container) (typed FeaturePython)
  Dunit = g/cm3
  Dvalue = 8.28
  Group = -> [O_element107,Pb_element004,W_element005]
  conduct = 2
  density = 1
  expand = 3
  formula = G4_PbWO4
  name = G4_PbWO4
  specific = 4
FEATURE [App::DocumentObjectGroupPython] alactic  label="alactic : 1"  # scripted group (container) (typed FeaturePython)
  n = 1
  ref = alactic
FEATURE [App::DocumentObjectGroupPython] G4_Galactic  # scripted group (container) (typed FeaturePython)
  Dunit = g/cm3
  Dvalue = 0
  Group = -> [alactic]
  conduct = 2
  density = 1
  expand = 3
  formula = G4_Galactic
  name = G4_Galactic
  specific = 4
FEATURE [App::DocumentObjectGroupPython] RAPHITE_POROUS  label="RAPHITE_POROUS : 1"  # scripted group (container) (typed FeaturePython)
  n = 1
  ref = RAPHITE_POROUS
FEATURE [App::DocumentObjectGroupPython] G4_GRAPHITE_POROUS  # scripted group (container) (typed FeaturePython)
  Dunit = g/cm3
  Dvalue = 1.7
  Group = -> [RAPHITE_POROUS]
  conduct = 2
  density = 1
  expand = 3
  formula = G4_GRAPHITE_POROUS
  name = G4_GRAPHITE_POROUS
  specific = 4
FEATURE [App::DocumentObjectGroupPython] H_element115  label="H_element : 0.150"  # scripted group (container) (typed FeaturePython)
  n = 0.080538
FEATURE [App::DocumentObjectGroupPython] C_element125  label="C_element : 0.600"  # scripted group (container) (typed FeaturePython)
  n = 0.599848
FEATURE [App::DocumentObjectGroupPython] O_element108  label="O_element : 0.320"  # scripted group (container) (typed FeaturePython)
  n = 0.319614
FEATURE [App::DocumentObjectGroupPython] G4_LUCITE  # scripted group (container) (typed FeaturePython)
  Dunit = g/cm3
  Dvalue = 1.19
  Group = -> [H_element115,C_element125,O_element108]
  conduct = 2
  density = 1
  expand = 3
  formula = G4_LUCITE
  name = G4_LUCITE
  specific = 4
FEATURE [App::DocumentObjectGroupPython] Cu_element002  label="Cu_element : 62"  # scripted group (container) (typed FeaturePython)
  n = 62
  ref = Cu_element
FEATURE [App::DocumentObjectGroupPython] Zn_element002  label="Zn_element : 35"  # scripted group (container) (typed FeaturePython)
  n = 35
  ref = Zn_element
FEATURE [App::DocumentObjectGroupPython] Pb_element005  label="Pb_element : 3"  # scripted group (container) (typed FeaturePython)
  n = 3
  ref = Pb_element
FEATURE [App::DocumentObjectGroupPython] G4_BRASS  # scripted group (container) (typed FeaturePython)
  Dunit = g/cm3
  Dvalue = 8.52
  Group = -> [Cu_element002,Zn_element002,Pb_element005]
  conduct = 2
  density = 1
  expand = 3
  formula = G4_BRASS
  name = G4_BRASS
  specific = 4
FEATURE [App::DocumentObjectGroupPython] Cu_element003  label="Cu_element : 89"  # scripted group (container) (typed FeaturePython)
  n = 89
  ref = Cu_element
FEATURE [App::DocumentObjectGroupPython] Zn_element003  label="Zn_element : 9"  # scripted group (container) (typed FeaturePython)
  n = 9
  ref = Zn_element
FEATURE [App::DocumentObjectGroupPython] Pb_element006  label="Pb_element : 2"  # scripted group (container) (typed FeaturePython)
  n = 2
  ref = Pb_element
FEATURE [App::DocumentObjectGroupPython] G4_BRONZE  # scripted group (container) (typed FeaturePython)
  Dunit = g/cm3
  Dvalue = 8.82
  Group = -> [Cu_element003,Zn_element003,Pb_element006]
  conduct = 2
  density = 1
  expand = 3
  formula = G4_BRONZE
  name = G4_BRONZE
  specific = 4
FEATURE [App::DocumentObjectGroupPython] Fe_element008  label="Fe_element : 74"  # scripted group (container) (typed FeaturePython)
  n = 74
  ref = Fe_element
FEATURE [App::DocumentObjectGroupPython] Cr_element002  label="Cr_element : 18"  # scripted group (container) (typed FeaturePython)
  n = 18
  ref = Cr_element
FEATURE [App::DocumentObjectGroupPython] Ni_element002  label="Ni_element : 8"  # scripted group (container) (typed FeaturePython)
  n = 8
  ref = Ni_element
FEATURE [App::DocumentObjectGroupPython] G4_STAINLESS_STEEL  label="G4_STAINLESS-STEEL"  # scripted group (container) (typed FeaturePython)
  Dunit = g/cm3
  Dvalue = 8
  Group = -> [Fe_element008,Cr_element002,Ni_element002]
  conduct = 2
  density = 1
  expand = 3
  formula = G4_STAINLESS-STEEL
  name = G4_STAINLESS-STEEL
  specific = 4
FEATURE [App::DocumentObjectGroupPython] H_element116  label="H_element : 064"  # scripted group (container) (typed FeaturePython)
  n = 18
  ref = H_element
FEATURE [App::DocumentObjectGroupPython] C_element126  label="C_element : 071"  # scripted group (container) (typed FeaturePython)
  n = 12
  ref = C_element
FEATURE [App::DocumentObjectGroupPython] O_element109  label="O_element : 062"  # scripted group (container) (typed FeaturePython)
  n = 7
  ref = O_element
FEATURE [App::DocumentObjectGroupPython] G4_CR39  # scripted group (container) (typed FeaturePython)
  Dunit = g/cm3
  Dvalue = 1.32
  Group = -> [H_element116,C_element126,O_element109]
  conduct = 2
  density = 1
  expand = 3
  formula = G4_CR39
  name = G4_CR39
  specific = 4
FEATURE [App::DocumentObjectGroupPython] H_element117  label="H_element : 38"  # scripted group (container) (typed FeaturePython)
  n = 38
  ref = H_element
FEATURE [App::DocumentObjectGroupPython] C_element127  label="C_element : 072"  # scripted group (container) (typed FeaturePython)
  n = 18
  ref = C_element
FEATURE [App::DocumentObjectGroupPython] O_element110  label="O_element : 063"  # scripted group (container) (typed FeaturePython)
  n = 1
  ref = O_element
FEATURE [App::DocumentObjectGroupPython] G4_OCTADECANOL  # scripted group (container) (typed FeaturePython)
  Dunit = g/cm3
  Dvalue = 0.812
  Group = -> [H_element117,C_element127,O_element110]
  conduct = 2
  density = 1
  expand = 3
  formula = G4_OCTADECANOL
  name = G4_OCTADECANOL
  specific = 4
FEATURE [App::DocumentObjectGroupPython] HEP  # scripted group (container) (typed FeaturePython)
  Group = -> [G4_lH2,G4_lN2,G4_lO2,G4_lAr,G4_lBr,G4_lKr,G4_lXe,G4_PbWO4,G4_Galactic,G4_GRAPHITE_POROUS,G4_LUCITE,G4_BRASS,G4_BRONZE,G4_STAINLESS_STEEL,G4_CR39,G4_OCTADECANOL]
FEATURE [App::DocumentObjectGroupPython] C_element128  label="C_element : 073"  # scripted group (container) (typed FeaturePython)
  n = 14
  ref = C_element
FEATURE [App::DocumentObjectGroupPython] H_element118  label="H_element : 065"  # scripted group (container) (typed FeaturePython)
  n = 10
  ref = H_element
FEATURE [App::DocumentObjectGroupPython] O_element111  label="O_element : 064"  # scripted group (container) (typed FeaturePython)
  n = 2
  ref = O_element
FEATURE [App::DocumentObjectGroupPython] N_element050  label="N_element : 023"  # scripted group (container) (typed FeaturePython)
  n = 2
  ref = N_element
FEATURE [App::DocumentObjectGroupPython] G4_KEVLAR  # scripted group (container) (typed FeaturePython)
  Dunit = g/cm3
  Dvalue = 1.44
  Group = -> [C_element128,H_element118,O_element111,N_element050]
  conduct = 2
  density = 1
  expand = 3
  formula = G4_KEVLAR
  name = G4_KEVLAR
  specific = 4
FEATURE [App::DocumentObjectGroupPython] C_element129  label="C_element : 074"  # scripted group (container) (typed FeaturePython)
  n = 10
  ref = C_element
FEATURE [App::DocumentObjectGroupPython] H_element119  label="H_element : 066"  # scripted group (container) (typed FeaturePython)
  n = 8
  ref = H_element
FEATURE [App::DocumentObjectGroupPython] O_element112  label="O_element : 065"  # scripted group (container) (typed FeaturePython)
  n = 4
  ref = O_element
FEATURE [App::DocumentObjectGroupPython] G4_DACRON  # scripted group (container) (typed FeaturePython)
  Dunit = g/cm3
  Dvalue = 1.4
  Group = -> [C_element129,H_element119,O_element112]
  conduct = 2
  density = 1
  expand = 3
  formula = G4_DACRON
  name = G4_DACRON
  specific = 4
FEATURE [App::DocumentObjectGroupPython] C_element130  label="C_element : 075"  # scripted group (container) (typed FeaturePython)
  n = 4
  ref = C_element
FEATURE [App::DocumentObjectGroupPython] H_element120  label="H_element : 067"  # scripted group (container) (typed FeaturePython)
  n = 5
  ref = H_element
FEATURE [App::DocumentObjectGroupPython] Cl_element030  label="Cl_element : 016"  # scripted group (container) (typed FeaturePython)
  n = 1
  ref = Cl_element
FEATURE [App::DocumentObjectGroupPython] G4_NEOPRENE  # scripted group (container) (typed FeaturePython)
  Dunit = g/cm3
  Dvalue = 1.23
  Group = -> [C_element130,H_element120,Cl_element030]
  conduct = 2
  density = 1
  expand = 3
  formula = G4_NEOPRENE
  name = G4_NEOPRENE
  specific = 4
FEATURE [App::DocumentObjectGroupPython] Space  # scripted group (container) (typed FeaturePython)
  Group = -> [G4_KEVLAR,G4_DACRON,G4_NEOPRENE]
FEATURE [App::DocumentObjectGroupPython] H_element121  label="H_element : 068"  # scripted group (container) (typed FeaturePython)
  n = 5
  ref = H_element
FEATURE [App::DocumentObjectGroupPython] C_element131  label="C_element : 076"  # scripted group (container) (typed FeaturePython)
  n = 4
  ref = C_element
FEATURE [App::DocumentObjectGroupPython] N_element051  label="N_element : 3"  # scripted group (container) (typed FeaturePython)
  n = 3
  ref = N_element
FEATURE [App::DocumentObjectGroupPython] O_element113  label="O_element : 066"  # scripted group (container) (typed FeaturePython)
  n = 1
  ref = O_element
FEATURE [App::DocumentObjectGroupPython] G4_CYTOSINE  # scripted group (container) (typed FeaturePython)
  Dunit = g/cm3
  Dvalue = 1.55
  Group = -> [H_element121,C_element131,N_element051,O_element113]
  conduct = 2
  density = 1
  expand = 3
  formula = G4_CYTOSINE
  name = G4_CYTOSINE
  specific = 4
FEATURE [App::DocumentObjectGroupPython] H_element122  label="H_element : 069"  # scripted group (container) (typed FeaturePython)
  n = 6
  ref = H_element
FEATURE [App::DocumentObjectGroupPython] C_element132  label="C_element : 077"  # scripted group (container) (typed FeaturePython)
  n = 5
  ref = C_element
FEATURE [App::DocumentObjectGroupPython] N_element052  label="N_element : 024"  # scripted group (container) (typed FeaturePython)
  n = 2
  ref = N_element
FEATURE [App::DocumentObjectGroupPython] O_element114  label="O_element : 067"  # scripted group (container) (typed FeaturePython)
  n = 2
  ref = O_element
FEATURE [App::DocumentObjectGroupPython] G4_THYMINE  # scripted group (container) (typed FeaturePython)
  Dunit = g/cm3
  Dvalue = 1.23
  Group = -> [H_element122,C_element132,N_element052,O_element114]
  conduct = 2
  density = 1
  expand = 3
  formula = G4_THYMINE
  name = G4_THYMINE
  specific = 4
FEATURE [App::DocumentObjectGroupPython] H_element123  label="H_element : 070"  # scripted group (container) (typed FeaturePython)
  n = 4
  ref = H_element
FEATURE [App::DocumentObjectGroupPython] C_element133  label="C_element : 078"  # scripted group (container) (typed FeaturePython)
  n = 4
  ref = C_element
FEATURE [App::DocumentObjectGroupPython] N_element053  label="N_element : 025"  # scripted group (container) (typed FeaturePython)
  n = 2
  ref = N_element
FEATURE [App::DocumentObjectGroupPython] O_element115  label="O_element : 068"  # scripted group (container) (typed FeaturePython)
  n = 2
  ref = O_element
FEATURE [App::DocumentObjectGroupPython] G4_URACIL  # scripted group (container) (typed FeaturePython)
  Dunit = g/cm3
  Dvalue = 1.32
  Group = -> [H_element123,C_element133,N_element053,O_element115]
  conduct = 2
  density = 1
  expand = 3
  formula = G4_URACIL
  name = G4_URACIL
  specific = 4
FEATURE [App::DocumentObjectGroupPython] H_element124  label="H_element : 071"  # scripted group (container) (typed FeaturePython)
  n = 4
  ref = H_element
FEATURE [App::DocumentObjectGroupPython] C_element134  label="C_element : 079"  # scripted group (container) (typed FeaturePython)
  n = 5
  ref = C_element
FEATURE [App::DocumentObjectGroupPython] N_element054  label="N_element : 026"  # scripted group (container) (typed FeaturePython)
  n = 5
  ref = N_element
FEATURE [App::DocumentObjectGroupPython] G4_DNA_ADENINE  # scripted group (container) (typed FeaturePython)
  Dunit = g/cm3
  Dvalue = 1
  Group = -> [H_element124,C_element134,N_element054]
  conduct = 2
  density = 1
  expand = 3
  formula = G4_DNA_ADENINE
  name = G4_DNA_ADENINE
  specific = 4
FEATURE [App::DocumentObjectGroupPython] H_element125  label="H_element : 072"  # scripted group (container) (typed FeaturePython)
  n = 4
  ref = H_element
FEATURE [App::DocumentObjectGroupPython] C_element135  label="C_element : 080"  # scripted group (container) (typed FeaturePython)
  n = 5
  ref = C_element
FEATURE [App::DocumentObjectGroupPython] N_element055  label="N_element : 027"  # scripted group (container) (typed FeaturePython)
  n = 5
  ref = N_element
FEATURE [App::DocumentObjectGroupPython] O_element116  label="O_element : 069"  # scripted group (container) (typed FeaturePython)
  n = 1
  ref = O_element
FEATURE [App::DocumentObjectGroupPython] G4_DNA_GUANINE  # scripted group (container) (typed FeaturePython)
  Dunit = g/cm3
  Dvalue = 1
  Group = -> [H_element125,C_element135,N_element055,O_element116]
  conduct = 2
  density = 1
  expand = 3
  formula = G4_DNA_GUANINE
  name = G4_DNA_GUANINE
  specific = 4
FEATURE [App::DocumentObjectGroupPython] H_element126  label="H_element : 073"  # scripted group (container) (typed FeaturePython)
  n = 4
  ref = H_element
FEATURE [App::DocumentObjectGroupPython] C_element136  label="C_element : 081"  # scripted group (container) (typed FeaturePython)
  n = 4
  ref = C_element
FEATURE [App::DocumentObjectGroupPython] N_element056  label="N_element : 028"  # scripted group (container) (typed FeaturePython)
  n = 3
  ref = N_element
FEATURE [App::DocumentObjectGroupPython] O_element117  label="O_element : 070"  # scripted group (container) (typed FeaturePython)
  n = 1
  ref = O_element
FEATURE [App::DocumentObjectGroupPython] G4_DNA_CYTOSINE  # scripted group (container) (typed FeaturePython)
  Dunit = g/cm3
  Dvalue = 1
  Group = -> [H_element126,C_element136,N_element056,O_element117]
  conduct = 2
  density = 1
  expand = 3
  formula = G4_DNA_CYTOSINE
  name = G4_DNA_CYTOSINE
  specific = 4
FEATURE [App::DocumentObjectGroupPython] H_element127  label="H_element : 074"  # scripted group (container) (typed FeaturePython)
  n = 5
  ref = H_element
FEATURE [App::DocumentObjectGroupPython] C_element137  label="C_element : 082"  # scripted group (container) (typed FeaturePython)
  n = 5
  ref = C_element
FEATURE [App::DocumentObjectGroupPython] N_element057  label="N_element : 029"  # scripted group (container) (typed FeaturePython)
  n = 2
  ref = N_element
FEATURE [App::DocumentObjectGroupPython] O_element118  label="O_element : 071"  # scripted group (container) (typed FeaturePython)
  n = 2
  ref = O_element
FEATURE [App::DocumentObjectGroupPython] G4_DNA_THYMINE  # scripted group (container) (typed FeaturePython)
  Dunit = g/cm3
  Dvalue = 1
  Group = -> [H_element127,C_element137,N_element057,O_element118]
  conduct = 2
  density = 1
  expand = 3
  formula = G4_DNA_THYMINE
  name = G4_DNA_THYMINE
  specific = 4
FEATURE [App::DocumentObjectGroupPython] H_element128  label="H_element : 075"  # scripted group (container) (typed FeaturePython)
  n = 3
  ref = H_element
FEATURE [App::DocumentObjectGroupPython] C_element138  label="C_element : 083"  # scripted group (container) (typed FeaturePython)
  n = 4
  ref = C_element
FEATURE [App::DocumentObjectGroupPython] N_element058  label="N_element : 030"  # scripted group (container) (typed FeaturePython)
  n = 2
  ref = N_element
FEATURE [App::DocumentObjectGroupPython] O_element119  label="O_element : 072"  # scripted group (container) (typed FeaturePython)
  n = 2
  ref = O_element
FEATURE [App::DocumentObjectGroupPython] G4_DNA_URACIL  # scripted group (container) (typed FeaturePython)
  Dunit = g/cm3
  Dvalue = 1
  Group = -> [H_element128,C_element138,N_element058,O_element119]
  conduct = 2
  density = 1
  expand = 3
  formula = G4_DNA_URACIL
  name = G4_DNA_URACIL
  specific = 4
FEATURE [App::DocumentObjectGroupPython] H_element129  label="H_element : 076"  # scripted group (container) (typed FeaturePython)
  n = 10
  ref = H_element
FEATURE [App::DocumentObjectGroupPython] C_element139  label="C_element : 084"  # scripted group (container) (typed FeaturePython)
  n = 10
  ref = C_element
FEATURE [App::DocumentObjectGroupPython] N_element059  label="N_element : 031"  # scripted group (container) (typed FeaturePython)
  n = 5
  ref = N_element
FEATURE [App::DocumentObjectGroupPython] O_element120  label="O_element : 073"  # scripted group (container) (typed FeaturePython)
  n = 4
  ref = O_element
FEATURE [App::DocumentObjectGroupPython] G4_DNA_ADENOSINE  # scripted group (container) (typed FeaturePython)
  Dunit = g/cm3
  Dvalue = 1
  Group = -> [H_element129,C_element139,N_element059,O_element120]
  conduct = 2
  density = 1
  expand = 3
  formula = G4_DNA_ADENOSINE
  name = G4_DNA_ADENOSINE
  specific = 4
FEATURE [App::DocumentObjectGroupPython] H_element130  label="H_element : 077"  # scripted group (container) (typed FeaturePython)
  n = 10
  ref = H_element
FEATURE [App::DocumentObjectGroupPython] C_element140  label="C_element : 085"  # scripted group (container) (typed FeaturePython)
  n = 10
  ref = C_element
FEATURE [App::DocumentObjectGroupPython] N_element060  label="N_element : 032"  # scripted group (container) (typed FeaturePython)
  n = 5
  ref = N_element
FEATURE [App::DocumentObjectGroupPython] O_element121  label="O_element : 074"  # scripted group (container) (typed FeaturePython)
  n = 5
  ref = O_element
FEATURE [App::DocumentObjectGroupPython] G4_DNA_GUANOSINE  # scripted group (container) (typed FeaturePython)
  Dunit = g/cm3
  Dvalue = 1
  Group = -> [H_element130,C_element140,N_element060,O_element121]
  conduct = 2
  density = 1
  expand = 3
  formula = G4_DNA_GUANOSINE
  name = G4_DNA_GUANOSINE
  specific = 4
FEATURE [App::DocumentObjectGroupPython] H_element131  label="H_element : 078"  # scripted group (container) (typed FeaturePython)
  n = 10
  ref = H_element
FEATURE [App::DocumentObjectGroupPython] C_element141  label="C_element : 086"  # scripted group (container) (typed FeaturePython)
  n = 9
  ref = C_element
FEATURE [App::DocumentObjectGroupPython] N_element061  label="N_element : 033"  # scripted group (container) (typed FeaturePython)
  n = 3
  ref = N_element
FEATURE [App::DocumentObjectGroupPython] O_element122  label="O_element : 075"  # scripted group (container) (typed FeaturePython)
  n = 5
  ref = O_element
FEATURE [App::DocumentObjectGroupPython] G4_DNA_CYTIDINE  # scripted group (container) (typed FeaturePython)
  Dunit = g/cm3
  Dvalue = 1
  Group = -> [H_element131,C_element141,N_element061,O_element122]
  conduct = 2
  density = 1
  expand = 3
  formula = G4_DNA_CYTIDINE
  name = G4_DNA_CYTIDINE
  specific = 4
FEATURE [App::DocumentObjectGroupPython] H_element132  label="H_element : 079"  # scripted group (container) (typed FeaturePython)
  n = 9
  ref = H_element
FEATURE [App::DocumentObjectGroupPython] C_element142  label="C_element : 087"  # scripted group (container) (typed FeaturePython)
  n = 9
  ref = C_element
FEATURE [App::DocumentObjectGroupPython] N_element062  label="N_element : 034"  # scripted group (container) (typed FeaturePython)
  n = 2
  ref = N_element
FEATURE [App::DocumentObjectGroupPython] O_element123  label="O_element : 076"  # scripted group (container) (typed FeaturePython)
  n = 6
  ref = O_element
FEATURE [App::DocumentObjectGroupPython] G4_DNA_URIDINE  # scripted group (container) (typed FeaturePython)
  Dunit = g/cm3
  Dvalue = 1
  Group = -> [H_element132,C_element142,N_element062,O_element123]
  conduct = 2
  density = 1
  expand = 3
  formula = G4_DNA_URIDINE
  name = G4_DNA_URIDINE
  specific = 4
FEATURE [App::DocumentObjectGroupPython] H_element133  label="H_element : 080"  # scripted group (container) (typed FeaturePython)
  n = 11
  ref = H_element
FEATURE [App::DocumentObjectGroupPython] C_element143  label="C_element : 088"  # scripted group (container) (typed FeaturePython)
  n = 10
  ref = C_element
FEATURE [App::DocumentObjectGroupPython] N_element063  label="N_element : 035"  # scripted group (container) (typed FeaturePython)
  n = 2
  ref = N_element
FEATURE [App::DocumentObjectGroupPython] O_element124  label="O_element : 077"  # scripted group (container) (typed FeaturePython)
  n = 6
  ref = O_element
FEATURE [App::DocumentObjectGroupPython] G4_DNA_METHYLURIDINE  # scripted group (container) (typed FeaturePython)
  Dunit = g/cm3
  Dvalue = 1
  Group = -> [H_element133,C_element143,N_element063,O_element124]
  conduct = 2
  density = 1
  expand = 3
  formula = G4_DNA_METHYLURIDINE
  name = G4_DNA_METHYLURIDINE
  specific = 4
FEATURE [App::DocumentObjectGroupPython] P_element014  label="P_element : 003"  # scripted group (container) (typed FeaturePython)
  n = 1
  ref = P_element
FEATURE [App::DocumentObjectGroupPython] O_element125  label="O_element : 078"  # scripted group (container) (typed FeaturePython)
  n = 3
  ref = O_element
FEATURE [App::DocumentObjectGroupPython] G4_DNA_MONOPHOSPHATE  # scripted group (container) (typed FeaturePython)
  Dunit = g/cm3
  Dvalue = 1
  Group = -> [P_element014,O_element125]
  conduct = 2
  density = 1
  expand = 3
  formula = G4_DNA_MONOPHOSPHATE
  name = G4_DNA_MONOPHOSPHATE
  specific = 4
FEATURE [App::DocumentObjectGroupPython] H_element134  label="H_element : 081"  # scripted group (container) (typed FeaturePython)
  n = 10
  ref = H_element
FEATURE [App::DocumentObjectGroupPython] C_element144  label="C_element : 089"  # scripted group (container) (typed FeaturePython)
  n = 10
  ref = C_element
FEATURE [App::DocumentObjectGroupPython] N_element064  label="N_element : 036"  # scripted group (container) (typed FeaturePython)
  n = 5
  ref = N_element
FEATURE [App::DocumentObjectGroupPython] O_element126  label="O_element : 079"  # scripted group (container) (typed FeaturePython)
  n = 7
  ref = O_element
FEATURE [App::DocumentObjectGroupPython] P_element015  label="P_element : 004"  # scripted group (container) (typed FeaturePython)
  n = 1
  ref = P_element
FEATURE [App::DocumentObjectGroupPython] G4_DNA_A  # scripted group (container) (typed FeaturePython)
  Dunit = g/cm3
  Dvalue = 1
  Group = -> [H_element134,C_element144,N_element064,O_element126,P_element015]
  conduct = 2
  density = 1
  expand = 3
  formula = G4_DNA_A
  name = G4_DNA_A
  specific = 4
FEATURE [App::DocumentObjectGroupPython] H_element135  label="H_element : 082"  # scripted group (container) (typed FeaturePython)
  n = 10
  ref = H_element
FEATURE [App::DocumentObjectGroupPython] C_element145  label="C_element : 090"  # scripted group (container) (typed FeaturePython)
  n = 10
  ref = C_element
FEATURE [App::DocumentObjectGroupPython] N_element065  label="N_element : 037"  # scripted group (container) (typed FeaturePython)
  n = 5
  ref = N_element
FEATURE [App::DocumentObjectGroupPython] O_element127  label="O_element : 8"  # scripted group (container) (typed FeaturePython)
  n = 8
  ref = O_element
FEATURE [App::DocumentObjectGroupPython] P_element016  label="P_element : 005"  # scripted group (container) (typed FeaturePython)
  n = 1
  ref = P_element
FEATURE [App::DocumentObjectGroupPython] G4_DNA_G  # scripted group (container) (typed FeaturePython)
  Dunit = g/cm3
  Dvalue = 1
  Group = -> [H_element135,C_element145,N_element065,O_element127,P_element016]
  conduct = 2
  density = 1
  expand = 3
  formula = G4_DNA_G
  name = G4_DNA_G
  specific = 4
FEATURE [App::DocumentObjectGroupPython] H_element136  label="H_element : 083"  # scripted group (container) (typed FeaturePython)
  n = 10
  ref = H_element
FEATURE [App::DocumentObjectGroupPython] C_element146  label="C_element : 091"  # scripted group (container) (typed FeaturePython)
  n = 9
  ref = C_element
FEATURE [App::DocumentObjectGroupPython] N_element066  label="N_element : 038"  # scripted group (container) (typed FeaturePython)
  n = 3
  ref = N_element
FEATURE [App::DocumentObjectGroupPython] O_element128  label="O_element : 080"  # scripted group (container) (typed FeaturePython)
  n = 8
  ref = O_element
FEATURE [App::DocumentObjectGroupPython] P_element017  label="P_element : 006"  # scripted group (container) (typed FeaturePython)
  n = 1
  ref = P_element
FEATURE [App::DocumentObjectGroupPython] G4_DNA_C  # scripted group (container) (typed FeaturePython)
  Dunit = g/cm3
  Dvalue = 1
  Group = -> [H_element136,C_element146,N_element066,O_element128,P_element017]
  conduct = 2
  density = 1
  expand = 3
  formula = G4_DNA_C
  name = G4_DNA_C
  specific = 4
FEATURE [App::DocumentObjectGroupPython] H_element137  label="H_element : 084"  # scripted group (container) (typed FeaturePython)
  n = 9
  ref = H_element
FEATURE [App::DocumentObjectGroupPython] C_element147  label="C_element : 092"  # scripted group (container) (typed FeaturePython)
  n = 9
  ref = C_element
FEATURE [App::DocumentObjectGroupPython] N_element067  label="N_element : 039"  # scripted group (container) (typed FeaturePython)
  n = 2
  ref = N_element
FEATURE [App::DocumentObjectGroupPython] O_element129  label="O_element : 9"  # scripted group (container) (typed FeaturePython)
  n = 9
  ref = O_element
FEATURE [App::DocumentObjectGroupPython] P_element018  label="P_element : 007"  # scripted group (container) (typed FeaturePython)
  n = 1
  ref = P_element
FEATURE [App::DocumentObjectGroupPython] G4_DNA_U  # scripted group (container) (typed FeaturePython)
  Dunit = g/cm3
  Dvalue = 1
  Group = -> [H_element137,C_element147,N_element067,O_element129,P_element018]
  conduct = 2
  density = 1
  expand = 3
  formula = G4_DNA_U
  name = G4_DNA_U
  specific = 4
FEATURE [App::DocumentObjectGroupPython] H_element138  label="H_element : 085"  # scripted group (container) (typed FeaturePython)
  n = 11
  ref = H_element
FEATURE [App::DocumentObjectGroupPython] C_element148  label="C_element : 093"  # scripted group (container) (typed FeaturePython)
  n = 10
  ref = C_element
FEATURE [App::DocumentObjectGroupPython] N_element068  label="N_element : 040"  # scripted group (container) (typed FeaturePython)
  n = 2
  ref = N_element
FEATURE [App::DocumentObjectGroupPython] O_element130  label="O_element : 081"  # scripted group (container) (typed FeaturePython)
  n = 9
  ref = O_element
FEATURE [App::DocumentObjectGroupPython] P_element019  label="P_element : 008"  # scripted group (container) (typed FeaturePython)
  n = 1
  ref = P_element
FEATURE [App::DocumentObjectGroupPython] G4_DNA_MU  # scripted group (container) (typed FeaturePython)
  Dunit = g/cm3
  Dvalue = 1
  Group = -> [H_element138,C_element148,N_element068,O_element130,P_element019]
  conduct = 2
  density = 1
  expand = 3
  formula = G4_DNA_MU
  name = G4_DNA_MU
  specific = 4
FEATURE [App::DocumentObjectGroupPython] BioChemical  # scripted group (container) (typed FeaturePython)
  Group = -> [G4_CYTOSINE,G4_THYMINE,G4_URACIL,G4_DNA_ADENINE,G4_DNA_GUANINE,G4_DNA_CYTOSINE,G4_DNA_THYMINE,G4_DNA_URACIL,G4_DNA_ADENOSINE,G4_DNA_GUANOSINE,G4_DNA_CYTIDINE,G4_DNA_URIDINE,G4_DNA_METHYLURIDINE,G4_DNA_MONOPHOSPHATE,G4_DNA_A,G4_DNA_G,G4_DNA_C,G4_DNA_U,G4_DNA_MU]
FEATURE [App::DocumentObjectGroupPython] G4Materials  # scripted group (container) (typed FeaturePython)
  Group = -> [NIST,Element,HEP,Space,BioChemical]
  version = 1
FEATURE [App::DocumentObjectGroupPython] Geant4  # scripted group (container) (typed FeaturePython)
  Group = -> [G4Isotopes,G4Elements,G4Materials]
FEATURE [App::DocumentObjectGroupPython] Materials  # scripted group (container) (typed FeaturePython)
  Group = -> [Geant4]
FEATURE [Part::FeaturePython] GDMLBox_WorldBox  # WARN: FeaturePython — macro-defined, semantics opaque (R4)
  lunit = 2
  material = 5
  x = 608.4
  y = 473.2
  z = 26
FEATURE [Part::FeaturePython] GDMLBox_Box002  # WARN: FeaturePython — macro-defined, semantics opaque (R4)
  Placement = pos=(20,0,0) rot=(0,0,1;0rad)
  lunit = 2
  material = 0
  x = 20
  y = 20
  z = 10
FEATURE [Part::FeaturePython] GDMLSphere001  # WARN: FeaturePython — macro-defined, semantics opaque (R4)
  aunit = 1
  deltaphi = 360
  deltatheta = 180
  lunit = 2
  material = 0
  rmax = 2
  rmin = 0
  startphi = 0
  starttheta = 0
FEATURE [Part::FeaturePython] GDMLTube001  # WARN: FeaturePython — macro-defined, semantics opaque (R4)
  Placement = pos=(17,-4,0) rot=(0,0,1;0rad)
  aunit = 1
  deltaphi = 90
  lunit = 2
  material = 0
  rmax = 7
  rmin = 5
  startphi = 0
  z = 7
FEATURE [App::Part] LV_Sphere001
  Group = -> [GDMLSphere001]
  Origin = -> Origin008
  Placement = pos=(15,-5,0) rot=(0,0,1;0rad)
  SkinSurface = 0
FEATURE [App::Part] LV_Tube001
  Group = -> [GDMLTube001]
  Origin = -> Origin007
  SkinSurface = 0
FEATURE [App::Part] LV_Box002
  Group = -> [GDMLBox_Box002,LV_Tube001,LV_Sphere001]
  Origin = -> Origin006
  Placement = pos=(20,0,0) rot=(1,0,0;1.5708rad)
FEATURE [Part::FeaturePython] Array  # Draft array (typed FeaturePython)
  AlwaysSyncPlacement = false
  Angle = 360
  ArrayType = 0
  Axis = (0,0,1)
  Base = -> LV_Box002
  Center = (0,0,0)
  Count = 4
  ExpandArray = false
  Fuse = true
  IntervalAxis = (0,0,0)
  IntervalX = (100,0,0)
  IntervalY = (0,100,0)
  IntervalZ = (0,0,100)
  NumberCircles = 3
  NumberPolar = 5
  NumberX = 2
  NumberY = 2
  NumberZ = 1
  Placement = pos=(-7,-15,0) rot=(0,0,1;0.523599rad)
  PlacementList = 4 placements: [(20,0,0),(20,100,0),(120,0,0),(120,100,0)]
  RadialDistance = 50
  ScaleList = (4) [(1,1,1),(1,1,1),(1,1,1),(1,1,1)]
  Symmetry = 1
  TangentialDistance = 25
FEATURE [App::Part] Part  label="experiment"
  Group = -> [LV_Box002,Array]
  Origin = -> Origin001
  Placement = pos=(30,30,0) rot=(0,0,1;0rad)
FEATURE [Part::Sphere] Sphere
  Angle1 = -90
  Angle2 = 90
  Angle3 = 360
  AttacherType = Attacher::AttachEngine3D
  Placement = pos=(53,14,0) rot=(0,0,1;0rad)
  Radius = 5
FEATURE [App::Part] LV_Box001  label="LV_Sphere"
  Group = -> [Sphere]
  Origin = -> Origin005
FEATURE [App::Part] worldVOL
  Group = -> [GDMLBox_WorldBox,Part,LV_Box001]
  Origin = -> Origin
